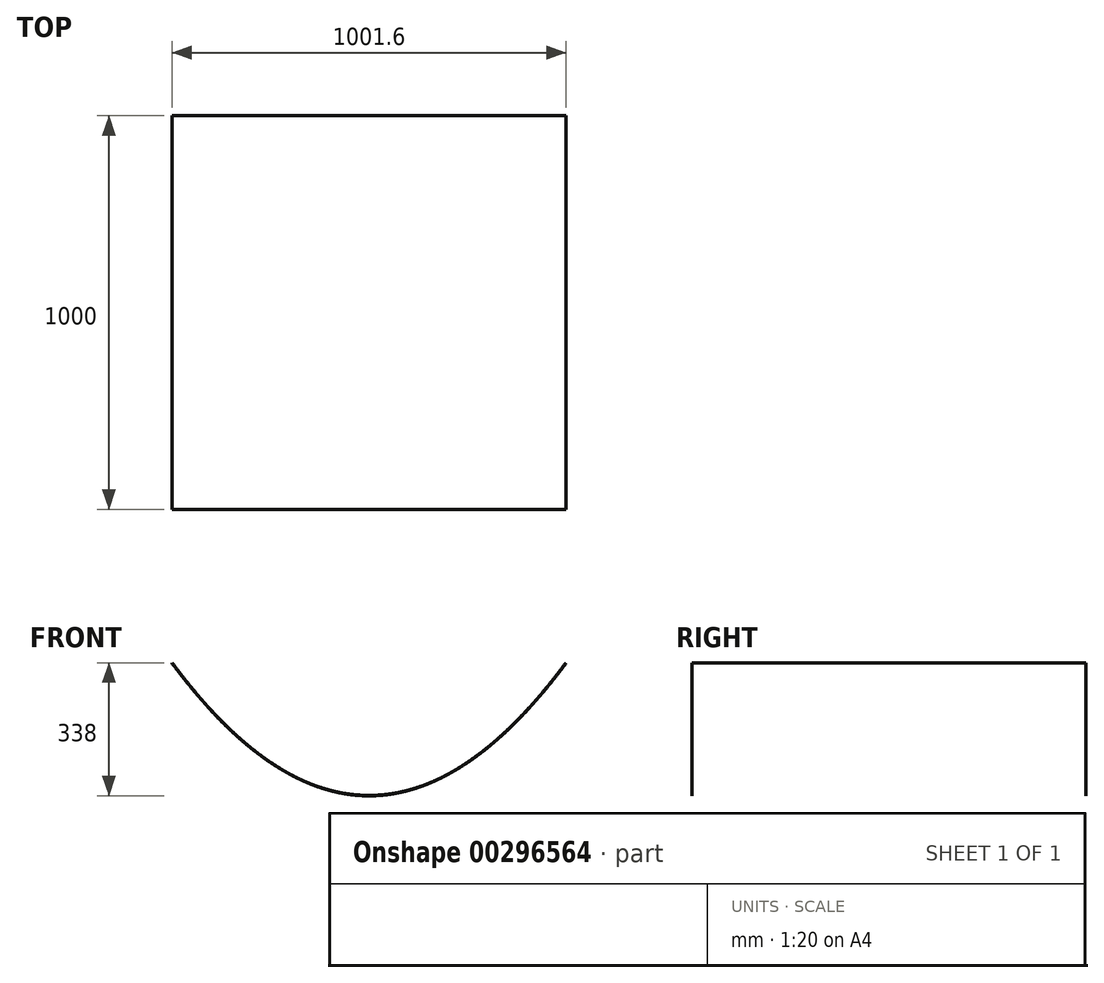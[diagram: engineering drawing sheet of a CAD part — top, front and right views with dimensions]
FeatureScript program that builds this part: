
annotation { "Feature Type Name" : "Feature", "Feature Type Description" : "" }
export const myFeature = defineFeature(function(context is Context, id is Id, definition is map)
    precondition{}
    {
        {
            var Q0;
            Q0=qCreatedBy(makeId("Front.planeOp"),FACE);
            var sketch = newSketch(context, id + "F0", { "sketchPlane" : qUnion([Q0])});
            skLineSegment(sketch, "E0", {"start": v(-500, 168.5) * mm, "end": v(-498.89, 167) * mm});
            skLineSegment(sketch, "E1", {"start": v(-498.89, 167) * mm, "end": v(-497.78, 165.5) * mm});
            skLineSegment(sketch, "E2", {"start": v(-497.78, 165.5) * mm, "end": v(-496.67, 164.02) * mm});
            skLineSegment(sketch, "E3", {"start": v(-496.67, 164.02) * mm, "end": v(-495.56, 162.53) * mm});
            skLineSegment(sketch, "E4", {"start": v(-495.56, 162.53) * mm, "end": v(-494.44, 161.05) * mm});
            skLineSegment(sketch, "E5", {"start": v(-494.44, 161.05) * mm, "end": v(-493.33, 159.57) * mm});
            skLineSegment(sketch, "E6", {"start": v(-493.33, 159.57) * mm, "end": v(-492.22, 158.1) * mm});
            skLineSegment(sketch, "E7", {"start": v(-492.22, 158.1) * mm, "end": v(-491.11, 156.62) * mm});
            skLineSegment(sketch, "E8", {"start": v(-491.11, 156.62) * mm, "end": v(-490, 155.15) * mm});
            skLineSegment(sketch, "E9", {"start": v(-490, 155.15) * mm, "end": v(-488.89, 153.69) * mm});
            skLineSegment(sketch, "E10", {"start": v(-488.89, 153.69) * mm, "end": v(-487.78, 152.22) * mm});
            skLineSegment(sketch, "E11", {"start": v(-487.78, 152.22) * mm, "end": v(-486.67, 150.76) * mm});
            skLineSegment(sketch, "E12", {"start": v(-486.67, 150.76) * mm, "end": v(-485.56, 149.3) * mm});
            skLineSegment(sketch, "E13", {"start": v(-485.56, 149.3) * mm, "end": v(-484.44, 147.86) * mm});
            skLineSegment(sketch, "E14", {"start": v(-484.44, 147.86) * mm, "end": v(-483.33, 146.4) * mm});
            skLineSegment(sketch, "E15", {"start": v(-483.33, 146.4) * mm, "end": v(-482.22, 144.96) * mm});
            skLineSegment(sketch, "E16", {"start": v(-482.22, 144.96) * mm, "end": v(-481.11, 143.52) * mm});
            skLineSegment(sketch, "E17", {"start": v(-481.11, 143.52) * mm, "end": v(-480, 142.08) * mm});
            skLineSegment(sketch, "E18", {"start": v(-480, 142.08) * mm, "end": v(-478.89, 140.64) * mm});
            skLineSegment(sketch, "E19", {"start": v(-478.89, 140.64) * mm, "end": v(-477.78, 139.2) * mm});
            skLineSegment(sketch, "E20", {"start": v(-477.78, 139.2) * mm, "end": v(-476.67, 137.78) * mm});
            skLineSegment(sketch, "E21", {"start": v(-476.67, 137.78) * mm, "end": v(-475.56, 136.35) * mm});
            skLineSegment(sketch, "E22", {"start": v(-475.56, 136.35) * mm, "end": v(-474.44, 134.93) * mm});
            skLineSegment(sketch, "E23", {"start": v(-474.44, 134.93) * mm, "end": v(-473.33, 133.5) * mm});
            skLineSegment(sketch, "E24", {"start": v(-473.33, 133.5) * mm, "end": v(-472.22, 132.1) * mm});
            skLineSegment(sketch, "E25", {"start": v(-472.22, 132.1) * mm, "end": v(-471.11, 130.68) * mm});
            skLineSegment(sketch, "E26", {"start": v(-471.11, 130.68) * mm, "end": v(-470, 129.27) * mm});
            skLineSegment(sketch, "E27", {"start": v(-470, 129.27) * mm, "end": v(-468.89, 127.86) * mm});
            skLineSegment(sketch, "E28", {"start": v(-468.89, 127.86) * mm, "end": v(-467.78, 126.46) * mm});
            skLineSegment(sketch, "E29", {"start": v(-467.78, 126.46) * mm, "end": v(-466.67, 125.06) * mm});
            skLineSegment(sketch, "E30", {"start": v(-466.67, 125.06) * mm, "end": v(-465.56, 123.67) * mm});
            skLineSegment(sketch, "E31", {"start": v(-465.56, 123.67) * mm, "end": v(-464.44, 122.27) * mm});
            skLineSegment(sketch, "E32", {"start": v(-464.44, 122.27) * mm, "end": v(-463.33, 120.88) * mm});
            skLineSegment(sketch, "E33", {"start": v(-463.33, 120.88) * mm, "end": v(-462.22, 119.5) * mm});
            skLineSegment(sketch, "E34", {"start": v(-462.22, 119.5) * mm, "end": v(-461.11, 118.11) * mm});
            skLineSegment(sketch, "E35", {"start": v(-461.11, 118.11) * mm, "end": v(-460, 116.73) * mm});
            skLineSegment(sketch, "E36", {"start": v(-460, 116.73) * mm, "end": v(-458.89, 115.36) * mm});
            skLineSegment(sketch, "E37", {"start": v(-458.89, 115.36) * mm, "end": v(-457.78, 113.99) * mm});
            skLineSegment(sketch, "E38", {"start": v(-457.78, 113.99) * mm, "end": v(-456.67, 112.62) * mm});
            skLineSegment(sketch, "E39", {"start": v(-456.67, 112.62) * mm, "end": v(-455.56, 111.25) * mm});
            skLineSegment(sketch, "E40", {"start": v(-455.56, 111.25) * mm, "end": v(-454.44, 109.89) * mm});
            skLineSegment(sketch, "E41", {"start": v(-454.44, 109.89) * mm, "end": v(-453.33, 108.53) * mm});
            skLineSegment(sketch, "E42", {"start": v(-453.33, 108.53) * mm, "end": v(-452.22, 107.17) * mm});
            skLineSegment(sketch, "E43", {"start": v(-452.22, 107.17) * mm, "end": v(-451.11, 105.82) * mm});
            skLineSegment(sketch, "E44", {"start": v(-451.11, 105.82) * mm, "end": v(-450, 104.47) * mm});
            skLineSegment(sketch, "E45", {"start": v(-450, 104.47) * mm, "end": v(-448.89, 103.12) * mm});
            skLineSegment(sketch, "E46", {"start": v(-448.89, 103.12) * mm, "end": v(-447.78, 101.78) * mm});
            skLineSegment(sketch, "E47", {"start": v(-447.78, 101.78) * mm, "end": v(-446.67, 100.44) * mm});
            skLineSegment(sketch, "E48", {"start": v(-446.67, 100.44) * mm, "end": v(-445.56, 99.1) * mm});
            skLineSegment(sketch, "E49", {"start": v(-445.56, 99.1) * mm, "end": v(-444.44, 97.77) * mm});
            skLineSegment(sketch, "E50", {"start": v(-444.44, 97.77) * mm, "end": v(-443.33, 96.44) * mm});
            skLineSegment(sketch, "E51", {"start": v(-443.33, 96.44) * mm, "end": v(-442.22, 95.11) * mm});
            skLineSegment(sketch, "E52", {"start": v(-442.22, 95.11) * mm, "end": v(-441.11, 93.8) * mm});
            skLineSegment(sketch, "E53", {"start": v(-441.11, 93.8) * mm, "end": v(-440, 92.47) * mm});
            skLineSegment(sketch, "E54", {"start": v(-440, 92.47) * mm, "end": v(-438.89, 91.15) * mm});
            skLineSegment(sketch, "E55", {"start": v(-438.89, 91.15) * mm, "end": v(-437.78, 89.84) * mm});
            skLineSegment(sketch, "E56", {"start": v(-437.78, 89.84) * mm, "end": v(-436.67, 88.53) * mm});
            skLineSegment(sketch, "E57", {"start": v(-436.67, 88.53) * mm, "end": v(-435.56, 87.23) * mm});
            skLineSegment(sketch, "E58", {"start": v(-435.56, 87.23) * mm, "end": v(-434.44, 85.92) * mm});
            skLineSegment(sketch, "E59", {"start": v(-434.44, 85.92) * mm, "end": v(-433.33, 84.62) * mm});
            skLineSegment(sketch, "E60", {"start": v(-433.33, 84.62) * mm, "end": v(-432.22, 83.33) * mm});
            skLineSegment(sketch, "E61", {"start": v(-432.22, 83.33) * mm, "end": v(-431.11, 82.03) * mm});
            skLineSegment(sketch, "E62", {"start": v(-431.11, 82.03) * mm, "end": v(-430, 80.74) * mm});
            skLineSegment(sketch, "E63", {"start": v(-430, 80.74) * mm, "end": v(-428.89, 79.46) * mm});
            skLineSegment(sketch, "E64", {"start": v(-428.89, 79.46) * mm, "end": v(-427.78, 78.17) * mm});
            skLineSegment(sketch, "E65", {"start": v(-427.78, 78.17) * mm, "end": v(-426.67, 76.9) * mm});
            skLineSegment(sketch, "E66", {"start": v(-426.67, 76.9) * mm, "end": v(-425.56, 75.62) * mm});
            skLineSegment(sketch, "E67", {"start": v(-425.56, 75.62) * mm, "end": v(-424.44, 74.34) * mm});
            skLineSegment(sketch, "E68", {"start": v(-424.44, 74.34) * mm, "end": v(-423.33, 73.07) * mm});
            skLineSegment(sketch, "E69", {"start": v(-423.33, 73.07) * mm, "end": v(-422.22, 71.8) * mm});
            skLineSegment(sketch, "E70", {"start": v(-422.22, 71.8) * mm, "end": v(-421.11, 70.54) * mm});
            skLineSegment(sketch, "E71", {"start": v(-421.11, 70.54) * mm, "end": v(-420, 69.29) * mm});
            skLineSegment(sketch, "E72", {"start": v(-420, 69.29) * mm, "end": v(-418.89, 68.03) * mm});
            skLineSegment(sketch, "E73", {"start": v(-418.89, 68.03) * mm, "end": v(-417.78, 66.78) * mm});
            skLineSegment(sketch, "E74", {"start": v(-417.78, 66.78) * mm, "end": v(-416.67, 65.53) * mm});
            skLineSegment(sketch, "E75", {"start": v(-416.67, 65.53) * mm, "end": v(-415.56, 64.28) * mm});
            skLineSegment(sketch, "E76", {"start": v(-415.56, 64.28) * mm, "end": v(-414.44, 63.04) * mm});
            skLineSegment(sketch, "E77", {"start": v(-414.44, 63.04) * mm, "end": v(-413.33, 61.8) * mm});
            skLineSegment(sketch, "E78", {"start": v(-413.33, 61.8) * mm, "end": v(-412.22, 60.56) * mm});
            skLineSegment(sketch, "E79", {"start": v(-412.22, 60.56) * mm, "end": v(-411.11, 59.33) * mm});
            skLineSegment(sketch, "E80", {"start": v(-411.11, 59.33) * mm, "end": v(-410, 58.1) * mm});
            skLineSegment(sketch, "E81", {"start": v(-410, 58.1) * mm, "end": v(-408.89, 56.87) * mm});
            skLineSegment(sketch, "E82", {"start": v(-408.89, 56.87) * mm, "end": v(-407.78, 55.65) * mm});
            skLineSegment(sketch, "E83", {"start": v(-407.78, 55.65) * mm, "end": v(-406.67, 54.43) * mm});
            skLineSegment(sketch, "E84", {"start": v(-406.67, 54.43) * mm, "end": v(-405.56, 53.21) * mm});
            skLineSegment(sketch, "E85", {"start": v(-405.56, 53.21) * mm, "end": v(-404.44, 52) * mm});
            skLineSegment(sketch, "E86", {"start": v(-404.44, 52) * mm, "end": v(-403.33, 50.79) * mm});
            skLineSegment(sketch, "E87", {"start": v(-403.33, 50.79) * mm, "end": v(-402.22, 49.58) * mm});
            skLineSegment(sketch, "E88", {"start": v(-402.22, 49.58) * mm, "end": v(-401.11, 48.38) * mm});
            skLineSegment(sketch, "E89", {"start": v(-401.11, 48.38) * mm, "end": v(-400, 47.18) * mm});
            skLineSegment(sketch, "E90", {"start": v(-400, 47.18) * mm, "end": v(-398.89, 45.98) * mm});
            skLineSegment(sketch, "E91", {"start": v(-398.89, 45.98) * mm, "end": v(-397.78, 44.79) * mm});
            skLineSegment(sketch, "E92", {"start": v(-397.78, 44.79) * mm, "end": v(-396.67, 43.6) * mm});
            skLineSegment(sketch, "E93", {"start": v(-396.67, 43.6) * mm, "end": v(-395.56, 42.41) * mm});
            skLineSegment(sketch, "E94", {"start": v(-395.56, 42.41) * mm, "end": v(-394.44, 41.23) * mm});
            skLineSegment(sketch, "E95", {"start": v(-394.44, 41.23) * mm, "end": v(-393.33, 40.05) * mm});
            skLineSegment(sketch, "E96", {"start": v(-393.33, 40.05) * mm, "end": v(-392.22, 38.87) * mm});
            skLineSegment(sketch, "E97", {"start": v(-392.22, 38.87) * mm, "end": v(-391.11, 37.7) * mm});
            skLineSegment(sketch, "E98", {"start": v(-391.11, 37.7) * mm, "end": v(-390, 36.53) * mm});
            skLineSegment(sketch, "E99", {"start": v(-390, 36.53) * mm, "end": v(-388.89, 35.36) * mm});
            skLineSegment(sketch, "E100", {"start": v(-388.89, 35.36) * mm, "end": v(-387.78, 34.2) * mm});
            skLineSegment(sketch, "E101", {"start": v(-387.78, 34.2) * mm, "end": v(-386.67, 33.04) * mm});
            skLineSegment(sketch, "E102", {"start": v(-386.67, 33.04) * mm, "end": v(-385.56, 31.88) * mm});
            skLineSegment(sketch, "E103", {"start": v(-385.56, 31.88) * mm, "end": v(-384.44, 30.73) * mm});
            skLineSegment(sketch, "E104", {"start": v(-384.44, 30.73) * mm, "end": v(-383.33, 29.58) * mm});
            skLineSegment(sketch, "E105", {"start": v(-383.33, 29.58) * mm, "end": v(-382.22, 28.43) * mm});
            skLineSegment(sketch, "E106", {"start": v(-382.22, 28.43) * mm, "end": v(-381.11, 27.29) * mm});
            skLineSegment(sketch, "E107", {"start": v(-381.11, 27.29) * mm, "end": v(-380, 26.15) * mm});
            skLineSegment(sketch, "E108", {"start": v(-380, 26.15) * mm, "end": v(-378.89, 25.01) * mm});
            skLineSegment(sketch, "E109", {"start": v(-378.89, 25.01) * mm, "end": v(-377.78, 23.88) * mm});
            skLineSegment(sketch, "E110", {"start": v(-377.78, 23.88) * mm, "end": v(-376.67, 22.75) * mm});
            skLineSegment(sketch, "E111", {"start": v(-376.67, 22.75) * mm, "end": v(-375.56, 21.62) * mm});
            skLineSegment(sketch, "E112", {"start": v(-375.56, 21.62) * mm, "end": v(-374.44, 20.5) * mm});
            skLineSegment(sketch, "E113", {"start": v(-374.44, 20.5) * mm, "end": v(-373.33, 19.38) * mm});
            skLineSegment(sketch, "E114", {"start": v(-373.33, 19.38) * mm, "end": v(-372.22, 18.26) * mm});
            skLineSegment(sketch, "E115", {"start": v(-372.22, 18.26) * mm, "end": v(-371.11, 17.15) * mm});
            skLineSegment(sketch, "E116", {"start": v(-371.11, 17.15) * mm, "end": v(-370, 16.04) * mm});
            skLineSegment(sketch, "E117", {"start": v(-370, 16.04) * mm, "end": v(-368.89, 14.93) * mm});
            skLineSegment(sketch, "E118", {"start": v(-368.89, 14.93) * mm, "end": v(-367.78, 13.83) * mm});
            skLineSegment(sketch, "E119", {"start": v(-367.78, 13.83) * mm, "end": v(-366.67, 12.73) * mm});
            skLineSegment(sketch, "E120", {"start": v(-366.67, 12.73) * mm, "end": v(-365.56, 11.63) * mm});
            skLineSegment(sketch, "E121", {"start": v(-365.56, 11.63) * mm, "end": v(-364.44, 10.54) * mm});
            skLineSegment(sketch, "E122", {"start": v(-364.44, 10.54) * mm, "end": v(-363.33, 9.45) * mm});
            skLineSegment(sketch, "E123", {"start": v(-363.33, 9.45) * mm, "end": v(-362.22, 8.36) * mm});
            skLineSegment(sketch, "E124", {"start": v(-362.22, 8.36) * mm, "end": v(-361.11, 7.28) * mm});
            skLineSegment(sketch, "E125", {"start": v(-361.11, 7.28) * mm, "end": v(-360, 6.2) * mm});
            skLineSegment(sketch, "E126", {"start": v(-360, 6.2) * mm, "end": v(-358.89, 5.12) * mm});
            skLineSegment(sketch, "E127", {"start": v(-358.89, 5.12) * mm, "end": v(-357.78, 4.05) * mm});
            skLineSegment(sketch, "E128", {"start": v(-357.78, 4.05) * mm, "end": v(-356.67, 2.98) * mm});
            skLineSegment(sketch, "E129", {"start": v(-356.67, 2.98) * mm, "end": v(-355.56, 1.91) * mm});
            skLineSegment(sketch, "E130", {"start": v(-355.56, 1.91) * mm, "end": v(-354.44, 0.85) * mm});
            skLineSegment(sketch, "E131", {"start": v(-354.44, 0.85) * mm, "end": v(-353.33, -0.21) * mm});
            skLineSegment(sketch, "E132", {"start": v(-353.33, -0.21) * mm, "end": v(-352.22, -1.27) * mm});
            skLineSegment(sketch, "E133", {"start": v(-352.22, -1.27) * mm, "end": v(-351.11, -2.32) * mm});
            skLineSegment(sketch, "E134", {"start": v(-351.11, -2.32) * mm, "end": v(-350, -3.37) * mm});
            skLineSegment(sketch, "E135", {"start": v(-350, -3.37) * mm, "end": v(-348.89, -4.42) * mm});
            skLineSegment(sketch, "E136", {"start": v(-348.89, -4.42) * mm, "end": v(-347.78, -5.46) * mm});
            skLineSegment(sketch, "E137", {"start": v(-347.78, -5.46) * mm, "end": v(-346.67, -6.5) * mm});
            skLineSegment(sketch, "E138", {"start": v(-346.67, -6.5) * mm, "end": v(-345.56, -7.54) * mm});
            skLineSegment(sketch, "E139", {"start": v(-345.56, -7.54) * mm, "end": v(-344.44, -8.57) * mm});
            skLineSegment(sketch, "E140", {"start": v(-344.44, -8.57) * mm, "end": v(-343.33, -9.6) * mm});
            skLineSegment(sketch, "E141", {"start": v(-343.33, -9.6) * mm, "end": v(-342.22, -10.63) * mm});
            skLineSegment(sketch, "E142", {"start": v(-342.22, -10.63) * mm, "end": v(-341.11, -11.65) * mm});
            skLineSegment(sketch, "E143", {"start": v(-341.11, -11.65) * mm, "end": v(-340, -12.67) * mm});
            skLineSegment(sketch, "E144", {"start": v(-340, -12.67) * mm, "end": v(-338.89, -13.7) * mm});
            skLineSegment(sketch, "E145", {"start": v(-338.89, -13.7) * mm, "end": v(-337.78, -14.7) * mm});
            skLineSegment(sketch, "E146", {"start": v(-337.78, -14.7) * mm, "end": v(-336.67, -15.71) * mm});
            skLineSegment(sketch, "E147", {"start": v(-336.67, -15.71) * mm, "end": v(-335.56, -16.72) * mm});
            skLineSegment(sketch, "E148", {"start": v(-335.56, -16.72) * mm, "end": v(-334.44, -17.72) * mm});
            skLineSegment(sketch, "E149", {"start": v(-334.44, -17.72) * mm, "end": v(-333.33, -18.72) * mm});
            skLineSegment(sketch, "E150", {"start": v(-333.33, -18.72) * mm, "end": v(-332.22, -19.72) * mm});
            skLineSegment(sketch, "E151", {"start": v(-332.22, -19.72) * mm, "end": v(-331.11, -20.71) * mm});
            skLineSegment(sketch, "E152", {"start": v(-331.11, -20.71) * mm, "end": v(-330, -21.7) * mm});
            skLineSegment(sketch, "E153", {"start": v(-330, -21.7) * mm, "end": v(-328.89, -22.7) * mm});
            skLineSegment(sketch, "E154", {"start": v(-328.89, -22.7) * mm, "end": v(-327.78, -23.68) * mm});
            skLineSegment(sketch, "E155", {"start": v(-327.78, -23.68) * mm, "end": v(-326.67, -24.66) * mm});
            skLineSegment(sketch, "E156", {"start": v(-326.67, -24.66) * mm, "end": v(-325.56, -25.63) * mm});
            skLineSegment(sketch, "E157", {"start": v(-325.56, -25.63) * mm, "end": v(-324.44, -26.6) * mm});
            skLineSegment(sketch, "E158", {"start": v(-324.44, -26.6) * mm, "end": v(-323.33, -27.58) * mm});
            skLineSegment(sketch, "E159", {"start": v(-323.33, -27.58) * mm, "end": v(-322.22, -28.54) * mm});
            skLineSegment(sketch, "E160", {"start": v(-322.22, -28.54) * mm, "end": v(-321.11, -29.5) * mm});
            skLineSegment(sketch, "E161", {"start": v(-321.11, -29.5) * mm, "end": v(-320, -30.47) * mm});
            skLineSegment(sketch, "E162", {"start": v(-320, -30.47) * mm, "end": v(-318.89, -31.42) * mm});
            skLineSegment(sketch, "E163", {"start": v(-318.89, -31.42) * mm, "end": v(-317.78, -32.38) * mm});
            skLineSegment(sketch, "E164", {"start": v(-317.78, -32.38) * mm, "end": v(-316.67, -33.33) * mm});
            skLineSegment(sketch, "E165", {"start": v(-316.67, -33.33) * mm, "end": v(-315.56, -34.27) * mm});
            skLineSegment(sketch, "E166", {"start": v(-315.56, -34.27) * mm, "end": v(-314.44, -35.22) * mm});
            skLineSegment(sketch, "E167", {"start": v(-314.44, -35.22) * mm, "end": v(-313.33, -36.16) * mm});
            skLineSegment(sketch, "E168", {"start": v(-313.33, -36.16) * mm, "end": v(-312.22, -37.1) * mm});
            skLineSegment(sketch, "E169", {"start": v(-312.22, -37.1) * mm, "end": v(-311.11, -38.03) * mm});
            skLineSegment(sketch, "E170", {"start": v(-311.11, -38.03) * mm, "end": v(-310, -38.96) * mm});
            skLineSegment(sketch, "E171", {"start": v(-310, -38.96) * mm, "end": v(-308.89, -39.89) * mm});
            skLineSegment(sketch, "E172", {"start": v(-308.89, -39.89) * mm, "end": v(-307.78, -40.8) * mm});
            skLineSegment(sketch, "E173", {"start": v(-307.78, -40.8) * mm, "end": v(-306.67, -41.73) * mm});
            skLineSegment(sketch, "E174", {"start": v(-306.67, -41.73) * mm, "end": v(-305.56, -42.65) * mm});
            skLineSegment(sketch, "E175", {"start": v(-305.56, -42.65) * mm, "end": v(-304.44, -43.56) * mm});
            skLineSegment(sketch, "E176", {"start": v(-304.44, -43.56) * mm, "end": v(-303.33, -44.47) * mm});
            skLineSegment(sketch, "E177", {"start": v(-303.33, -44.47) * mm, "end": v(-302.22, -45.38) * mm});
            skLineSegment(sketch, "E178", {"start": v(-302.22, -45.38) * mm, "end": v(-301.11, -46.28) * mm});
            skLineSegment(sketch, "E179", {"start": v(-301.11, -46.28) * mm, "end": v(-300, -47.18) * mm});
            skLineSegment(sketch, "E180", {"start": v(-300, -47.18) * mm, "end": v(-298.89, -48.08) * mm});
            skLineSegment(sketch, "E181", {"start": v(-298.89, -48.08) * mm, "end": v(-297.78, -48.97) * mm});
            skLineSegment(sketch, "E182", {"start": v(-297.78, -48.97) * mm, "end": v(-296.67, -49.86) * mm});
            skLineSegment(sketch, "E183", {"start": v(-296.67, -49.86) * mm, "end": v(-295.56, -50.75) * mm});
            skLineSegment(sketch, "E184", {"start": v(-295.56, -50.75) * mm, "end": v(-294.44, -51.63) * mm});
            skLineSegment(sketch, "E185", {"start": v(-294.44, -51.63) * mm, "end": v(-293.33, -52.51) * mm});
            skLineSegment(sketch, "E186", {"start": v(-293.33, -52.51) * mm, "end": v(-292.22, -53.4) * mm});
            skLineSegment(sketch, "E187", {"start": v(-292.22, -53.4) * mm, "end": v(-291.11, -54.26) * mm});
            skLineSegment(sketch, "E188", {"start": v(-291.11, -54.26) * mm, "end": v(-290, -55.14) * mm});
            skLineSegment(sketch, "E189", {"start": v(-290, -55.14) * mm, "end": v(-288.89, -56) * mm});
            skLineSegment(sketch, "E190", {"start": v(-288.89, -56) * mm, "end": v(-287.78, -56.87) * mm});
            skLineSegment(sketch, "E191", {"start": v(-287.78, -56.87) * mm, "end": v(-286.67, -57.73) * mm});
            skLineSegment(sketch, "E192", {"start": v(-286.67, -57.73) * mm, "end": v(-285.56, -58.58) * mm});
            skLineSegment(sketch, "E193", {"start": v(-285.56, -58.58) * mm, "end": v(-284.44, -59.44) * mm});
            skLineSegment(sketch, "E194", {"start": v(-284.44, -59.44) * mm, "end": v(-283.33, -60.29) * mm});
            skLineSegment(sketch, "E195", {"start": v(-283.33, -60.29) * mm, "end": v(-282.22, -61.13) * mm});
            skLineSegment(sketch, "E196", {"start": v(-282.22, -61.13) * mm, "end": v(-281.11, -61.98) * mm});
            skLineSegment(sketch, "E197", {"start": v(-281.11, -61.98) * mm, "end": v(-280, -62.82) * mm});
            skLineSegment(sketch, "E198", {"start": v(-280, -62.82) * mm, "end": v(-278.89, -63.66) * mm});
            skLineSegment(sketch, "E199", {"start": v(-278.89, -63.66) * mm, "end": v(-277.78, -64.49) * mm});
            skLineSegment(sketch, "E200", {"start": v(-277.78, -64.49) * mm, "end": v(-276.67, -65.32) * mm});
            skLineSegment(sketch, "E201", {"start": v(-276.67, -65.32) * mm, "end": v(-275.56, -66.15) * mm});
            skLineSegment(sketch, "E202", {"start": v(-275.56, -66.15) * mm, "end": v(-274.44, -66.97) * mm});
            skLineSegment(sketch, "E203", {"start": v(-274.44, -66.97) * mm, "end": v(-273.33, -67.8) * mm});
            skLineSegment(sketch, "E204", {"start": v(-273.33, -67.8) * mm, "end": v(-272.22, -68.6) * mm});
            skLineSegment(sketch, "E205", {"start": v(-272.22, -68.6) * mm, "end": v(-271.11, -69.42) * mm});
            skLineSegment(sketch, "E206", {"start": v(-271.11, -69.42) * mm, "end": v(-270, -70.23) * mm});
            skLineSegment(sketch, "E207", {"start": v(-270, -70.23) * mm, "end": v(-268.89, -71.04) * mm});
            skLineSegment(sketch, "E208", {"start": v(-268.89, -71.04) * mm, "end": v(-267.78, -71.84) * mm});
            skLineSegment(sketch, "E209", {"start": v(-267.78, -71.84) * mm, "end": v(-266.67, -72.64) * mm});
            skLineSegment(sketch, "E210", {"start": v(-266.67, -72.64) * mm, "end": v(-265.56, -73.44) * mm});
            skLineSegment(sketch, "E211", {"start": v(-265.56, -73.44) * mm, "end": v(-264.44, -74.24) * mm});
            skLineSegment(sketch, "E212", {"start": v(-264.44, -74.24) * mm, "end": v(-263.33, -75.03) * mm});
            skLineSegment(sketch, "E213", {"start": v(-263.33, -75.03) * mm, "end": v(-262.22, -75.81) * mm});
            skLineSegment(sketch, "E214", {"start": v(-262.22, -75.81) * mm, "end": v(-261.11, -76.6) * mm});
            skLineSegment(sketch, "E215", {"start": v(-261.11, -76.6) * mm, "end": v(-260, -77.38) * mm});
            skLineSegment(sketch, "E216", {"start": v(-260, -77.38) * mm, "end": v(-258.89, -78.15) * mm});
            skLineSegment(sketch, "E217", {"start": v(-258.89, -78.15) * mm, "end": v(-257.78, -78.93) * mm});
            skLineSegment(sketch, "E218", {"start": v(-257.78, -78.93) * mm, "end": v(-256.67, -79.7) * mm});
            skLineSegment(sketch, "E219", {"start": v(-256.67, -79.7) * mm, "end": v(-255.56, -80.47) * mm});
            skLineSegment(sketch, "E220", {"start": v(-255.56, -80.47) * mm, "end": v(-254.44, -81.23) * mm});
            skLineSegment(sketch, "E221", {"start": v(-254.44, -81.23) * mm, "end": v(-253.33, -82) * mm});
            skLineSegment(sketch, "E222", {"start": v(-253.33, -82) * mm, "end": v(-252.22, -82.75) * mm});
            skLineSegment(sketch, "E223", {"start": v(-252.22, -82.75) * mm, "end": v(-251.11, -83.5) * mm});
            skLineSegment(sketch, "E224", {"start": v(-251.11, -83.5) * mm, "end": v(-250, -84.25) * mm});
            skLineSegment(sketch, "E225", {"start": v(-250, -84.25) * mm, "end": v(-248.89, -85) * mm});
            skLineSegment(sketch, "E226", {"start": v(-248.89, -85) * mm, "end": v(-247.78, -85.74) * mm});
            skLineSegment(sketch, "E227", {"start": v(-247.78, -85.74) * mm, "end": v(-246.67, -86.48) * mm});
            skLineSegment(sketch, "E228", {"start": v(-246.67, -86.48) * mm, "end": v(-245.56, -87.22) * mm});
            skLineSegment(sketch, "E229", {"start": v(-245.56, -87.22) * mm, "end": v(-244.44, -87.95) * mm});
            skLineSegment(sketch, "E230", {"start": v(-244.44, -87.95) * mm, "end": v(-243.33, -88.69) * mm});
            skLineSegment(sketch, "E231", {"start": v(-243.33, -88.69) * mm, "end": v(-242.22, -89.41) * mm});
            skLineSegment(sketch, "E232", {"start": v(-242.22, -89.41) * mm, "end": v(-241.11, -90.14) * mm});
            skLineSegment(sketch, "E233", {"start": v(-241.11, -90.14) * mm, "end": v(-240, -90.86) * mm});
            skLineSegment(sketch, "E234", {"start": v(-240, -90.86) * mm, "end": v(-238.89, -91.57) * mm});
            skLineSegment(sketch, "E235", {"start": v(-238.89, -91.57) * mm, "end": v(-237.78, -92.29) * mm});
            skLineSegment(sketch, "E236", {"start": v(-237.78, -92.29) * mm, "end": v(-236.67, -93) * mm});
            skLineSegment(sketch, "E237", {"start": v(-236.67, -93) * mm, "end": v(-235.56, -93.7) * mm});
            skLineSegment(sketch, "E238", {"start": v(-235.56, -93.7) * mm, "end": v(-234.44, -94.41) * mm});
            skLineSegment(sketch, "E239", {"start": v(-234.44, -94.41) * mm, "end": v(-233.33, -95.11) * mm});
            skLineSegment(sketch, "E240", {"start": v(-233.33, -95.11) * mm, "end": v(-232.22, -95.8) * mm});
            skLineSegment(sketch, "E241", {"start": v(-232.22, -95.8) * mm, "end": v(-231.11, -96.5) * mm});
            skLineSegment(sketch, "E242", {"start": v(-231.11, -96.5) * mm, "end": v(-230, -97.2) * mm});
            skLineSegment(sketch, "E243", {"start": v(-230, -97.2) * mm, "end": v(-228.89, -97.88) * mm});
            skLineSegment(sketch, "E244", {"start": v(-228.89, -97.88) * mm, "end": v(-227.78, -98.56) * mm});
            skLineSegment(sketch, "E245", {"start": v(-227.78, -98.56) * mm, "end": v(-226.67, -99.24) * mm});
            skLineSegment(sketch, "E246", {"start": v(-226.67, -99.24) * mm, "end": v(-225.56, -99.92) * mm});
            skLineSegment(sketch, "E247", {"start": v(-225.56, -99.92) * mm, "end": v(-224.44, -100.6) * mm});
            skLineSegment(sketch, "E248", {"start": v(-224.44, -100.6) * mm, "end": v(-223.33, -101.27) * mm});
            skLineSegment(sketch, "E249", {"start": v(-223.33, -101.27) * mm, "end": v(-222.22, -101.93) * mm});
            skLineSegment(sketch, "E250", {"start": v(-222.22, -101.93) * mm, "end": v(-221.11, -102.6) * mm});
            skLineSegment(sketch, "E251", {"start": v(-221.11, -102.6) * mm, "end": v(-220, -103.26) * mm});
            skLineSegment(sketch, "E252", {"start": v(-220, -103.26) * mm, "end": v(-218.89, -103.92) * mm});
            skLineSegment(sketch, "E253", {"start": v(-218.89, -103.92) * mm, "end": v(-217.78, -104.57) * mm});
            skLineSegment(sketch, "E254", {"start": v(-217.78, -104.57) * mm, "end": v(-216.67, -105.22) * mm});
            skLineSegment(sketch, "E255", {"start": v(-216.67, -105.22) * mm, "end": v(-215.56, -105.87) * mm});
            skLineSegment(sketch, "E256", {"start": v(-215.56, -105.87) * mm, "end": v(-214.44, -106.51) * mm});
            skLineSegment(sketch, "E257", {"start": v(-214.44, -106.51) * mm, "end": v(-213.33, -107.15) * mm});
            skLineSegment(sketch, "E258", {"start": v(-213.33, -107.15) * mm, "end": v(-212.22, -107.8) * mm});
            skLineSegment(sketch, "E259", {"start": v(-212.22, -107.8) * mm, "end": v(-211.11, -108.42) * mm});
            skLineSegment(sketch, "E260", {"start": v(-211.11, -108.42) * mm, "end": v(-210, -109.06) * mm});
            skLineSegment(sketch, "E261", {"start": v(-210, -109.06) * mm, "end": v(-208.89, -109.68) * mm});
            skLineSegment(sketch, "E262", {"start": v(-208.89, -109.68) * mm, "end": v(-207.78, -110.3) * mm});
            skLineSegment(sketch, "E263", {"start": v(-207.78, -110.3) * mm, "end": v(-206.67, -110.93) * mm});
            skLineSegment(sketch, "E264", {"start": v(-206.67, -110.93) * mm, "end": v(-205.56, -111.54) * mm});
            skLineSegment(sketch, "E265", {"start": v(-205.56, -111.54) * mm, "end": v(-204.44, -112.16) * mm});
            skLineSegment(sketch, "E266", {"start": v(-204.44, -112.16) * mm, "end": v(-203.33, -112.77) * mm});
            skLineSegment(sketch, "E267", {"start": v(-203.33, -112.77) * mm, "end": v(-202.22, -113.38) * mm});
            skLineSegment(sketch, "E268", {"start": v(-202.22, -113.38) * mm, "end": v(-201.11, -113.98) * mm});
            skLineSegment(sketch, "E269", {"start": v(-201.11, -113.98) * mm, "end": v(-200, -114.58) * mm});
            skLineSegment(sketch, "E270", {"start": v(-200, -114.58) * mm, "end": v(-198.89, -115.18) * mm});
            skLineSegment(sketch, "E271", {"start": v(-198.89, -115.18) * mm, "end": v(-197.78, -115.77) * mm});
            skLineSegment(sketch, "E272", {"start": v(-197.78, -115.77) * mm, "end": v(-196.67, -116.36) * mm});
            skLineSegment(sketch, "E273", {"start": v(-196.67, -116.36) * mm, "end": v(-195.56, -116.95) * mm});
            skLineSegment(sketch, "E274", {"start": v(-195.56, -116.95) * mm, "end": v(-194.44, -117.54) * mm});
            skLineSegment(sketch, "E275", {"start": v(-194.44, -117.54) * mm, "end": v(-193.33, -118.12) * mm});
            skLineSegment(sketch, "E276", {"start": v(-193.33, -118.12) * mm, "end": v(-192.22, -118.7) * mm});
            skLineSegment(sketch, "E277", {"start": v(-192.22, -118.7) * mm, "end": v(-191.11, -119.27) * mm});
            skLineSegment(sketch, "E278", {"start": v(-191.11, -119.27) * mm, "end": v(-190, -119.84) * mm});
            skLineSegment(sketch, "E279", {"start": v(-190, -119.84) * mm, "end": v(-188.89, -120.4) * mm});
            skLineSegment(sketch, "E280", {"start": v(-188.89, -120.4) * mm, "end": v(-187.78, -120.97) * mm});
            skLineSegment(sketch, "E281", {"start": v(-187.78, -120.97) * mm, "end": v(-186.67, -121.53) * mm});
            skLineSegment(sketch, "E282", {"start": v(-186.67, -121.53) * mm, "end": v(-185.56, -122.09) * mm});
            skLineSegment(sketch, "E283", {"start": v(-185.56, -122.09) * mm, "end": v(-184.44, -122.64) * mm});
            skLineSegment(sketch, "E284", {"start": v(-184.44, -122.64) * mm, "end": v(-183.33, -123.2) * mm});
            skLineSegment(sketch, "E285", {"start": v(-183.33, -123.2) * mm, "end": v(-182.22, -123.74) * mm});
            skLineSegment(sketch, "E286", {"start": v(-182.22, -123.74) * mm, "end": v(-181.11, -124.29) * mm});
            skLineSegment(sketch, "E287", {"start": v(-181.11, -124.29) * mm, "end": v(-180, -124.83) * mm});
            skLineSegment(sketch, "E288", {"start": v(-180, -124.83) * mm, "end": v(-178.89, -125.36) * mm});
            skLineSegment(sketch, "E289", {"start": v(-178.89, -125.36) * mm, "end": v(-177.78, -125.9) * mm});
            skLineSegment(sketch, "E290", {"start": v(-177.78, -125.9) * mm, "end": v(-176.67, -126.43) * mm});
            skLineSegment(sketch, "E291", {"start": v(-176.67, -126.43) * mm, "end": v(-175.56, -126.96) * mm});
            skLineSegment(sketch, "E292", {"start": v(-175.56, -126.96) * mm, "end": v(-174.44, -127.48) * mm});
            skLineSegment(sketch, "E293", {"start": v(-174.44, -127.48) * mm, "end": v(-173.33, -128) * mm});
            skLineSegment(sketch, "E294", {"start": v(-173.33, -128) * mm, "end": v(-172.22, -128.52) * mm});
            skLineSegment(sketch, "E295", {"start": v(-172.22, -128.52) * mm, "end": v(-171.11, -129.03) * mm});
            skLineSegment(sketch, "E296", {"start": v(-171.11, -129.03) * mm, "end": v(-170, -129.54) * mm});
            skLineSegment(sketch, "E297", {"start": v(-170, -129.54) * mm, "end": v(-168.89, -130.05) * mm});
            skLineSegment(sketch, "E298", {"start": v(-168.89, -130.05) * mm, "end": v(-167.78, -130.56) * mm});
            skLineSegment(sketch, "E299", {"start": v(-167.78, -130.56) * mm, "end": v(-166.67, -131.06) * mm});
            skLineSegment(sketch, "E300", {"start": v(-166.67, -131.06) * mm, "end": v(-165.56, -131.56) * mm});
            skLineSegment(sketch, "E301", {"start": v(-165.56, -131.56) * mm, "end": v(-164.44, -132.05) * mm});
            skLineSegment(sketch, "E302", {"start": v(-164.44, -132.05) * mm, "end": v(-163.33, -132.54) * mm});
            skLineSegment(sketch, "E303", {"start": v(-163.33, -132.54) * mm, "end": v(-162.22, -133.03) * mm});
            skLineSegment(sketch, "E304", {"start": v(-162.22, -133.03) * mm, "end": v(-161.11, -133.51) * mm});
            skLineSegment(sketch, "E305", {"start": v(-161.11, -133.51) * mm, "end": v(-160, -134) * mm});
            skLineSegment(sketch, "E306", {"start": v(-160, -134) * mm, "end": v(-158.89, -134.47) * mm});
            skLineSegment(sketch, "E307", {"start": v(-158.89, -134.47) * mm, "end": v(-157.78, -134.94) * mm});
            skLineSegment(sketch, "E308", {"start": v(-157.78, -134.94) * mm, "end": v(-156.67, -135.42) * mm});
            skLineSegment(sketch, "E309", {"start": v(-156.67, -135.42) * mm, "end": v(-155.56, -135.88) * mm});
            skLineSegment(sketch, "E310", {"start": v(-155.56, -135.88) * mm, "end": v(-154.44, -136.35) * mm});
            skLineSegment(sketch, "E311", {"start": v(-154.44, -136.35) * mm, "end": v(-153.33, -136.8) * mm});
            skLineSegment(sketch, "E312", {"start": v(-153.33, -136.8) * mm, "end": v(-152.22, -137.27) * mm});
            skLineSegment(sketch, "E313", {"start": v(-152.22, -137.27) * mm, "end": v(-151.11, -137.72) * mm});
            skLineSegment(sketch, "E314", {"start": v(-151.11, -137.72) * mm, "end": v(-150, -138.17) * mm});
            skLineSegment(sketch, "E315", {"start": v(-150, -138.17) * mm, "end": v(-148.89, -138.62) * mm});
            skLineSegment(sketch, "E316", {"start": v(-148.89, -138.62) * mm, "end": v(-147.78, -139.06) * mm});
            skLineSegment(sketch, "E317", {"start": v(-147.78, -139.06) * mm, "end": v(-146.67, -139.5) * mm});
            skLineSegment(sketch, "E318", {"start": v(-146.67, -139.5) * mm, "end": v(-145.56, -139.94) * mm});
            skLineSegment(sketch, "E319", {"start": v(-145.56, -139.94) * mm, "end": v(-144.44, -140.38) * mm});
            skLineSegment(sketch, "E320", {"start": v(-144.44, -140.38) * mm, "end": v(-143.33, -140.8) * mm});
            skLineSegment(sketch, "E321", {"start": v(-143.33, -140.8) * mm, "end": v(-142.22, -141.24) * mm});
            skLineSegment(sketch, "E322", {"start": v(-142.22, -141.24) * mm, "end": v(-141.11, -141.66) * mm});
            skLineSegment(sketch, "E323", {"start": v(-141.11, -141.66) * mm, "end": v(-140, -142.08) * mm});
            skLineSegment(sketch, "E324", {"start": v(-140, -142.08) * mm, "end": v(-138.89, -142.5) * mm});
            skLineSegment(sketch, "E325", {"start": v(-138.89, -142.5) * mm, "end": v(-137.78, -142.91) * mm});
            skLineSegment(sketch, "E326", {"start": v(-137.78, -142.91) * mm, "end": v(-136.67, -143.32) * mm});
            skLineSegment(sketch, "E327", {"start": v(-136.67, -143.32) * mm, "end": v(-135.56, -143.73) * mm});
            skLineSegment(sketch, "E328", {"start": v(-135.56, -143.73) * mm, "end": v(-134.44, -144.14) * mm});
            skLineSegment(sketch, "E329", {"start": v(-134.44, -144.14) * mm, "end": v(-133.33, -144.54) * mm});
            skLineSegment(sketch, "E330", {"start": v(-133.33, -144.54) * mm, "end": v(-132.22, -144.94) * mm});
            skLineSegment(sketch, "E331", {"start": v(-132.22, -144.94) * mm, "end": v(-131.11, -145.33) * mm});
            skLineSegment(sketch, "E332", {"start": v(-131.11, -145.33) * mm, "end": v(-130, -145.72) * mm});
            skLineSegment(sketch, "E333", {"start": v(-130, -145.72) * mm, "end": v(-128.89, -146.1) * mm});
            skLineSegment(sketch, "E334", {"start": v(-128.89, -146.1) * mm, "end": v(-127.78, -146.5) * mm});
            skLineSegment(sketch, "E335", {"start": v(-127.78, -146.5) * mm, "end": v(-126.67, -146.87) * mm});
            skLineSegment(sketch, "E336", {"start": v(-126.67, -146.87) * mm, "end": v(-125.56, -147.25) * mm});
            skLineSegment(sketch, "E337", {"start": v(-125.56, -147.25) * mm, "end": v(-124.44, -147.63) * mm});
            skLineSegment(sketch, "E338", {"start": v(-124.44, -147.63) * mm, "end": v(-123.33, -148) * mm});
            skLineSegment(sketch, "E339", {"start": v(-123.33, -148) * mm, "end": v(-122.22, -148.36) * mm});
            skLineSegment(sketch, "E340", {"start": v(-122.22, -148.36) * mm, "end": v(-121.11, -148.73) * mm});
            skLineSegment(sketch, "E341", {"start": v(-121.11, -148.73) * mm, "end": v(-120, -149.1) * mm});
            skLineSegment(sketch, "E342", {"start": v(-120, -149.1) * mm, "end": v(-118.89, -149.45) * mm});
            skLineSegment(sketch, "E343", {"start": v(-118.89, -149.45) * mm, "end": v(-117.78, -149.8) * mm});
            skLineSegment(sketch, "E344", {"start": v(-117.78, -149.8) * mm, "end": v(-116.67, -150.15) * mm});
            skLineSegment(sketch, "E345", {"start": v(-116.67, -150.15) * mm, "end": v(-115.56, -150.5) * mm});
            skLineSegment(sketch, "E346", {"start": v(-115.56, -150.5) * mm, "end": v(-114.44, -150.85) * mm});
            skLineSegment(sketch, "E347", {"start": v(-114.44, -150.85) * mm, "end": v(-113.33, -151.19) * mm});
            skLineSegment(sketch, "E348", {"start": v(-113.33, -151.19) * mm, "end": v(-112.22, -151.53) * mm});
            skLineSegment(sketch, "E349", {"start": v(-112.22, -151.53) * mm, "end": v(-111.11, -151.86) * mm});
            skLineSegment(sketch, "E350", {"start": v(-111.11, -151.86) * mm, "end": v(-110, -152.2) * mm});
            skLineSegment(sketch, "E351", {"start": v(-110, -152.2) * mm, "end": v(-108.89, -152.52) * mm});
            skLineSegment(sketch, "E352", {"start": v(-108.89, -152.52) * mm, "end": v(-107.78, -152.84) * mm});
            skLineSegment(sketch, "E353", {"start": v(-107.78, -152.84) * mm, "end": v(-106.67, -153.16) * mm});
            skLineSegment(sketch, "E354", {"start": v(-106.67, -153.16) * mm, "end": v(-105.56, -153.48) * mm});
            skLineSegment(sketch, "E355", {"start": v(-105.56, -153.48) * mm, "end": v(-104.44, -153.8) * mm});
            skLineSegment(sketch, "E356", {"start": v(-104.44, -153.8) * mm, "end": v(-103.33, -154.1) * mm});
            skLineSegment(sketch, "E357", {"start": v(-103.33, -154.1) * mm, "end": v(-102.22, -154.42) * mm});
            skLineSegment(sketch, "E358", {"start": v(-102.22, -154.42) * mm, "end": v(-101.11, -154.72) * mm});
            skLineSegment(sketch, "E359", {"start": v(-101.11, -154.72) * mm, "end": v(-100, -155.02) * mm});
            skLineSegment(sketch, "E360", {"start": v(-100, -155.02) * mm, "end": v(-98.89, -155.32) * mm});
            skLineSegment(sketch, "E361", {"start": v(-98.89, -155.32) * mm, "end": v(-97.78, -155.61) * mm});
            skLineSegment(sketch, "E362", {"start": v(-97.78, -155.61) * mm, "end": v(-96.67, -155.9) * mm});
            skLineSegment(sketch, "E363", {"start": v(-96.67, -155.9) * mm, "end": v(-95.56, -156.2) * mm});
            skLineSegment(sketch, "E364", {"start": v(-95.56, -156.2) * mm, "end": v(-94.44, -156.48) * mm});
            skLineSegment(sketch, "E365", {"start": v(-94.44, -156.48) * mm, "end": v(-93.33, -156.76) * mm});
            skLineSegment(sketch, "E366", {"start": v(-93.33, -156.76) * mm, "end": v(-92.22, -157.04) * mm});
            skLineSegment(sketch, "E367", {"start": v(-92.22, -157.04) * mm, "end": v(-91.11, -157.31) * mm});
            skLineSegment(sketch, "E368", {"start": v(-91.11, -157.31) * mm, "end": v(-90, -157.58) * mm});
            skLineSegment(sketch, "E369", {"start": v(-90, -157.58) * mm, "end": v(-88.89, -157.85) * mm});
            skLineSegment(sketch, "E370", {"start": v(-88.89, -157.85) * mm, "end": v(-87.78, -158.12) * mm});
            skLineSegment(sketch, "E371", {"start": v(-87.78, -158.12) * mm, "end": v(-86.67, -158.38) * mm});
            skLineSegment(sketch, "E372", {"start": v(-86.67, -158.38) * mm, "end": v(-85.56, -158.63) * mm});
            skLineSegment(sketch, "E373", {"start": v(-85.56, -158.63) * mm, "end": v(-84.44, -158.89) * mm});
            skLineSegment(sketch, "E374", {"start": v(-84.44, -158.89) * mm, "end": v(-83.33, -159.14) * mm});
            skLineSegment(sketch, "E375", {"start": v(-83.33, -159.14) * mm, "end": v(-82.22, -159.39) * mm});
            skLineSegment(sketch, "E376", {"start": v(-82.22, -159.39) * mm, "end": v(-81.11, -159.63) * mm});
            skLineSegment(sketch, "E377", {"start": v(-81.11, -159.63) * mm, "end": v(-80, -159.87) * mm});
            skLineSegment(sketch, "E378", {"start": v(-80, -159.87) * mm, "end": v(-78.89, -160.11) * mm});
            skLineSegment(sketch, "E379", {"start": v(-78.89, -160.11) * mm, "end": v(-77.78, -160.35) * mm});
            skLineSegment(sketch, "E380", {"start": v(-77.78, -160.35) * mm, "end": v(-76.67, -160.58) * mm});
            skLineSegment(sketch, "E381", {"start": v(-76.67, -160.58) * mm, "end": v(-75.56, -160.8) * mm});
            skLineSegment(sketch, "E382", {"start": v(-75.56, -160.8) * mm, "end": v(-74.44, -161.03) * mm});
            skLineSegment(sketch, "E383", {"start": v(-74.44, -161.03) * mm, "end": v(-73.33, -161.25) * mm});
            skLineSegment(sketch, "E384", {"start": v(-73.33, -161.25) * mm, "end": v(-72.22, -161.47) * mm});
            skLineSegment(sketch, "E385", {"start": v(-72.22, -161.47) * mm, "end": v(-71.11, -161.69) * mm});
            skLineSegment(sketch, "E386", {"start": v(-71.11, -161.69) * mm, "end": v(-70, -161.9) * mm});
            skLineSegment(sketch, "E387", {"start": v(-70, -161.9) * mm, "end": v(-68.89, -162.1) * mm});
            skLineSegment(sketch, "E388", {"start": v(-68.89, -162.1) * mm, "end": v(-67.78, -162.3) * mm});
            skLineSegment(sketch, "E389", {"start": v(-67.78, -162.3) * mm, "end": v(-66.67, -162.51) * mm});
            skLineSegment(sketch, "E390", {"start": v(-66.67, -162.51) * mm, "end": v(-65.56, -162.7) * mm});
            skLineSegment(sketch, "E391", {"start": v(-65.56, -162.7) * mm, "end": v(-64.44, -162.9) * mm});
            skLineSegment(sketch, "E392", {"start": v(-64.44, -162.9) * mm, "end": v(-63.33, -163.1) * mm});
            skLineSegment(sketch, "E393", {"start": v(-63.33, -163.1) * mm, "end": v(-62.22, -163.28) * mm});
            skLineSegment(sketch, "E394", {"start": v(-62.22, -163.28) * mm, "end": v(-61.11, -163.47) * mm});
            skLineSegment(sketch, "E395", {"start": v(-61.11, -163.47) * mm, "end": v(-60, -163.65) * mm});
            skLineSegment(sketch, "E396", {"start": v(-60, -163.65) * mm, "end": v(-58.89, -163.83) * mm});
            skLineSegment(sketch, "E397", {"start": v(-58.89, -163.83) * mm, "end": v(-57.78, -164) * mm});
            skLineSegment(sketch, "E398", {"start": v(-57.78, -164) * mm, "end": v(-56.67, -164.17) * mm});
            skLineSegment(sketch, "E399", {"start": v(-56.67, -164.17) * mm, "end": v(-55.56, -164.34) * mm});
            skLineSegment(sketch, "E400", {"start": v(-55.56, -164.34) * mm, "end": v(-54.44, -164.5) * mm});
            skLineSegment(sketch, "E401", {"start": v(-54.44, -164.5) * mm, "end": v(-53.33, -164.67) * mm});
            skLineSegment(sketch, "E402", {"start": v(-53.33, -164.67) * mm, "end": v(-52.22, -164.83) * mm});
            skLineSegment(sketch, "E403", {"start": v(-52.22, -164.83) * mm, "end": v(-51.11, -164.98) * mm});
            skLineSegment(sketch, "E404", {"start": v(-51.11, -164.98) * mm, "end": v(-50, -165.13) * mm});
            skLineSegment(sketch, "E405", {"start": v(-50, -165.13) * mm, "end": v(-48.89, -165.28) * mm});
            skLineSegment(sketch, "E406", {"start": v(-48.89, -165.28) * mm, "end": v(-47.78, -165.42) * mm});
            skLineSegment(sketch, "E407", {"start": v(-47.78, -165.42) * mm, "end": v(-46.67, -165.57) * mm});
            skLineSegment(sketch, "E408", {"start": v(-46.67, -165.57) * mm, "end": v(-45.56, -165.7) * mm});
            skLineSegment(sketch, "E409", {"start": v(-45.56, -165.7) * mm, "end": v(-44.44, -165.84) * mm});
            skLineSegment(sketch, "E410", {"start": v(-44.44, -165.84) * mm, "end": v(-43.33, -165.97) * mm});
            skLineSegment(sketch, "E411", {"start": v(-43.33, -165.97) * mm, "end": v(-42.22, -166.1) * mm});
            skLineSegment(sketch, "E412", {"start": v(-42.22, -166.1) * mm, "end": v(-41.11, -166.22) * mm});
            skLineSegment(sketch, "E413", {"start": v(-41.11, -166.22) * mm, "end": v(-40, -166.34) * mm});
            skLineSegment(sketch, "E414", {"start": v(-40, -166.34) * mm, "end": v(-38.89, -166.46) * mm});
            skLineSegment(sketch, "E415", {"start": v(-38.89, -166.46) * mm, "end": v(-37.78, -166.58) * mm});
            skLineSegment(sketch, "E416", {"start": v(-37.78, -166.58) * mm, "end": v(-36.67, -166.69) * mm});
            skLineSegment(sketch, "E417", {"start": v(-36.67, -166.69) * mm, "end": v(-35.56, -166.8) * mm});
            skLineSegment(sketch, "E418", {"start": v(-35.56, -166.8) * mm, "end": v(-34.44, -166.9) * mm});
            skLineSegment(sketch, "E419", {"start": v(-34.44, -166.9) * mm, "end": v(-33.33, -167) * mm});
            skLineSegment(sketch, "E420", {"start": v(-33.33, -167) * mm, "end": v(-32.22, -167.1) * mm});
            skLineSegment(sketch, "E421", {"start": v(-32.22, -167.1) * mm, "end": v(-31.11, -167.2) * mm});
            skLineSegment(sketch, "E422", {"start": v(-31.11, -167.2) * mm, "end": v(-30, -167.29) * mm});
            skLineSegment(sketch, "E423", {"start": v(-30, -167.29) * mm, "end": v(-28.89, -167.38) * mm});
            skLineSegment(sketch, "E424", {"start": v(-28.89, -167.38) * mm, "end": v(-27.78, -167.46) * mm});
            skLineSegment(sketch, "E425", {"start": v(-27.78, -167.46) * mm, "end": v(-26.67, -167.54) * mm});
            skLineSegment(sketch, "E426", {"start": v(-26.67, -167.54) * mm, "end": v(-25.56, -167.62) * mm});
            skLineSegment(sketch, "E427", {"start": v(-25.56, -167.62) * mm, "end": v(-24.44, -167.7) * mm});
            skLineSegment(sketch, "E428", {"start": v(-24.44, -167.7) * mm, "end": v(-23.33, -167.77) * mm});
            skLineSegment(sketch, "E429", {"start": v(-23.33, -167.77) * mm, "end": v(-22.22, -167.84) * mm});
            skLineSegment(sketch, "E430", {"start": v(-22.22, -167.84) * mm, "end": v(-21.11, -167.9) * mm});
            skLineSegment(sketch, "E431", {"start": v(-21.11, -167.9) * mm, "end": v(-20, -167.96) * mm});
            skLineSegment(sketch, "E432", {"start": v(-20, -167.96) * mm, "end": v(-18.89, -168.02) * mm});
            skLineSegment(sketch, "E433", {"start": v(-18.89, -168.02) * mm, "end": v(-17.78, -168.08) * mm});
            skLineSegment(sketch, "E434", {"start": v(-17.78, -168.08) * mm, "end": v(-16.67, -168.13) * mm});
            skLineSegment(sketch, "E435", {"start": v(-16.67, -168.13) * mm, "end": v(-15.56, -168.18) * mm});
            skLineSegment(sketch, "E436", {"start": v(-15.56, -168.18) * mm, "end": v(-14.44, -168.22) * mm});
            skLineSegment(sketch, "E437", {"start": v(-14.44, -168.22) * mm, "end": v(-13.33, -168.26) * mm});
            skLineSegment(sketch, "E438", {"start": v(-13.33, -168.26) * mm, "end": v(-12.22, -168.3) * mm});
            skLineSegment(sketch, "E439", {"start": v(-12.22, -168.3) * mm, "end": v(-11.11, -168.33) * mm});
            skLineSegment(sketch, "E440", {"start": v(-11.11, -168.33) * mm, "end": v(-10, -168.37) * mm});
            skLineSegment(sketch, "E441", {"start": v(-10, -168.37) * mm, "end": v(-8.89, -168.4) * mm});
            skLineSegment(sketch, "E442", {"start": v(-8.89, -168.4) * mm, "end": v(-7.78, -168.42) * mm});
            skLineSegment(sketch, "E443", {"start": v(-7.78, -168.42) * mm, "end": v(-6.67, -168.44) * mm});
            skLineSegment(sketch, "E444", {"start": v(-6.67, -168.44) * mm, "end": v(-5.56, -168.46) * mm});
            skLineSegment(sketch, "E445", {"start": v(-5.56, -168.46) * mm, "end": v(-4.44, -168.47) * mm});
            skLineSegment(sketch, "E446", {"start": v(-4.44, -168.47) * mm, "end": v(-3.33, -168.49) * mm});
            skLineSegment(sketch, "E447", {"start": v(-3.33, -168.49) * mm, "end": v(-2.22, -168.5) * mm});
            skLineSegment(sketch, "E448", {"start": v(-2.22, -168.5) * mm, "end": v(-1.11, -168.5) * mm});
            skLineSegment(sketch, "E449", {"start": v(-1.11, -168.5) * mm, "end": v(0, -168.5) * mm});
            skLineSegment(sketch, "E450", {"start": v(0, -168.5) * mm, "end": v(1.11, -168.5) * mm});
            skLineSegment(sketch, "E451", {"start": v(1.11, -168.5) * mm, "end": v(2.22, -168.5) * mm});
            skLineSegment(sketch, "E452", {"start": v(2.22, -168.5) * mm, "end": v(3.33, -168.49) * mm});
            skLineSegment(sketch, "E453", {"start": v(3.33, -168.49) * mm, "end": v(4.44, -168.47) * mm});
            skLineSegment(sketch, "E454", {"start": v(4.44, -168.47) * mm, "end": v(5.56, -168.46) * mm});
            skLineSegment(sketch, "E455", {"start": v(5.56, -168.46) * mm, "end": v(6.67, -168.44) * mm});
            skLineSegment(sketch, "E456", {"start": v(6.67, -168.44) * mm, "end": v(7.78, -168.42) * mm});
            skLineSegment(sketch, "E457", {"start": v(7.78, -168.42) * mm, "end": v(8.89, -168.4) * mm});
            skLineSegment(sketch, "E458", {"start": v(8.89, -168.4) * mm, "end": v(10, -168.37) * mm});
            skLineSegment(sketch, "E459", {"start": v(10, -168.37) * mm, "end": v(11.11, -168.33) * mm});
            skLineSegment(sketch, "E460", {"start": v(11.11, -168.33) * mm, "end": v(12.22, -168.3) * mm});
            skLineSegment(sketch, "E461", {"start": v(12.22, -168.3) * mm, "end": v(13.33, -168.26) * mm});
            skLineSegment(sketch, "E462", {"start": v(13.33, -168.26) * mm, "end": v(14.44, -168.22) * mm});
            skLineSegment(sketch, "E463", {"start": v(14.44, -168.22) * mm, "end": v(15.56, -168.18) * mm});
            skLineSegment(sketch, "E464", {"start": v(15.56, -168.18) * mm, "end": v(16.67, -168.13) * mm});
            skLineSegment(sketch, "E465", {"start": v(16.67, -168.13) * mm, "end": v(17.78, -168.08) * mm});
            skLineSegment(sketch, "E466", {"start": v(17.78, -168.08) * mm, "end": v(18.89, -168.02) * mm});
            skLineSegment(sketch, "E467", {"start": v(18.89, -168.02) * mm, "end": v(20, -167.96) * mm});
            skLineSegment(sketch, "E468", {"start": v(20, -167.96) * mm, "end": v(21.11, -167.9) * mm});
            skLineSegment(sketch, "E469", {"start": v(21.11, -167.9) * mm, "end": v(22.22, -167.84) * mm});
            skLineSegment(sketch, "E470", {"start": v(22.22, -167.84) * mm, "end": v(23.33, -167.77) * mm});
            skLineSegment(sketch, "E471", {"start": v(23.33, -167.77) * mm, "end": v(24.44, -167.7) * mm});
            skLineSegment(sketch, "E472", {"start": v(24.44, -167.7) * mm, "end": v(25.56, -167.62) * mm});
            skLineSegment(sketch, "E473", {"start": v(25.56, -167.62) * mm, "end": v(26.67, -167.54) * mm});
            skLineSegment(sketch, "E474", {"start": v(26.67, -167.54) * mm, "end": v(27.78, -167.46) * mm});
            skLineSegment(sketch, "E475", {"start": v(27.78, -167.46) * mm, "end": v(28.89, -167.38) * mm});
            skLineSegment(sketch, "E476", {"start": v(28.89, -167.38) * mm, "end": v(30, -167.29) * mm});
            skLineSegment(sketch, "E477", {"start": v(30, -167.29) * mm, "end": v(31.11, -167.2) * mm});
            skLineSegment(sketch, "E478", {"start": v(31.11, -167.2) * mm, "end": v(32.22, -167.1) * mm});
            skLineSegment(sketch, "E479", {"start": v(32.22, -167.1) * mm, "end": v(33.33, -167) * mm});
            skLineSegment(sketch, "E480", {"start": v(33.33, -167) * mm, "end": v(34.44, -166.9) * mm});
            skLineSegment(sketch, "E481", {"start": v(34.44, -166.9) * mm, "end": v(35.56, -166.8) * mm});
            skLineSegment(sketch, "E482", {"start": v(35.56, -166.8) * mm, "end": v(36.67, -166.69) * mm});
            skLineSegment(sketch, "E483", {"start": v(36.67, -166.69) * mm, "end": v(37.78, -166.58) * mm});
            skLineSegment(sketch, "E484", {"start": v(37.78, -166.58) * mm, "end": v(38.89, -166.46) * mm});
            skLineSegment(sketch, "E485", {"start": v(38.89, -166.46) * mm, "end": v(40, -166.34) * mm});
            skLineSegment(sketch, "E486", {"start": v(40, -166.34) * mm, "end": v(41.11, -166.22) * mm});
            skLineSegment(sketch, "E487", {"start": v(41.11, -166.22) * mm, "end": v(42.22, -166.1) * mm});
            skLineSegment(sketch, "E488", {"start": v(42.22, -166.1) * mm, "end": v(43.33, -165.97) * mm});
            skLineSegment(sketch, "E489", {"start": v(43.33, -165.97) * mm, "end": v(44.44, -165.84) * mm});
            skLineSegment(sketch, "E490", {"start": v(44.44, -165.84) * mm, "end": v(45.56, -165.7) * mm});
            skLineSegment(sketch, "E491", {"start": v(45.56, -165.7) * mm, "end": v(46.67, -165.57) * mm});
            skLineSegment(sketch, "E492", {"start": v(46.67, -165.57) * mm, "end": v(47.78, -165.42) * mm});
            skLineSegment(sketch, "E493", {"start": v(47.78, -165.42) * mm, "end": v(48.89, -165.28) * mm});
            skLineSegment(sketch, "E494", {"start": v(48.89, -165.28) * mm, "end": v(50, -165.13) * mm});
            skLineSegment(sketch, "E495", {"start": v(50, -165.13) * mm, "end": v(51.11, -164.98) * mm});
            skLineSegment(sketch, "E496", {"start": v(51.11, -164.98) * mm, "end": v(52.22, -164.82) * mm});
            skLineSegment(sketch, "E497", {"start": v(52.22, -164.82) * mm, "end": v(53.33, -164.67) * mm});
            skLineSegment(sketch, "E498", {"start": v(53.33, -164.67) * mm, "end": v(54.44, -164.5) * mm});
            skLineSegment(sketch, "E499", {"start": v(54.44, -164.5) * mm, "end": v(55.56, -164.34) * mm});
            skLineSegment(sketch, "E500", {"start": v(55.56, -164.34) * mm, "end": v(56.67, -164.17) * mm});
            skLineSegment(sketch, "E501", {"start": v(56.67, -164.17) * mm, "end": v(57.78, -164) * mm});
            skLineSegment(sketch, "E502", {"start": v(57.78, -164) * mm, "end": v(58.89, -163.83) * mm});
            skLineSegment(sketch, "E503", {"start": v(58.89, -163.83) * mm, "end": v(60, -163.65) * mm});
            skLineSegment(sketch, "E504", {"start": v(60, -163.65) * mm, "end": v(61.11, -163.47) * mm});
            skLineSegment(sketch, "E505", {"start": v(61.11, -163.47) * mm, "end": v(62.22, -163.28) * mm});
            skLineSegment(sketch, "E506", {"start": v(62.22, -163.28) * mm, "end": v(63.33, -163.1) * mm});
            skLineSegment(sketch, "E507", {"start": v(63.33, -163.1) * mm, "end": v(64.44, -162.9) * mm});
            skLineSegment(sketch, "E508", {"start": v(64.44, -162.9) * mm, "end": v(65.56, -162.7) * mm});
            skLineSegment(sketch, "E509", {"start": v(65.56, -162.7) * mm, "end": v(66.67, -162.5) * mm});
            skLineSegment(sketch, "E510", {"start": v(66.67, -162.5) * mm, "end": v(67.78, -162.3) * mm});
            skLineSegment(sketch, "E511", {"start": v(67.78, -162.3) * mm, "end": v(68.89, -162.1) * mm});
            skLineSegment(sketch, "E512", {"start": v(68.89, -162.1) * mm, "end": v(70, -161.9) * mm});
            skLineSegment(sketch, "E513", {"start": v(70, -161.9) * mm, "end": v(71.11, -161.68) * mm});
            skLineSegment(sketch, "E514", {"start": v(71.11, -161.68) * mm, "end": v(72.22, -161.47) * mm});
            skLineSegment(sketch, "E515", {"start": v(72.22, -161.47) * mm, "end": v(73.33, -161.25) * mm});
            skLineSegment(sketch, "E516", {"start": v(73.33, -161.25) * mm, "end": v(74.44, -161.03) * mm});
            skLineSegment(sketch, "E517", {"start": v(74.44, -161.03) * mm, "end": v(75.56, -160.8) * mm});
            skLineSegment(sketch, "E518", {"start": v(75.56, -160.8) * mm, "end": v(76.67, -160.58) * mm});
            skLineSegment(sketch, "E519", {"start": v(76.67, -160.58) * mm, "end": v(77.78, -160.35) * mm});
            skLineSegment(sketch, "E520", {"start": v(77.78, -160.35) * mm, "end": v(78.89, -160.11) * mm});
            skLineSegment(sketch, "E521", {"start": v(78.89, -160.11) * mm, "end": v(80, -159.87) * mm});
            skLineSegment(sketch, "E522", {"start": v(80, -159.87) * mm, "end": v(81.11, -159.63) * mm});
            skLineSegment(sketch, "E523", {"start": v(81.11, -159.63) * mm, "end": v(82.22, -159.39) * mm});
            skLineSegment(sketch, "E524", {"start": v(82.22, -159.39) * mm, "end": v(83.33, -159.14) * mm});
            skLineSegment(sketch, "E525", {"start": v(83.33, -159.14) * mm, "end": v(84.44, -158.89) * mm});
            skLineSegment(sketch, "E526", {"start": v(84.44, -158.89) * mm, "end": v(85.56, -158.63) * mm});
            skLineSegment(sketch, "E527", {"start": v(85.56, -158.63) * mm, "end": v(86.67, -158.38) * mm});
            skLineSegment(sketch, "E528", {"start": v(86.67, -158.38) * mm, "end": v(87.78, -158.11) * mm});
            skLineSegment(sketch, "E529", {"start": v(87.78, -158.11) * mm, "end": v(88.89, -157.85) * mm});
            skLineSegment(sketch, "E530", {"start": v(88.89, -157.85) * mm, "end": v(90, -157.58) * mm});
            skLineSegment(sketch, "E531", {"start": v(90, -157.58) * mm, "end": v(91.11, -157.31) * mm});
            skLineSegment(sketch, "E532", {"start": v(91.11, -157.31) * mm, "end": v(92.22, -157.04) * mm});
            skLineSegment(sketch, "E533", {"start": v(92.22, -157.04) * mm, "end": v(93.33, -156.76) * mm});
            skLineSegment(sketch, "E534", {"start": v(93.33, -156.76) * mm, "end": v(94.44, -156.48) * mm});
            skLineSegment(sketch, "E535", {"start": v(94.44, -156.48) * mm, "end": v(95.56, -156.2) * mm});
            skLineSegment(sketch, "E536", {"start": v(95.56, -156.2) * mm, "end": v(96.67, -155.9) * mm});
            skLineSegment(sketch, "E537", {"start": v(96.67, -155.9) * mm, "end": v(97.78, -155.61) * mm});
            skLineSegment(sketch, "E538", {"start": v(97.78, -155.61) * mm, "end": v(98.89, -155.32) * mm});
            skLineSegment(sketch, "E539", {"start": v(98.89, -155.32) * mm, "end": v(100, -155.02) * mm});
            skLineSegment(sketch, "E540", {"start": v(100, -155.02) * mm, "end": v(101.11, -154.72) * mm});
            skLineSegment(sketch, "E541", {"start": v(101.11, -154.72) * mm, "end": v(102.22, -154.42) * mm});
            skLineSegment(sketch, "E542", {"start": v(102.22, -154.42) * mm, "end": v(103.33, -154.1) * mm});
            skLineSegment(sketch, "E543", {"start": v(103.33, -154.1) * mm, "end": v(104.44, -153.8) * mm});
            skLineSegment(sketch, "E544", {"start": v(104.44, -153.8) * mm, "end": v(105.56, -153.48) * mm});
            skLineSegment(sketch, "E545", {"start": v(105.56, -153.48) * mm, "end": v(106.67, -153.16) * mm});
            skLineSegment(sketch, "E546", {"start": v(106.67, -153.16) * mm, "end": v(107.78, -152.84) * mm});
            skLineSegment(sketch, "E547", {"start": v(107.78, -152.84) * mm, "end": v(108.89, -152.52) * mm});
            skLineSegment(sketch, "E548", {"start": v(108.89, -152.52) * mm, "end": v(110, -152.2) * mm});
            skLineSegment(sketch, "E549", {"start": v(110, -152.2) * mm, "end": v(111.11, -151.86) * mm});
            skLineSegment(sketch, "E550", {"start": v(111.11, -151.86) * mm, "end": v(112.22, -151.52) * mm});
            skLineSegment(sketch, "E551", {"start": v(112.22, -151.52) * mm, "end": v(113.33, -151.19) * mm});
            skLineSegment(sketch, "E552", {"start": v(113.33, -151.19) * mm, "end": v(114.44, -150.85) * mm});
            skLineSegment(sketch, "E553", {"start": v(114.44, -150.85) * mm, "end": v(115.56, -150.5) * mm});
            skLineSegment(sketch, "E554", {"start": v(115.56, -150.5) * mm, "end": v(116.67, -150.15) * mm});
            skLineSegment(sketch, "E555", {"start": v(116.67, -150.15) * mm, "end": v(117.78, -149.8) * mm});
            skLineSegment(sketch, "E556", {"start": v(117.78, -149.8) * mm, "end": v(118.89, -149.45) * mm});
            skLineSegment(sketch, "E557", {"start": v(118.89, -149.45) * mm, "end": v(120, -149.09) * mm});
            skLineSegment(sketch, "E558", {"start": v(120, -149.09) * mm, "end": v(121.11, -148.73) * mm});
            skLineSegment(sketch, "E559", {"start": v(121.11, -148.73) * mm, "end": v(122.22, -148.36) * mm});
            skLineSegment(sketch, "E560", {"start": v(122.22, -148.36) * mm, "end": v(123.33, -148) * mm});
            skLineSegment(sketch, "E561", {"start": v(123.33, -148) * mm, "end": v(124.44, -147.63) * mm});
            skLineSegment(sketch, "E562", {"start": v(124.44, -147.63) * mm, "end": v(125.56, -147.25) * mm});
            skLineSegment(sketch, "E563", {"start": v(125.56, -147.25) * mm, "end": v(126.67, -146.87) * mm});
            skLineSegment(sketch, "E564", {"start": v(126.67, -146.87) * mm, "end": v(127.78, -146.5) * mm});
            skLineSegment(sketch, "E565", {"start": v(127.78, -146.5) * mm, "end": v(128.89, -146.1) * mm});
            skLineSegment(sketch, "E566", {"start": v(128.89, -146.1) * mm, "end": v(130, -145.72) * mm});
            skLineSegment(sketch, "E567", {"start": v(130, -145.72) * mm, "end": v(131.11, -145.33) * mm});
            skLineSegment(sketch, "E568", {"start": v(131.11, -145.33) * mm, "end": v(132.22, -144.93) * mm});
            skLineSegment(sketch, "E569", {"start": v(132.22, -144.93) * mm, "end": v(133.33, -144.54) * mm});
            skLineSegment(sketch, "E570", {"start": v(133.33, -144.54) * mm, "end": v(134.44, -144.14) * mm});
            skLineSegment(sketch, "E571", {"start": v(134.44, -144.14) * mm, "end": v(135.56, -143.73) * mm});
            skLineSegment(sketch, "E572", {"start": v(135.56, -143.73) * mm, "end": v(136.67, -143.32) * mm});
            skLineSegment(sketch, "E573", {"start": v(136.67, -143.32) * mm, "end": v(137.78, -142.91) * mm});
            skLineSegment(sketch, "E574", {"start": v(137.78, -142.91) * mm, "end": v(138.89, -142.5) * mm});
            skLineSegment(sketch, "E575", {"start": v(138.89, -142.5) * mm, "end": v(140, -142.08) * mm});
            skLineSegment(sketch, "E576", {"start": v(140, -142.08) * mm, "end": v(141.11, -141.66) * mm});
            skLineSegment(sketch, "E577", {"start": v(141.11, -141.66) * mm, "end": v(142.22, -141.23) * mm});
            skLineSegment(sketch, "E578", {"start": v(142.22, -141.23) * mm, "end": v(143.33, -140.8) * mm});
            skLineSegment(sketch, "E579", {"start": v(143.33, -140.8) * mm, "end": v(144.44, -140.38) * mm});
            skLineSegment(sketch, "E580", {"start": v(144.44, -140.38) * mm, "end": v(145.56, -139.94) * mm});
            skLineSegment(sketch, "E581", {"start": v(145.56, -139.94) * mm, "end": v(146.67, -139.5) * mm});
            skLineSegment(sketch, "E582", {"start": v(146.67, -139.5) * mm, "end": v(147.78, -139.06) * mm});
            skLineSegment(sketch, "E583", {"start": v(147.78, -139.06) * mm, "end": v(148.89, -138.62) * mm});
            skLineSegment(sketch, "E584", {"start": v(148.89, -138.62) * mm, "end": v(150, -138.17) * mm});
            skLineSegment(sketch, "E585", {"start": v(150, -138.17) * mm, "end": v(151.11, -137.72) * mm});
            skLineSegment(sketch, "E586", {"start": v(151.11, -137.72) * mm, "end": v(152.22, -137.27) * mm});
            skLineSegment(sketch, "E587", {"start": v(152.22, -137.27) * mm, "end": v(153.33, -136.8) * mm});
            skLineSegment(sketch, "E588", {"start": v(153.33, -136.8) * mm, "end": v(154.44, -136.35) * mm});
            skLineSegment(sketch, "E589", {"start": v(154.44, -136.35) * mm, "end": v(155.56, -135.88) * mm});
            skLineSegment(sketch, "E590", {"start": v(155.56, -135.88) * mm, "end": v(156.67, -135.41) * mm});
            skLineSegment(sketch, "E591", {"start": v(156.67, -135.41) * mm, "end": v(157.78, -134.94) * mm});
            skLineSegment(sketch, "E592", {"start": v(157.78, -134.94) * mm, "end": v(158.89, -134.47) * mm});
            skLineSegment(sketch, "E593", {"start": v(158.89, -134.47) * mm, "end": v(160, -134) * mm});
            skLineSegment(sketch, "E594", {"start": v(160, -134) * mm, "end": v(161.11, -133.51) * mm});
            skLineSegment(sketch, "E595", {"start": v(161.11, -133.51) * mm, "end": v(162.22, -133.03) * mm});
            skLineSegment(sketch, "E596", {"start": v(162.22, -133.03) * mm, "end": v(163.33, -132.54) * mm});
            skLineSegment(sketch, "E597", {"start": v(163.33, -132.54) * mm, "end": v(164.44, -132.05) * mm});
            skLineSegment(sketch, "E598", {"start": v(164.44, -132.05) * mm, "end": v(165.56, -131.55) * mm});
            skLineSegment(sketch, "E599", {"start": v(165.56, -131.55) * mm, "end": v(166.67, -131.06) * mm});
            skLineSegment(sketch, "E600", {"start": v(166.67, -131.06) * mm, "end": v(167.78, -130.56) * mm});
            skLineSegment(sketch, "E601", {"start": v(167.78, -130.56) * mm, "end": v(168.89, -130.05) * mm});
            skLineSegment(sketch, "E602", {"start": v(168.89, -130.05) * mm, "end": v(170, -129.54) * mm});
            skLineSegment(sketch, "E603", {"start": v(170, -129.54) * mm, "end": v(171.11, -129.03) * mm});
            skLineSegment(sketch, "E604", {"start": v(171.11, -129.03) * mm, "end": v(172.22, -128.52) * mm});
            skLineSegment(sketch, "E605", {"start": v(172.22, -128.52) * mm, "end": v(173.33, -128) * mm});
            skLineSegment(sketch, "E606", {"start": v(173.33, -128) * mm, "end": v(174.44, -127.48) * mm});
            skLineSegment(sketch, "E607", {"start": v(174.44, -127.48) * mm, "end": v(175.56, -126.96) * mm});
            skLineSegment(sketch, "E608", {"start": v(175.56, -126.96) * mm, "end": v(176.67, -126.43) * mm});
            skLineSegment(sketch, "E609", {"start": v(176.67, -126.43) * mm, "end": v(177.78, -125.9) * mm});
            skLineSegment(sketch, "E610", {"start": v(177.78, -125.9) * mm, "end": v(178.89, -125.36) * mm});
            skLineSegment(sketch, "E611", {"start": v(178.89, -125.36) * mm, "end": v(180, -124.83) * mm});
            skLineSegment(sketch, "E612", {"start": v(180, -124.83) * mm, "end": v(181.11, -124.28) * mm});
            skLineSegment(sketch, "E613", {"start": v(181.11, -124.28) * mm, "end": v(182.22, -123.74) * mm});
            skLineSegment(sketch, "E614", {"start": v(182.22, -123.74) * mm, "end": v(183.33, -123.2) * mm});
            skLineSegment(sketch, "E615", {"start": v(183.33, -123.2) * mm, "end": v(184.44, -122.64) * mm});
            skLineSegment(sketch, "E616", {"start": v(184.44, -122.64) * mm, "end": v(185.56, -122.09) * mm});
            skLineSegment(sketch, "E617", {"start": v(185.56, -122.09) * mm, "end": v(186.67, -121.53) * mm});
            skLineSegment(sketch, "E618", {"start": v(186.67, -121.53) * mm, "end": v(187.78, -120.97) * mm});
            skLineSegment(sketch, "E619", {"start": v(187.78, -120.97) * mm, "end": v(188.89, -120.4) * mm});
            skLineSegment(sketch, "E620", {"start": v(188.89, -120.4) * mm, "end": v(190, -119.84) * mm});
            skLineSegment(sketch, "E621", {"start": v(190, -119.84) * mm, "end": v(191.11, -119.27) * mm});
            skLineSegment(sketch, "E622", {"start": v(191.11, -119.27) * mm, "end": v(192.22, -118.7) * mm});
            skLineSegment(sketch, "E623", {"start": v(192.22, -118.7) * mm, "end": v(193.33, -118.12) * mm});
            skLineSegment(sketch, "E624", {"start": v(193.33, -118.12) * mm, "end": v(194.44, -117.53) * mm});
            skLineSegment(sketch, "E625", {"start": v(194.44, -117.53) * mm, "end": v(195.56, -116.95) * mm});
            skLineSegment(sketch, "E626", {"start": v(195.56, -116.95) * mm, "end": v(196.67, -116.36) * mm});
            skLineSegment(sketch, "E627", {"start": v(196.67, -116.36) * mm, "end": v(197.78, -115.77) * mm});
            skLineSegment(sketch, "E628", {"start": v(197.78, -115.77) * mm, "end": v(198.89, -115.18) * mm});
            skLineSegment(sketch, "E629", {"start": v(198.89, -115.18) * mm, "end": v(200, -114.58) * mm});
            skLineSegment(sketch, "E630", {"start": v(200, -114.58) * mm, "end": v(201.11, -113.98) * mm});
            skLineSegment(sketch, "E631", {"start": v(201.11, -113.98) * mm, "end": v(202.22, -113.38) * mm});
            skLineSegment(sketch, "E632", {"start": v(202.22, -113.38) * mm, "end": v(203.33, -112.77) * mm});
            skLineSegment(sketch, "E633", {"start": v(203.33, -112.77) * mm, "end": v(204.44, -112.16) * mm});
            skLineSegment(sketch, "E634", {"start": v(204.44, -112.16) * mm, "end": v(205.56, -111.54) * mm});
            skLineSegment(sketch, "E635", {"start": v(205.56, -111.54) * mm, "end": v(206.67, -110.93) * mm});
            skLineSegment(sketch, "E636", {"start": v(206.67, -110.93) * mm, "end": v(207.78, -110.3) * mm});
            skLineSegment(sketch, "E637", {"start": v(207.78, -110.3) * mm, "end": v(208.89, -109.68) * mm});
            skLineSegment(sketch, "E638", {"start": v(208.89, -109.68) * mm, "end": v(210, -109.05) * mm});
            skLineSegment(sketch, "E639", {"start": v(210, -109.05) * mm, "end": v(211.11, -108.42) * mm});
            skLineSegment(sketch, "E640", {"start": v(211.11, -108.42) * mm, "end": v(212.22, -107.79) * mm});
            skLineSegment(sketch, "E641", {"start": v(212.22, -107.79) * mm, "end": v(213.33, -107.15) * mm});
            skLineSegment(sketch, "E642", {"start": v(213.33, -107.15) * mm, "end": v(214.44, -106.51) * mm});
            skLineSegment(sketch, "E643", {"start": v(214.44, -106.51) * mm, "end": v(215.56, -105.87) * mm});
            skLineSegment(sketch, "E644", {"start": v(215.56, -105.87) * mm, "end": v(216.67, -105.22) * mm});
            skLineSegment(sketch, "E645", {"start": v(216.67, -105.22) * mm, "end": v(217.78, -104.57) * mm});
            skLineSegment(sketch, "E646", {"start": v(217.78, -104.57) * mm, "end": v(218.89, -103.91) * mm});
            skLineSegment(sketch, "E647", {"start": v(218.89, -103.91) * mm, "end": v(220, -103.26) * mm});
            skLineSegment(sketch, "E648", {"start": v(220, -103.26) * mm, "end": v(221.11, -102.6) * mm});
            skLineSegment(sketch, "E649", {"start": v(221.11, -102.6) * mm, "end": v(222.22, -101.93) * mm});
            skLineSegment(sketch, "E650", {"start": v(222.22, -101.93) * mm, "end": v(223.33, -101.27) * mm});
            skLineSegment(sketch, "E651", {"start": v(223.33, -101.27) * mm, "end": v(224.44, -100.6) * mm});
            skLineSegment(sketch, "E652", {"start": v(224.44, -100.6) * mm, "end": v(225.56, -99.92) * mm});
            skLineSegment(sketch, "E653", {"start": v(225.56, -99.92) * mm, "end": v(226.67, -99.24) * mm});
            skLineSegment(sketch, "E654", {"start": v(226.67, -99.24) * mm, "end": v(227.78, -98.56) * mm});
            skLineSegment(sketch, "E655", {"start": v(227.78, -98.56) * mm, "end": v(228.89, -97.88) * mm});
            skLineSegment(sketch, "E656", {"start": v(228.89, -97.88) * mm, "end": v(230, -97.2) * mm});
            skLineSegment(sketch, "E657", {"start": v(230, -97.2) * mm, "end": v(231.11, -96.5) * mm});
            skLineSegment(sketch, "E658", {"start": v(231.11, -96.5) * mm, "end": v(232.22, -95.8) * mm});
            skLineSegment(sketch, "E659", {"start": v(232.22, -95.8) * mm, "end": v(233.33, -95.1) * mm});
            skLineSegment(sketch, "E660", {"start": v(233.33, -95.1) * mm, "end": v(234.44, -94.4) * mm});
            skLineSegment(sketch, "E661", {"start": v(234.44, -94.4) * mm, "end": v(235.56, -93.7) * mm});
            skLineSegment(sketch, "E662", {"start": v(235.56, -93.7) * mm, "end": v(236.67, -93) * mm});
            skLineSegment(sketch, "E663", {"start": v(236.67, -93) * mm, "end": v(237.78, -92.29) * mm});
            skLineSegment(sketch, "E664", {"start": v(237.78, -92.29) * mm, "end": v(238.89, -91.57) * mm});
            skLineSegment(sketch, "E665", {"start": v(238.89, -91.57) * mm, "end": v(240, -90.86) * mm});
            skLineSegment(sketch, "E666", {"start": v(240, -90.86) * mm, "end": v(241.11, -90.13) * mm});
            skLineSegment(sketch, "E667", {"start": v(241.11, -90.13) * mm, "end": v(242.22, -89.41) * mm});
            skLineSegment(sketch, "E668", {"start": v(242.22, -89.41) * mm, "end": v(243.33, -88.68) * mm});
            skLineSegment(sketch, "E669", {"start": v(243.33, -88.68) * mm, "end": v(244.44, -87.95) * mm});
            skLineSegment(sketch, "E670", {"start": v(244.44, -87.95) * mm, "end": v(245.56, -87.22) * mm});
            skLineSegment(sketch, "E671", {"start": v(245.56, -87.22) * mm, "end": v(246.67, -86.48) * mm});
            skLineSegment(sketch, "E672", {"start": v(246.67, -86.48) * mm, "end": v(247.78, -85.74) * mm});
            skLineSegment(sketch, "E673", {"start": v(247.78, -85.74) * mm, "end": v(248.89, -85) * mm});
            skLineSegment(sketch, "E674", {"start": v(248.89, -85) * mm, "end": v(250, -84.25) * mm});
            skLineSegment(sketch, "E675", {"start": v(250, -84.25) * mm, "end": v(251.11, -83.5) * mm});
            skLineSegment(sketch, "E676", {"start": v(251.11, -83.5) * mm, "end": v(252.22, -82.75) * mm});
            skLineSegment(sketch, "E677", {"start": v(252.22, -82.75) * mm, "end": v(253.33, -81.99) * mm});
            skLineSegment(sketch, "E678", {"start": v(253.33, -81.99) * mm, "end": v(254.44, -81.23) * mm});
            skLineSegment(sketch, "E679", {"start": v(254.44, -81.23) * mm, "end": v(255.56, -80.46) * mm});
            skLineSegment(sketch, "E680", {"start": v(255.56, -80.46) * mm, "end": v(256.67, -79.7) * mm});
            skLineSegment(sketch, "E681", {"start": v(256.67, -79.7) * mm, "end": v(257.78, -78.93) * mm});
            skLineSegment(sketch, "E682", {"start": v(257.78, -78.93) * mm, "end": v(258.89, -78.15) * mm});
            skLineSegment(sketch, "E683", {"start": v(258.89, -78.15) * mm, "end": v(260, -77.38) * mm});
            skLineSegment(sketch, "E684", {"start": v(260, -77.38) * mm, "end": v(261.11, -76.6) * mm});
            skLineSegment(sketch, "E685", {"start": v(261.11, -76.6) * mm, "end": v(262.22, -75.81) * mm});
            skLineSegment(sketch, "E686", {"start": v(262.22, -75.81) * mm, "end": v(263.33, -75.02) * mm});
            skLineSegment(sketch, "E687", {"start": v(263.33, -75.02) * mm, "end": v(264.44, -74.23) * mm});
            skLineSegment(sketch, "E688", {"start": v(264.44, -74.23) * mm, "end": v(265.56, -73.44) * mm});
            skLineSegment(sketch, "E689", {"start": v(265.56, -73.44) * mm, "end": v(266.67, -72.64) * mm});
            skLineSegment(sketch, "E690", {"start": v(266.67, -72.64) * mm, "end": v(267.78, -71.84) * mm});
            skLineSegment(sketch, "E691", {"start": v(267.78, -71.84) * mm, "end": v(268.89, -71.04) * mm});
            skLineSegment(sketch, "E692", {"start": v(268.89, -71.04) * mm, "end": v(270, -70.23) * mm});
            skLineSegment(sketch, "E693", {"start": v(270, -70.23) * mm, "end": v(271.11, -69.42) * mm});
            skLineSegment(sketch, "E694", {"start": v(271.11, -69.42) * mm, "end": v(272.22, -68.6) * mm});
            skLineSegment(sketch, "E695", {"start": v(272.22, -68.6) * mm, "end": v(273.33, -67.79) * mm});
            skLineSegment(sketch, "E696", {"start": v(273.33, -67.79) * mm, "end": v(274.44, -66.97) * mm});
            skLineSegment(sketch, "E697", {"start": v(274.44, -66.97) * mm, "end": v(275.56, -66.15) * mm});
            skLineSegment(sketch, "E698", {"start": v(275.56, -66.15) * mm, "end": v(276.67, -65.32) * mm});
            skLineSegment(sketch, "E699", {"start": v(276.67, -65.32) * mm, "end": v(277.78, -64.49) * mm});
            skLineSegment(sketch, "E700", {"start": v(277.78, -64.49) * mm, "end": v(278.89, -63.65) * mm});
            skLineSegment(sketch, "E701", {"start": v(278.89, -63.65) * mm, "end": v(280, -62.82) * mm});
            skLineSegment(sketch, "E702", {"start": v(280, -62.82) * mm, "end": v(281.11, -61.98) * mm});
            skLineSegment(sketch, "E703", {"start": v(281.11, -61.98) * mm, "end": v(282.22, -61.13) * mm});
            skLineSegment(sketch, "E704", {"start": v(282.22, -61.13) * mm, "end": v(283.33, -60.29) * mm});
            skLineSegment(sketch, "E705", {"start": v(283.33, -60.29) * mm, "end": v(284.44, -59.44) * mm});
            skLineSegment(sketch, "E706", {"start": v(284.44, -59.44) * mm, "end": v(285.56, -58.58) * mm});
            skLineSegment(sketch, "E707", {"start": v(285.56, -58.58) * mm, "end": v(286.67, -57.72) * mm});
            skLineSegment(sketch, "E708", {"start": v(286.67, -57.72) * mm, "end": v(287.78, -56.86) * mm});
            skLineSegment(sketch, "E709", {"start": v(287.78, -56.86) * mm, "end": v(288.89, -56) * mm});
            skLineSegment(sketch, "E710", {"start": v(288.89, -56) * mm, "end": v(290, -55.13) * mm});
            skLineSegment(sketch, "E711", {"start": v(290, -55.13) * mm, "end": v(291.11, -54.26) * mm});
            skLineSegment(sketch, "E712", {"start": v(291.11, -54.26) * mm, "end": v(292.22, -53.39) * mm});
            skLineSegment(sketch, "E713", {"start": v(292.22, -53.39) * mm, "end": v(293.33, -52.51) * mm});
            skLineSegment(sketch, "E714", {"start": v(293.33, -52.51) * mm, "end": v(294.44, -51.63) * mm});
            skLineSegment(sketch, "E715", {"start": v(294.44, -51.63) * mm, "end": v(295.56, -50.75) * mm});
            skLineSegment(sketch, "E716", {"start": v(295.56, -50.75) * mm, "end": v(296.67, -49.86) * mm});
            skLineSegment(sketch, "E717", {"start": v(296.67, -49.86) * mm, "end": v(297.78, -48.97) * mm});
            skLineSegment(sketch, "E718", {"start": v(297.78, -48.97) * mm, "end": v(298.89, -48.08) * mm});
            skLineSegment(sketch, "E719", {"start": v(298.89, -48.08) * mm, "end": v(300, -47.18) * mm});
            skLineSegment(sketch, "E720", {"start": v(300, -47.18) * mm, "end": v(301.11, -46.28) * mm});
            skLineSegment(sketch, "E721", {"start": v(301.11, -46.28) * mm, "end": v(302.22, -45.38) * mm});
            skLineSegment(sketch, "E722", {"start": v(302.22, -45.38) * mm, "end": v(303.33, -44.47) * mm});
            skLineSegment(sketch, "E723", {"start": v(303.33, -44.47) * mm, "end": v(304.44, -43.56) * mm});
            skLineSegment(sketch, "E724", {"start": v(304.44, -43.56) * mm, "end": v(305.56, -42.65) * mm});
            skLineSegment(sketch, "E725", {"start": v(305.56, -42.65) * mm, "end": v(306.67, -41.73) * mm});
            skLineSegment(sketch, "E726", {"start": v(306.67, -41.73) * mm, "end": v(307.78, -40.8) * mm});
            skLineSegment(sketch, "E727", {"start": v(307.78, -40.8) * mm, "end": v(308.89, -39.88) * mm});
            skLineSegment(sketch, "E728", {"start": v(308.89, -39.88) * mm, "end": v(310, -38.96) * mm});
            skLineSegment(sketch, "E729", {"start": v(310, -38.96) * mm, "end": v(311.11, -38.03) * mm});
            skLineSegment(sketch, "E730", {"start": v(311.11, -38.03) * mm, "end": v(312.22, -37.1) * mm});
            skLineSegment(sketch, "E731", {"start": v(312.22, -37.1) * mm, "end": v(313.33, -36.16) * mm});
            skLineSegment(sketch, "E732", {"start": v(313.33, -36.16) * mm, "end": v(314.44, -35.22) * mm});
            skLineSegment(sketch, "E733", {"start": v(314.44, -35.22) * mm, "end": v(315.56, -34.27) * mm});
            skLineSegment(sketch, "E734", {"start": v(315.56, -34.27) * mm, "end": v(316.67, -33.33) * mm});
            skLineSegment(sketch, "E735", {"start": v(316.67, -33.33) * mm, "end": v(317.78, -32.38) * mm});
            skLineSegment(sketch, "E736", {"start": v(317.78, -32.38) * mm, "end": v(318.89, -31.42) * mm});
            skLineSegment(sketch, "E737", {"start": v(318.89, -31.42) * mm, "end": v(320, -30.46) * mm});
            skLineSegment(sketch, "E738", {"start": v(320, -30.46) * mm, "end": v(321.11, -29.5) * mm});
            skLineSegment(sketch, "E739", {"start": v(321.11, -29.5) * mm, "end": v(322.22, -28.54) * mm});
            skLineSegment(sketch, "E740", {"start": v(322.22, -28.54) * mm, "end": v(323.33, -27.57) * mm});
            skLineSegment(sketch, "E741", {"start": v(323.33, -27.57) * mm, "end": v(324.44, -26.6) * mm});
            skLineSegment(sketch, "E742", {"start": v(324.44, -26.6) * mm, "end": v(325.56, -25.63) * mm});
            skLineSegment(sketch, "E743", {"start": v(325.56, -25.63) * mm, "end": v(326.67, -24.65) * mm});
            skLineSegment(sketch, "E744", {"start": v(326.67, -24.65) * mm, "end": v(327.78, -23.67) * mm});
            skLineSegment(sketch, "E745", {"start": v(327.78, -23.67) * mm, "end": v(328.89, -22.69) * mm});
            skLineSegment(sketch, "E746", {"start": v(328.89, -22.69) * mm, "end": v(330, -21.7) * mm});
            skLineSegment(sketch, "E747", {"start": v(330, -21.7) * mm, "end": v(331.11, -20.71) * mm});
            skLineSegment(sketch, "E748", {"start": v(331.11, -20.71) * mm, "end": v(332.22, -19.72) * mm});
            skLineSegment(sketch, "E749", {"start": v(332.22, -19.72) * mm, "end": v(333.33, -18.72) * mm});
            skLineSegment(sketch, "E750", {"start": v(333.33, -18.72) * mm, "end": v(334.44, -17.72) * mm});
            skLineSegment(sketch, "E751", {"start": v(334.44, -17.72) * mm, "end": v(335.56, -16.72) * mm});
            skLineSegment(sketch, "E752", {"start": v(335.56, -16.72) * mm, "end": v(336.67, -15.71) * mm});
            skLineSegment(sketch, "E753", {"start": v(336.67, -15.71) * mm, "end": v(337.78, -14.7) * mm});
            skLineSegment(sketch, "E754", {"start": v(337.78, -14.7) * mm, "end": v(338.89, -13.69) * mm});
            skLineSegment(sketch, "E755", {"start": v(338.89, -13.69) * mm, "end": v(340, -12.67) * mm});
            skLineSegment(sketch, "E756", {"start": v(340, -12.67) * mm, "end": v(341.11, -11.65) * mm});
            skLineSegment(sketch, "E757", {"start": v(341.11, -11.65) * mm, "end": v(342.22, -10.63) * mm});
            skLineSegment(sketch, "E758", {"start": v(342.22, -10.63) * mm, "end": v(343.33, -9.6) * mm});
            skLineSegment(sketch, "E759", {"start": v(343.33, -9.6) * mm, "end": v(344.44, -8.57) * mm});
            skLineSegment(sketch, "E760", {"start": v(344.44, -8.57) * mm, "end": v(345.56, -7.54) * mm});
            skLineSegment(sketch, "E761", {"start": v(345.56, -7.54) * mm, "end": v(346.67, -6.5) * mm});
            skLineSegment(sketch, "E762", {"start": v(346.67, -6.5) * mm, "end": v(347.78, -5.46) * mm});
            skLineSegment(sketch, "E763", {"start": v(347.78, -5.46) * mm, "end": v(348.89, -4.42) * mm});
            skLineSegment(sketch, "E764", {"start": v(348.89, -4.42) * mm, "end": v(350, -3.37) * mm});
            skLineSegment(sketch, "E765", {"start": v(350, -3.37) * mm, "end": v(351.11, -2.32) * mm});
            skLineSegment(sketch, "E766", {"start": v(351.11, -2.32) * mm, "end": v(352.22, -1.27) * mm});
            skLineSegment(sketch, "E767", {"start": v(352.22, -1.27) * mm, "end": v(353.33, -0.2) * mm});
            skLineSegment(sketch, "E768", {"start": v(353.33, -0.2) * mm, "end": v(354.44, 0.85) * mm});
            skLineSegment(sketch, "E769", {"start": v(354.44, 0.85) * mm, "end": v(355.56, 1.91) * mm});
            skLineSegment(sketch, "E770", {"start": v(355.56, 1.91) * mm, "end": v(356.67, 2.98) * mm});
            skLineSegment(sketch, "E771", {"start": v(356.67, 2.98) * mm, "end": v(357.78, 4.05) * mm});
            skLineSegment(sketch, "E772", {"start": v(357.78, 4.05) * mm, "end": v(358.89, 5.12) * mm});
            skLineSegment(sketch, "E773", {"start": v(358.89, 5.12) * mm, "end": v(360, 6.2) * mm});
            skLineSegment(sketch, "E774", {"start": v(360, 6.2) * mm, "end": v(361.11, 7.28) * mm});
            skLineSegment(sketch, "E775", {"start": v(361.11, 7.28) * mm, "end": v(362.22, 8.36) * mm});
            skLineSegment(sketch, "E776", {"start": v(362.22, 8.36) * mm, "end": v(363.33, 9.45) * mm});
            skLineSegment(sketch, "E777", {"start": v(363.33, 9.45) * mm, "end": v(364.44, 10.54) * mm});
            skLineSegment(sketch, "E778", {"start": v(364.44, 10.54) * mm, "end": v(365.56, 11.63) * mm});
            skLineSegment(sketch, "E779", {"start": v(365.56, 11.63) * mm, "end": v(366.67, 12.73) * mm});
            skLineSegment(sketch, "E780", {"start": v(366.67, 12.73) * mm, "end": v(367.78, 13.83) * mm});
            skLineSegment(sketch, "E781", {"start": v(367.78, 13.83) * mm, "end": v(368.89, 14.93) * mm});
            skLineSegment(sketch, "E782", {"start": v(368.89, 14.93) * mm, "end": v(370, 16.04) * mm});
            skLineSegment(sketch, "E783", {"start": v(370, 16.04) * mm, "end": v(371.11, 17.15) * mm});
            skLineSegment(sketch, "E784", {"start": v(371.11, 17.15) * mm, "end": v(372.22, 18.26) * mm});
            skLineSegment(sketch, "E785", {"start": v(372.22, 18.26) * mm, "end": v(373.33, 19.38) * mm});
            skLineSegment(sketch, "E786", {"start": v(373.33, 19.38) * mm, "end": v(374.44, 20.5) * mm});
            skLineSegment(sketch, "E787", {"start": v(374.44, 20.5) * mm, "end": v(375.56, 21.63) * mm});
            skLineSegment(sketch, "E788", {"start": v(375.56, 21.63) * mm, "end": v(376.67, 22.75) * mm});
            skLineSegment(sketch, "E789", {"start": v(376.67, 22.75) * mm, "end": v(377.78, 23.88) * mm});
            skLineSegment(sketch, "E790", {"start": v(377.78, 23.88) * mm, "end": v(378.89, 25.02) * mm});
            skLineSegment(sketch, "E791", {"start": v(378.89, 25.02) * mm, "end": v(380, 26.15) * mm});
            skLineSegment(sketch, "E792", {"start": v(380, 26.15) * mm, "end": v(381.11, 27.3) * mm});
            skLineSegment(sketch, "E793", {"start": v(381.11, 27.3) * mm, "end": v(382.22, 28.43) * mm});
            skLineSegment(sketch, "E794", {"start": v(382.22, 28.43) * mm, "end": v(383.33, 29.58) * mm});
            skLineSegment(sketch, "E795", {"start": v(383.33, 29.58) * mm, "end": v(384.44, 30.73) * mm});
            skLineSegment(sketch, "E796", {"start": v(384.44, 30.73) * mm, "end": v(385.56, 31.88) * mm});
            skLineSegment(sketch, "E797", {"start": v(385.56, 31.88) * mm, "end": v(386.67, 33.04) * mm});
            skLineSegment(sketch, "E798", {"start": v(386.67, 33.04) * mm, "end": v(387.78, 34.2) * mm});
            skLineSegment(sketch, "E799", {"start": v(387.78, 34.2) * mm, "end": v(388.89, 35.36) * mm});
            skLineSegment(sketch, "E800", {"start": v(388.89, 35.36) * mm, "end": v(390, 36.53) * mm});
            skLineSegment(sketch, "E801", {"start": v(390, 36.53) * mm, "end": v(391.11, 37.7) * mm});
            skLineSegment(sketch, "E802", {"start": v(391.11, 37.7) * mm, "end": v(392.22, 38.87) * mm});
            skLineSegment(sketch, "E803", {"start": v(392.22, 38.87) * mm, "end": v(393.33, 40.05) * mm});
            skLineSegment(sketch, "E804", {"start": v(393.33, 40.05) * mm, "end": v(394.44, 41.23) * mm});
            skLineSegment(sketch, "E805", {"start": v(394.44, 41.23) * mm, "end": v(395.56, 42.41) * mm});
            skLineSegment(sketch, "E806", {"start": v(395.56, 42.41) * mm, "end": v(396.67, 43.6) * mm});
            skLineSegment(sketch, "E807", {"start": v(396.67, 43.6) * mm, "end": v(397.78, 44.8) * mm});
            skLineSegment(sketch, "E808", {"start": v(397.78, 44.8) * mm, "end": v(398.89, 45.98) * mm});
            skLineSegment(sketch, "E809", {"start": v(398.89, 45.98) * mm, "end": v(400, 47.18) * mm});
            skLineSegment(sketch, "E810", {"start": v(400, 47.18) * mm, "end": v(401.11, 48.38) * mm});
            skLineSegment(sketch, "E811", {"start": v(401.11, 48.38) * mm, "end": v(402.22, 49.58) * mm});
            skLineSegment(sketch, "E812", {"start": v(402.22, 49.58) * mm, "end": v(403.33, 50.8) * mm});
            skLineSegment(sketch, "E813", {"start": v(403.33, 50.8) * mm, "end": v(404.44, 52) * mm});
            skLineSegment(sketch, "E814", {"start": v(404.44, 52) * mm, "end": v(405.56, 53.21) * mm});
            skLineSegment(sketch, "E815", {"start": v(405.56, 53.21) * mm, "end": v(406.67, 54.43) * mm});
            skLineSegment(sketch, "E816", {"start": v(406.67, 54.43) * mm, "end": v(407.78, 55.65) * mm});
            skLineSegment(sketch, "E817", {"start": v(407.78, 55.65) * mm, "end": v(408.89, 56.87) * mm});
            skLineSegment(sketch, "E818", {"start": v(408.89, 56.87) * mm, "end": v(410, 58.1) * mm});
            skLineSegment(sketch, "E819", {"start": v(410, 58.1) * mm, "end": v(411.11, 59.33) * mm});
            skLineSegment(sketch, "E820", {"start": v(411.11, 59.33) * mm, "end": v(412.22, 60.56) * mm});
            skLineSegment(sketch, "E821", {"start": v(412.22, 60.56) * mm, "end": v(413.33, 61.8) * mm});
            skLineSegment(sketch, "E822", {"start": v(413.33, 61.8) * mm, "end": v(414.44, 63.04) * mm});
            skLineSegment(sketch, "E823", {"start": v(414.44, 63.04) * mm, "end": v(415.56, 64.28) * mm});
            skLineSegment(sketch, "E824", {"start": v(415.56, 64.28) * mm, "end": v(416.67, 65.53) * mm});
            skLineSegment(sketch, "E825", {"start": v(416.67, 65.53) * mm, "end": v(417.78, 66.78) * mm});
            skLineSegment(sketch, "E826", {"start": v(417.78, 66.78) * mm, "end": v(418.89, 68.03) * mm});
            skLineSegment(sketch, "E827", {"start": v(418.89, 68.03) * mm, "end": v(420, 69.29) * mm});
            skLineSegment(sketch, "E828", {"start": v(420, 69.29) * mm, "end": v(421.11, 70.55) * mm});
            skLineSegment(sketch, "E829", {"start": v(421.11, 70.55) * mm, "end": v(422.22, 71.81) * mm});
            skLineSegment(sketch, "E830", {"start": v(422.22, 71.81) * mm, "end": v(423.33, 73.08) * mm});
            skLineSegment(sketch, "E831", {"start": v(423.33, 73.08) * mm, "end": v(424.44, 74.35) * mm});
            skLineSegment(sketch, "E832", {"start": v(424.44, 74.35) * mm, "end": v(425.56, 75.62) * mm});
            skLineSegment(sketch, "E833", {"start": v(425.56, 75.62) * mm, "end": v(426.67, 76.9) * mm});
            skLineSegment(sketch, "E834", {"start": v(426.67, 76.9) * mm, "end": v(427.78, 78.18) * mm});
            skLineSegment(sketch, "E835", {"start": v(427.78, 78.18) * mm, "end": v(428.89, 79.46) * mm});
            skLineSegment(sketch, "E836", {"start": v(428.89, 79.46) * mm, "end": v(430, 80.75) * mm});
            skLineSegment(sketch, "E837", {"start": v(430, 80.75) * mm, "end": v(431.11, 82.04) * mm});
            skLineSegment(sketch, "E838", {"start": v(431.11, 82.04) * mm, "end": v(432.22, 83.33) * mm});
            skLineSegment(sketch, "E839", {"start": v(432.22, 83.33) * mm, "end": v(433.33, 84.63) * mm});
            skLineSegment(sketch, "E840", {"start": v(433.33, 84.63) * mm, "end": v(434.44, 85.93) * mm});
            skLineSegment(sketch, "E841", {"start": v(434.44, 85.93) * mm, "end": v(435.56, 87.23) * mm});
            skLineSegment(sketch, "E842", {"start": v(435.56, 87.23) * mm, "end": v(436.67, 88.53) * mm});
            skLineSegment(sketch, "E843", {"start": v(436.67, 88.53) * mm, "end": v(437.78, 89.84) * mm});
            skLineSegment(sketch, "E844", {"start": v(437.78, 89.84) * mm, "end": v(438.89, 91.16) * mm});
            skLineSegment(sketch, "E845", {"start": v(438.89, 91.16) * mm, "end": v(440, 92.47) * mm});
            skLineSegment(sketch, "E846", {"start": v(440, 92.47) * mm, "end": v(441.11, 93.8) * mm});
            skLineSegment(sketch, "E847", {"start": v(441.11, 93.8) * mm, "end": v(442.22, 95.12) * mm});
            skLineSegment(sketch, "E848", {"start": v(442.22, 95.12) * mm, "end": v(443.33, 96.44) * mm});
            skLineSegment(sketch, "E849", {"start": v(443.33, 96.44) * mm, "end": v(444.44, 97.77) * mm});
            skLineSegment(sketch, "E850", {"start": v(444.44, 97.77) * mm, "end": v(445.56, 99.1) * mm});
            skLineSegment(sketch, "E851", {"start": v(445.56, 99.1) * mm, "end": v(446.67, 100.44) * mm});
            skLineSegment(sketch, "E852", {"start": v(446.67, 100.44) * mm, "end": v(447.78, 101.78) * mm});
            skLineSegment(sketch, "E853", {"start": v(447.78, 101.78) * mm, "end": v(448.89, 103.12) * mm});
            skLineSegment(sketch, "E854", {"start": v(448.89, 103.12) * mm, "end": v(450, 104.47) * mm});
            skLineSegment(sketch, "E855", {"start": v(450, 104.47) * mm, "end": v(451.11, 105.82) * mm});
            skLineSegment(sketch, "E856", {"start": v(451.11, 105.82) * mm, "end": v(452.22, 107.17) * mm});
            skLineSegment(sketch, "E857", {"start": v(452.22, 107.17) * mm, "end": v(453.33, 108.53) * mm});
            skLineSegment(sketch, "E858", {"start": v(453.33, 108.53) * mm, "end": v(454.44, 109.89) * mm});
            skLineSegment(sketch, "E859", {"start": v(454.44, 109.89) * mm, "end": v(455.56, 111.25) * mm});
            skLineSegment(sketch, "E860", {"start": v(455.56, 111.25) * mm, "end": v(456.67, 112.62) * mm});
            skLineSegment(sketch, "E861", {"start": v(456.67, 112.62) * mm, "end": v(457.78, 113.99) * mm});
            skLineSegment(sketch, "E862", {"start": v(457.78, 113.99) * mm, "end": v(458.89, 115.36) * mm});
            skLineSegment(sketch, "E863", {"start": v(458.89, 115.36) * mm, "end": v(460, 116.74) * mm});
            skLineSegment(sketch, "E864", {"start": v(460, 116.74) * mm, "end": v(461.11, 118.12) * mm});
            skLineSegment(sketch, "E865", {"start": v(461.11, 118.12) * mm, "end": v(462.22, 119.5) * mm});
            skLineSegment(sketch, "E866", {"start": v(462.22, 119.5) * mm, "end": v(463.33, 120.89) * mm});
            skLineSegment(sketch, "E867", {"start": v(463.33, 120.89) * mm, "end": v(464.44, 122.28) * mm});
            skLineSegment(sketch, "E868", {"start": v(464.44, 122.28) * mm, "end": v(465.56, 123.67) * mm});
            skLineSegment(sketch, "E869", {"start": v(465.56, 123.67) * mm, "end": v(466.67, 125.07) * mm});
            skLineSegment(sketch, "E870", {"start": v(466.67, 125.07) * mm, "end": v(467.78, 126.47) * mm});
            skLineSegment(sketch, "E871", {"start": v(467.78, 126.47) * mm, "end": v(468.89, 127.87) * mm});
            skLineSegment(sketch, "E872", {"start": v(468.89, 127.87) * mm, "end": v(470, 129.27) * mm});
            skLineSegment(sketch, "E873", {"start": v(470, 129.27) * mm, "end": v(471.11, 130.68) * mm});
            skLineSegment(sketch, "E874", {"start": v(471.11, 130.68) * mm, "end": v(472.22, 132.1) * mm});
            skLineSegment(sketch, "E875", {"start": v(472.22, 132.1) * mm, "end": v(473.33, 133.51) * mm});
            skLineSegment(sketch, "E876", {"start": v(473.33, 133.51) * mm, "end": v(474.44, 134.93) * mm});
            skLineSegment(sketch, "E877", {"start": v(474.44, 134.93) * mm, "end": v(475.56, 136.36) * mm});
            skLineSegment(sketch, "E878", {"start": v(475.56, 136.36) * mm, "end": v(476.67, 137.78) * mm});
            skLineSegment(sketch, "E879", {"start": v(476.67, 137.78) * mm, "end": v(477.78, 139.21) * mm});
            skLineSegment(sketch, "E880", {"start": v(477.78, 139.21) * mm, "end": v(478.89, 140.64) * mm});
            skLineSegment(sketch, "E881", {"start": v(478.89, 140.64) * mm, "end": v(480, 142.08) * mm});
            skLineSegment(sketch, "E882", {"start": v(480, 142.08) * mm, "end": v(481.11, 143.52) * mm});
            skLineSegment(sketch, "E883", {"start": v(481.11, 143.52) * mm, "end": v(482.22, 144.96) * mm});
            skLineSegment(sketch, "E884", {"start": v(482.22, 144.96) * mm, "end": v(483.33, 146.4) * mm});
            skLineSegment(sketch, "E885", {"start": v(483.33, 146.4) * mm, "end": v(484.44, 147.86) * mm});
            skLineSegment(sketch, "E886", {"start": v(484.44, 147.86) * mm, "end": v(485.56, 149.31) * mm});
            skLineSegment(sketch, "E887", {"start": v(485.56, 149.31) * mm, "end": v(486.67, 150.77) * mm});
            skLineSegment(sketch, "E888", {"start": v(486.67, 150.77) * mm, "end": v(487.78, 152.23) * mm});
            skLineSegment(sketch, "E889", {"start": v(487.78, 152.23) * mm, "end": v(488.89, 153.69) * mm});
            skLineSegment(sketch, "E890", {"start": v(488.89, 153.69) * mm, "end": v(490, 155.16) * mm});
            skLineSegment(sketch, "E891", {"start": v(490, 155.16) * mm, "end": v(491.11, 156.63) * mm});
            skLineSegment(sketch, "E892", {"start": v(491.11, 156.63) * mm, "end": v(492.22, 158.1) * mm});
            skLineSegment(sketch, "E893", {"start": v(492.22, 158.1) * mm, "end": v(493.33, 159.57) * mm});
            skLineSegment(sketch, "E894", {"start": v(493.33, 159.57) * mm, "end": v(494.44, 161.05) * mm});
            skLineSegment(sketch, "E895", {"start": v(494.44, 161.05) * mm, "end": v(495.56, 162.54) * mm});
            skLineSegment(sketch, "E896", {"start": v(495.56, 162.54) * mm, "end": v(496.67, 164.02) * mm});
            skLineSegment(sketch, "E897", {"start": v(496.67, 164.02) * mm, "end": v(497.78, 165.51) * mm});
            skLineSegment(sketch, "E898", {"start": v(497.78, 165.51) * mm, "end": v(498.89, 167) * mm});
            skLineSegment(sketch, "E899", {"start": v(498.89, 167) * mm, "end": v(500, 168.5) * mm});
            skLineSegment(sketch, "E900.0", {"start": v(499.7, 166.4) * mm, "end": v(500.8, 167.9) * mm});
            skLineSegment(sketch, "E900.1", {"start": v(498.58, 164.91) * mm, "end": v(499.7, 166.4) * mm});
            skLineSegment(sketch, "E900.2", {"start": v(497.47, 163.42) * mm, "end": v(498.58, 164.91) * mm});
            skLineSegment(sketch, "E900.3", {"start": v(496.36, 161.94) * mm, "end": v(497.47, 163.42) * mm});
            skLineSegment(sketch, "E900.4", {"start": v(495.24, 160.45) * mm, "end": v(496.36, 161.94) * mm});
            skLineSegment(sketch, "E900.5", {"start": v(494.13, 158.97) * mm, "end": v(495.24, 160.45) * mm});
            skLineSegment(sketch, "E900.6", {"start": v(493.02, 157.5) * mm, "end": v(494.13, 158.97) * mm});
            skLineSegment(sketch, "E900.7", {"start": v(491.9, 156.02) * mm, "end": v(493.02, 157.5) * mm});
            skLineSegment(sketch, "E900.8", {"start": v(490.8, 154.55) * mm, "end": v(491.9, 156.02) * mm});
            skLineSegment(sketch, "E900.9", {"start": v(489.69, 153.09) * mm, "end": v(490.8, 154.55) * mm});
            skLineSegment(sketch, "E900.10", {"start": v(488.57, 151.62) * mm, "end": v(489.69, 153.09) * mm});
            skLineSegment(sketch, "E900.11", {"start": v(487.46, 150.16) * mm, "end": v(488.57, 151.62) * mm});
            skLineSegment(sketch, "E900.12", {"start": v(486.35, 148.7) * mm, "end": v(487.46, 150.16) * mm});
            skLineSegment(sketch, "E900.13", {"start": v(485.24, 147.25) * mm, "end": v(486.35, 148.7) * mm});
            skLineSegment(sketch, "E900.14", {"start": v(484.13, 145.8) * mm, "end": v(485.24, 147.25) * mm});
            skLineSegment(sketch, "E900.15", {"start": v(483.01, 144.35) * mm, "end": v(484.13, 145.8) * mm});
            skLineSegment(sketch, "E900.16", {"start": v(481.9, 142.9) * mm, "end": v(483.01, 144.35) * mm});
            skLineSegment(sketch, "E900.17", {"start": v(480.8, 141.47) * mm, "end": v(481.9, 142.9) * mm});
            skLineSegment(sketch, "E900.18", {"start": v(479.68, 140.03) * mm, "end": v(480.8, 141.47) * mm});
            skLineSegment(sketch, "E900.19", {"start": v(478.57, 138.6) * mm, "end": v(479.68, 140.03) * mm});
            skLineSegment(sketch, "E900.20", {"start": v(477.46, 137.17) * mm, "end": v(478.57, 138.6) * mm});
            skLineSegment(sketch, "E900.21", {"start": v(476.34, 135.74) * mm, "end": v(477.46, 137.17) * mm});
            skLineSegment(sketch, "E900.22", {"start": v(475.23, 134.32) * mm, "end": v(476.34, 135.74) * mm});
            skLineSegment(sketch, "E900.23", {"start": v(474.12, 132.9) * mm, "end": v(475.23, 134.32) * mm});
            skLineSegment(sketch, "E900.24", {"start": v(473, 131.48) * mm, "end": v(474.12, 132.9) * mm});
            skLineSegment(sketch, "E900.25", {"start": v(471.9, 130.07) * mm, "end": v(473, 131.48) * mm});
            skLineSegment(sketch, "E900.26", {"start": v(470.78, 128.65) * mm, "end": v(471.9, 130.07) * mm});
            skLineSegment(sketch, "E900.27", {"start": v(469.67, 127.25) * mm, "end": v(470.78, 128.65) * mm});
            skLineSegment(sketch, "E900.28", {"start": v(468.56, 125.84) * mm, "end": v(469.67, 127.25) * mm});
            skLineSegment(sketch, "E900.29", {"start": v(467.45, 124.44) * mm, "end": v(468.56, 125.84) * mm});
            skLineSegment(sketch, "E900.30", {"start": v(466.34, 123.05) * mm, "end": v(467.45, 124.44) * mm});
            skLineSegment(sketch, "E900.31", {"start": v(465.23, 121.65) * mm, "end": v(466.34, 123.05) * mm});
            skLineSegment(sketch, "E900.32", {"start": v(464.11, 120.26) * mm, "end": v(465.23, 121.65) * mm});
            skLineSegment(sketch, "E900.33", {"start": v(463, 118.87) * mm, "end": v(464.11, 120.26) * mm});
            skLineSegment(sketch, "E900.34", {"start": v(461.9, 117.5) * mm, "end": v(463, 118.87) * mm});
            skLineSegment(sketch, "E900.35", {"start": v(460.78, 116.11) * mm, "end": v(461.9, 117.5) * mm});
            skLineSegment(sketch, "E900.36", {"start": v(459.67, 114.73) * mm, "end": v(460.78, 116.11) * mm});
            skLineSegment(sketch, "E900.37", {"start": v(458.55, 113.36) * mm, "end": v(459.67, 114.73) * mm});
            skLineSegment(sketch, "E900.38", {"start": v(457.44, 111.99) * mm, "end": v(458.55, 113.36) * mm});
            skLineSegment(sketch, "E900.39", {"start": v(456.33, 110.62) * mm, "end": v(457.44, 111.99) * mm});
            skLineSegment(sketch, "E900.40", {"start": v(455.22, 109.26) * mm, "end": v(456.33, 110.62) * mm});
            skLineSegment(sketch, "E900.41", {"start": v(454.1, 107.9) * mm, "end": v(455.22, 109.26) * mm});
            skLineSegment(sketch, "E900.42", {"start": v(453, 106.54) * mm, "end": v(454.1, 107.9) * mm});
            skLineSegment(sketch, "E900.43", {"start": v(451.88, 105.19) * mm, "end": v(453, 106.54) * mm});
            skLineSegment(sketch, "E900.44", {"start": v(450.77, 103.83) * mm, "end": v(451.88, 105.19) * mm});
            skLineSegment(sketch, "E900.45", {"start": v(449.66, 102.49) * mm, "end": v(450.77, 103.83) * mm});
            skLineSegment(sketch, "E900.46", {"start": v(448.55, 101.14) * mm, "end": v(449.66, 102.49) * mm});
            skLineSegment(sketch, "E900.47", {"start": v(447.44, 99.8) * mm, "end": v(448.55, 101.14) * mm});
            skLineSegment(sketch, "E900.48", {"start": v(446.32, 98.47) * mm, "end": v(447.44, 99.8) * mm});
            skLineSegment(sketch, "E900.49", {"start": v(445.21, 97.13) * mm, "end": v(446.32, 98.47) * mm});
            skLineSegment(sketch, "E900.50", {"start": v(444.1, 95.8) * mm, "end": v(445.21, 97.13) * mm});
            skLineSegment(sketch, "E900.51", {"start": v(442.99, 94.47) * mm, "end": v(444.1, 95.8) * mm});
            skLineSegment(sketch, "E900.52", {"start": v(441.88, 93.15) * mm, "end": v(442.99, 94.47) * mm});
            skLineSegment(sketch, "E900.53", {"start": v(440.76, 91.83) * mm, "end": v(441.88, 93.15) * mm});
            skLineSegment(sketch, "E900.54", {"start": v(439.65, 90.51) * mm, "end": v(440.76, 91.83) * mm});
            skLineSegment(sketch, "E900.55", {"start": v(438.54, 89.2) * mm, "end": v(439.65, 90.51) * mm});
            skLineSegment(sketch, "E900.56", {"start": v(437.43, 87.89) * mm, "end": v(438.54, 89.2) * mm});
            skLineSegment(sketch, "E900.57", {"start": v(436.32, 86.58) * mm, "end": v(437.43, 87.89) * mm});
            skLineSegment(sketch, "E900.58", {"start": v(435.2, 85.28) * mm, "end": v(436.32, 86.58) * mm});
            skLineSegment(sketch, "E900.59", {"start": v(434.1, 83.98) * mm, "end": v(435.2, 85.28) * mm});
            skLineSegment(sketch, "E900.60", {"start": v(432.98, 82.68) * mm, "end": v(434.1, 83.98) * mm});
            skLineSegment(sketch, "E900.61", {"start": v(431.87, 81.38) * mm, "end": v(432.98, 82.68) * mm});
            skLineSegment(sketch, "E900.62", {"start": v(430.76, 80.1) * mm, "end": v(431.87, 81.38) * mm});
            skLineSegment(sketch, "E900.63", {"start": v(429.65, 78.8) * mm, "end": v(430.76, 80.1) * mm});
            skLineSegment(sketch, "E900.64", {"start": v(428.53, 77.52) * mm, "end": v(429.65, 78.8) * mm});
            skLineSegment(sketch, "E900.65", {"start": v(427.42, 76.24) * mm, "end": v(428.53, 77.52) * mm});
            skLineSegment(sketch, "E900.66", {"start": v(426.3, 74.96) * mm, "end": v(427.42, 76.24) * mm});
            skLineSegment(sketch, "E900.67", {"start": v(425.2, 73.69) * mm, "end": v(426.3, 74.96) * mm});
            skLineSegment(sketch, "E900.68", {"start": v(424.09, 72.42) * mm, "end": v(425.2, 73.69) * mm});
            skLineSegment(sketch, "E900.69", {"start": v(422.97, 71.15) * mm, "end": v(424.09, 72.42) * mm});
            skLineSegment(sketch, "E900.70", {"start": v(421.86, 69.89) * mm, "end": v(422.97, 71.15) * mm});
            skLineSegment(sketch, "E900.71", {"start": v(420.75, 68.63) * mm, "end": v(421.86, 69.89) * mm});
            skLineSegment(sketch, "E900.72", {"start": v(419.64, 67.37) * mm, "end": v(420.75, 68.63) * mm});
            skLineSegment(sketch, "E900.73", {"start": v(418.53, 66.11) * mm, "end": v(419.64, 67.37) * mm});
            skLineSegment(sketch, "E900.74", {"start": v(417.41, 64.86) * mm, "end": v(418.53, 66.11) * mm});
            skLineSegment(sketch, "E900.75", {"start": v(416.3, 63.62) * mm, "end": v(417.41, 64.86) * mm});
            skLineSegment(sketch, "E900.76", {"start": v(415.19, 62.37) * mm, "end": v(416.3, 63.62) * mm});
            skLineSegment(sketch, "E900.77", {"start": v(414.08, 61.13) * mm, "end": v(415.19, 62.37) * mm});
            skLineSegment(sketch, "E900.78", {"start": v(-47.9, -166.42) * mm, "end": v(-46.8, -166.56) * mm});
            skLineSegment(sketch, "E900.79", {"start": v(-49.02, -166.27) * mm, "end": v(-47.9, -166.42) * mm});
            skLineSegment(sketch, "E900.80", {"start": v(-50.13, -166.12) * mm, "end": v(-49.02, -166.27) * mm});
            skLineSegment(sketch, "E900.81", {"start": v(-51.25, -165.97) * mm, "end": v(-50.13, -166.12) * mm});
            skLineSegment(sketch, "E900.82", {"start": v(-52.36, -165.82) * mm, "end": v(-51.25, -165.97) * mm});
            skLineSegment(sketch, "E900.83", {"start": v(-53.48, -165.66) * mm, "end": v(-52.36, -165.82) * mm});
            skLineSegment(sketch, "E900.84", {"start": v(-54.59, -165.5) * mm, "end": v(-53.48, -165.66) * mm});
            skLineSegment(sketch, "E900.85", {"start": v(-55.7, -165.33) * mm, "end": v(-54.59, -165.5) * mm});
            skLineSegment(sketch, "E900.86", {"start": v(-56.82, -165.16) * mm, "end": v(-55.7, -165.33) * mm});
            skLineSegment(sketch, "E900.87", {"start": v(-57.93, -164.99) * mm, "end": v(-56.82, -165.16) * mm});
            skLineSegment(sketch, "E900.88", {"start": v(-59.05, -164.81) * mm, "end": v(-57.93, -164.99) * mm});
            skLineSegment(sketch, "E900.89", {"start": v(-60.16, -164.64) * mm, "end": v(-59.05, -164.81) * mm});
            skLineSegment(sketch, "E900.90", {"start": v(-61.27, -164.45) * mm, "end": v(-60.16, -164.64) * mm});
            skLineSegment(sketch, "E900.91", {"start": v(-62.39, -164.27) * mm, "end": v(-61.27, -164.45) * mm});
            skLineSegment(sketch, "E900.92", {"start": v(-63.5, -164.08) * mm, "end": v(-62.39, -164.27) * mm});
            skLineSegment(sketch, "E900.93", {"start": v(-64.62, -163.89) * mm, "end": v(-63.5, -164.08) * mm});
            skLineSegment(sketch, "E900.94", {"start": v(-65.73, -163.7) * mm, "end": v(-64.62, -163.89) * mm});
            skLineSegment(sketch, "E900.95", {"start": v(-66.84, -163.5) * mm, "end": v(-65.73, -163.7) * mm});
            skLineSegment(sketch, "E900.96", {"start": v(-67.96, -163.3) * mm, "end": v(-66.84, -163.5) * mm});
            skLineSegment(sketch, "E900.97", {"start": v(-69.07, -163.09) * mm, "end": v(-67.96, -163.3) * mm});
            skLineSegment(sketch, "E900.98", {"start": v(-70.19, -162.88) * mm, "end": v(-69.07, -163.09) * mm});
            skLineSegment(sketch, "E900.99", {"start": v(-71.3, -162.67) * mm, "end": v(-70.19, -162.88) * mm});
            skLineSegment(sketch, "E900.100", {"start": v(-72.41, -162.45) * mm, "end": v(-71.3, -162.67) * mm});
            skLineSegment(sketch, "E900.101", {"start": v(-73.53, -162.23) * mm, "end": v(-72.41, -162.45) * mm});
            skLineSegment(sketch, "E900.102", {"start": v(-74.64, -162.01) * mm, "end": v(-73.53, -162.23) * mm});
            skLineSegment(sketch, "E900.103", {"start": v(-75.75, -161.79) * mm, "end": v(-74.64, -162.01) * mm});
            skLineSegment(sketch, "E900.104", {"start": v(-76.87, -161.56) * mm, "end": v(-75.75, -161.79) * mm});
            skLineSegment(sketch, "E900.105", {"start": v(-77.98, -161.33) * mm, "end": v(-76.87, -161.56) * mm});
            skLineSegment(sketch, "E900.106", {"start": v(-79.1, -161.1) * mm, "end": v(-77.98, -161.33) * mm});
            skLineSegment(sketch, "E900.107", {"start": v(-80.21, -160.85) * mm, "end": v(-79.1, -161.1) * mm});
            skLineSegment(sketch, "E900.108", {"start": v(-81.32, -160.61) * mm, "end": v(-80.21, -160.85) * mm});
            skLineSegment(sketch, "E900.109", {"start": v(-82.44, -160.36) * mm, "end": v(-81.32, -160.61) * mm});
            skLineSegment(sketch, "E900.110", {"start": v(-83.55, -160.12) * mm, "end": v(-82.44, -160.36) * mm});
            skLineSegment(sketch, "E900.111", {"start": v(-84.67, -159.86) * mm, "end": v(-83.55, -160.12) * mm});
            skLineSegment(sketch, "E900.112", {"start": v(-85.78, -159.6) * mm, "end": v(-84.67, -159.86) * mm});
            skLineSegment(sketch, "E900.113", {"start": v(-86.9, -159.35) * mm, "end": v(-85.78, -159.6) * mm});
            skLineSegment(sketch, "E900.114", {"start": v(-88, -159.09) * mm, "end": v(-86.9, -159.35) * mm});
            skLineSegment(sketch, "E900.115", {"start": v(-89.12, -158.82) * mm, "end": v(-88, -159.09) * mm});
            skLineSegment(sketch, "E900.116", {"start": v(-90.24, -158.55) * mm, "end": v(-89.12, -158.82) * mm});
            skLineSegment(sketch, "E900.117", {"start": v(-91.35, -158.28) * mm, "end": v(-90.24, -158.55) * mm});
            skLineSegment(sketch, "E900.118", {"start": v(-92.46, -158) * mm, "end": v(-91.35, -158.28) * mm});
            skLineSegment(sketch, "E900.119", {"start": v(-93.58, -157.73) * mm, "end": v(-92.46, -158) * mm});
            skLineSegment(sketch, "E900.120", {"start": v(-94.7, -157.45) * mm, "end": v(-93.58, -157.73) * mm});
            skLineSegment(sketch, "E900.121", {"start": v(-95.8, -157.16) * mm, "end": v(-94.7, -157.45) * mm});
            skLineSegment(sketch, "E900.122", {"start": v(-96.92, -156.87) * mm, "end": v(-95.8, -157.16) * mm});
            skLineSegment(sketch, "E900.123", {"start": v(-98.03, -156.58) * mm, "end": v(-96.92, -156.87) * mm});
            skLineSegment(sketch, "E900.124", {"start": v(-99.15, -156.29) * mm, "end": v(-98.03, -156.58) * mm});
            skLineSegment(sketch, "E900.125", {"start": v(-100.26, -155.99) * mm, "end": v(-99.15, -156.29) * mm});
            skLineSegment(sketch, "E900.126", {"start": v(-101.37, -155.69) * mm, "end": v(-100.26, -155.99) * mm});
            skLineSegment(sketch, "E900.127", {"start": v(-102.49, -155.38) * mm, "end": v(-101.37, -155.69) * mm});
            skLineSegment(sketch, "E900.128", {"start": v(-103.6, -155.07) * mm, "end": v(-102.49, -155.38) * mm});
            skLineSegment(sketch, "E900.129", {"start": v(-104.72, -154.76) * mm, "end": v(-103.6, -155.07) * mm});
            skLineSegment(sketch, "E900.130", {"start": v(-105.83, -154.44) * mm, "end": v(-104.72, -154.76) * mm});
            skLineSegment(sketch, "E900.131", {"start": v(-106.94, -154.13) * mm, "end": v(-105.83, -154.44) * mm});
            skLineSegment(sketch, "E900.132", {"start": v(-108.06, -153.8) * mm, "end": v(-106.94, -154.13) * mm});
            skLineSegment(sketch, "E900.133", {"start": v(-109.17, -153.48) * mm, "end": v(-108.06, -153.8) * mm});
            skLineSegment(sketch, "E900.134", {"start": v(-110.28, -153.15) * mm, "end": v(-109.17, -153.48) * mm});
            skLineSegment(sketch, "E900.135", {"start": v(-111.4, -152.82) * mm, "end": v(-110.28, -153.15) * mm});
            skLineSegment(sketch, "E900.136", {"start": v(-112.51, -152.48) * mm, "end": v(-111.4, -152.82) * mm});
            skLineSegment(sketch, "E900.137", {"start": v(-113.63, -152.14) * mm, "end": v(-112.51, -152.48) * mm});
            skLineSegment(sketch, "E900.138", {"start": v(-114.74, -151.8) * mm, "end": v(-113.63, -152.14) * mm});
            skLineSegment(sketch, "E900.139", {"start": v(-115.85, -151.46) * mm, "end": v(-114.74, -151.8) * mm});
            skLineSegment(sketch, "E900.140", {"start": v(-116.97, -151.1) * mm, "end": v(-115.85, -151.46) * mm});
            skLineSegment(sketch, "E900.141", {"start": v(-118.08, -150.76) * mm, "end": v(-116.97, -151.1) * mm});
            skLineSegment(sketch, "E900.142", {"start": v(-119.2, -150.4) * mm, "end": v(-118.08, -150.76) * mm});
            skLineSegment(sketch, "E900.143", {"start": v(-120.3, -150.04) * mm, "end": v(-119.2, -150.4) * mm});
            skLineSegment(sketch, "E900.144", {"start": v(-121.42, -149.68) * mm, "end": v(-120.3, -150.04) * mm});
            skLineSegment(sketch, "E900.145", {"start": v(-122.54, -149.31) * mm, "end": v(-121.42, -149.68) * mm});
            skLineSegment(sketch, "E900.146", {"start": v(-123.65, -148.95) * mm, "end": v(-122.54, -149.31) * mm});
            skLineSegment(sketch, "E900.147", {"start": v(-124.76, -148.57) * mm, "end": v(-123.65, -148.95) * mm});
            skLineSegment(sketch, "E900.148", {"start": v(-125.88, -148.2) * mm, "end": v(-124.76, -148.57) * mm});
            skLineSegment(sketch, "E900.149", {"start": v(-126.99, -147.82) * mm, "end": v(-125.88, -148.2) * mm});
            skLineSegment(sketch, "E900.150", {"start": v(-128.1, -147.44) * mm, "end": v(-126.99, -147.82) * mm});
            skLineSegment(sketch, "E900.151", {"start": v(-129.22, -147.05) * mm, "end": v(-128.1, -147.44) * mm});
            skLineSegment(sketch, "E900.152", {"start": v(-130.33, -146.66) * mm, "end": v(-129.22, -147.05) * mm});
            skLineSegment(sketch, "E900.153", {"start": v(-131.44, -146.27) * mm, "end": v(-130.33, -146.66) * mm});
            skLineSegment(sketch, "E900.154", {"start": v(-132.56, -145.88) * mm, "end": v(-131.44, -146.27) * mm});
            skLineSegment(sketch, "E900.155", {"start": v(-133.67, -145.48) * mm, "end": v(-132.56, -145.88) * mm});
            skLineSegment(sketch, "E900.156", {"start": v(-134.79, -145.08) * mm, "end": v(-133.67, -145.48) * mm});
            skLineSegment(sketch, "E900.157", {"start": v(-135.9, -144.67) * mm, "end": v(-134.79, -145.08) * mm});
            skLineSegment(sketch, "E900.158", {"start": v(-137.01, -144.26) * mm, "end": v(-135.9, -144.67) * mm});
            skLineSegment(sketch, "E900.159", {"start": v(-138.13, -143.85) * mm, "end": v(-137.01, -144.26) * mm});
            skLineSegment(sketch, "E900.160", {"start": v(-139.24, -143.44) * mm, "end": v(-138.13, -143.85) * mm});
            skLineSegment(sketch, "E900.161", {"start": v(-140.35, -143.02) * mm, "end": v(-139.24, -143.44) * mm});
            skLineSegment(sketch, "E900.162", {"start": v(-141.47, -142.6) * mm, "end": v(-140.35, -143.02) * mm});
            skLineSegment(sketch, "E900.163", {"start": v(-142.58, -142.17) * mm, "end": v(-141.47, -142.6) * mm});
            skLineSegment(sketch, "E900.164", {"start": v(-143.7, -141.74) * mm, "end": v(-142.58, -142.17) * mm});
            skLineSegment(sketch, "E900.165", {"start": v(-144.8, -141.3) * mm, "end": v(-143.7, -141.74) * mm});
            skLineSegment(sketch, "E900.166", {"start": v(-145.92, -140.87) * mm, "end": v(-144.8, -141.3) * mm});
            skLineSegment(sketch, "E900.167", {"start": v(-147.03, -140.43) * mm, "end": v(-145.92, -140.87) * mm});
            skLineSegment(sketch, "E900.168", {"start": v(-148.15, -140) * mm, "end": v(-147.03, -140.43) * mm});
            skLineSegment(sketch, "E900.169", {"start": v(-149.26, -139.55) * mm, "end": v(-148.15, -140) * mm});
            skLineSegment(sketch, "E900.170", {"start": v(-150.37, -139.1) * mm, "end": v(-149.26, -139.55) * mm});
            skLineSegment(sketch, "E900.171", {"start": v(-151.49, -138.65) * mm, "end": v(-150.37, -139.1) * mm});
            skLineSegment(sketch, "E900.172", {"start": v(-152.6, -138.2) * mm, "end": v(-151.49, -138.65) * mm});
            skLineSegment(sketch, "E900.173", {"start": v(-153.72, -137.73) * mm, "end": v(-152.6, -138.2) * mm});
            skLineSegment(sketch, "E900.174", {"start": v(-154.83, -137.27) * mm, "end": v(-153.72, -137.73) * mm});
            skLineSegment(sketch, "E900.175", {"start": v(-155.94, -136.8) * mm, "end": v(-154.83, -137.27) * mm});
            skLineSegment(sketch, "E900.176", {"start": v(-157.06, -136.34) * mm, "end": v(-155.94, -136.8) * mm});
            skLineSegment(sketch, "E900.177", {"start": v(-158.17, -135.87) * mm, "end": v(-157.06, -136.34) * mm});
            skLineSegment(sketch, "E900.178", {"start": v(-159.28, -135.39) * mm, "end": v(-158.17, -135.87) * mm});
            skLineSegment(sketch, "E900.179", {"start": v(-160.4, -134.91) * mm, "end": v(-159.28, -135.39) * mm});
            skLineSegment(sketch, "E900.180", {"start": v(-161.5, -134.43) * mm, "end": v(-160.4, -134.91) * mm});
            skLineSegment(sketch, "E900.181", {"start": v(-162.62, -133.94) * mm, "end": v(-161.5, -134.43) * mm});
            skLineSegment(sketch, "E900.182", {"start": v(-163.74, -133.46) * mm, "end": v(-162.62, -133.94) * mm});
            skLineSegment(sketch, "E900.183", {"start": v(-164.85, -132.96) * mm, "end": v(-163.74, -133.46) * mm});
            skLineSegment(sketch, "E900.184", {"start": v(-165.96, -132.47) * mm, "end": v(-164.85, -132.96) * mm});
            skLineSegment(sketch, "E900.185", {"start": v(-167.08, -131.97) * mm, "end": v(-165.96, -132.47) * mm});
            skLineSegment(sketch, "E900.186", {"start": v(-168.19, -131.47) * mm, "end": v(-167.08, -131.97) * mm});
            skLineSegment(sketch, "E900.187", {"start": v(-169.3, -130.96) * mm, "end": v(-168.19, -131.47) * mm});
            skLineSegment(sketch, "E900.188", {"start": v(-170.42, -130.45) * mm, "end": v(-169.3, -130.96) * mm});
            skLineSegment(sketch, "E900.189", {"start": v(-171.53, -129.94) * mm, "end": v(-170.42, -130.45) * mm});
            skLineSegment(sketch, "E900.190", {"start": v(-172.64, -129.43) * mm, "end": v(-171.53, -129.94) * mm});
            skLineSegment(sketch, "E900.191", {"start": v(-173.76, -128.9) * mm, "end": v(-172.64, -129.43) * mm});
            skLineSegment(sketch, "E900.192", {"start": v(-174.87, -128.39) * mm, "end": v(-173.76, -128.9) * mm});
            skLineSegment(sketch, "E900.193", {"start": v(-175.98, -127.86) * mm, "end": v(-174.87, -128.39) * mm});
            skLineSegment(sketch, "E900.194", {"start": v(-177.1, -127.33) * mm, "end": v(-175.98, -127.86) * mm});
            skLineSegment(sketch, "E900.195", {"start": v(-178.2, -126.8) * mm, "end": v(-177.1, -127.33) * mm});
            skLineSegment(sketch, "E900.196", {"start": v(-179.32, -126.26) * mm, "end": v(-178.2, -126.8) * mm});
            skLineSegment(sketch, "E900.197", {"start": v(-180.44, -125.73) * mm, "end": v(-179.32, -126.26) * mm});
            skLineSegment(sketch, "E900.198", {"start": v(-181.55, -125.18) * mm, "end": v(-180.44, -125.73) * mm});
            skLineSegment(sketch, "E900.199", {"start": v(-182.66, -124.64) * mm, "end": v(-181.55, -125.18) * mm});
            skLineSegment(sketch, "E900.200", {"start": v(-183.78, -124.1) * mm, "end": v(-182.66, -124.64) * mm});
            skLineSegment(sketch, "E900.201", {"start": v(-184.89, -123.54) * mm, "end": v(-183.78, -124.1) * mm});
            skLineSegment(sketch, "E900.202", {"start": v(-186, -122.98) * mm, "end": v(-184.89, -123.54) * mm});
            skLineSegment(sketch, "E900.203", {"start": v(-187.12, -122.42) * mm, "end": v(-186, -122.98) * mm});
            skLineSegment(sketch, "E900.204", {"start": v(-188.23, -121.86) * mm, "end": v(-187.12, -122.42) * mm});
            skLineSegment(sketch, "E900.205", {"start": v(-189.34, -121.3) * mm, "end": v(-188.23, -121.86) * mm});
            skLineSegment(sketch, "E900.206", {"start": v(-190.46, -120.73) * mm, "end": v(-189.34, -121.3) * mm});
            skLineSegment(sketch, "E900.207", {"start": v(-191.57, -120.16) * mm, "end": v(-190.46, -120.73) * mm});
            skLineSegment(sketch, "E900.208", {"start": v(-192.68, -119.58) * mm, "end": v(-191.57, -120.16) * mm});
            skLineSegment(sketch, "E900.209", {"start": v(-193.8, -119) * mm, "end": v(-192.68, -119.58) * mm});
            skLineSegment(sketch, "E900.210", {"start": v(-194.9, -118.42) * mm, "end": v(-193.8, -119) * mm});
            skLineSegment(sketch, "E900.211", {"start": v(-196.02, -117.84) * mm, "end": v(-194.9, -118.42) * mm});
            skLineSegment(sketch, "E900.212", {"start": v(-197.13, -117.25) * mm, "end": v(-196.02, -117.84) * mm});
            skLineSegment(sketch, "E900.213", {"start": v(-198.25, -116.66) * mm, "end": v(-197.13, -117.25) * mm});
            skLineSegment(sketch, "E900.214", {"start": v(-199.36, -116.06) * mm, "end": v(-198.25, -116.66) * mm});
            skLineSegment(sketch, "E900.215", {"start": v(-200.47, -115.46) * mm, "end": v(-199.36, -116.06) * mm});
            skLineSegment(sketch, "E900.216", {"start": v(-201.59, -114.86) * mm, "end": v(-200.47, -115.46) * mm});
            skLineSegment(sketch, "E900.217", {"start": v(-202.7, -114.26) * mm, "end": v(-201.59, -114.86) * mm});
            skLineSegment(sketch, "E900.218", {"start": v(-203.81, -113.65) * mm, "end": v(-202.7, -114.26) * mm});
            skLineSegment(sketch, "E900.219", {"start": v(-204.93, -113.03) * mm, "end": v(-203.81, -113.65) * mm});
            skLineSegment(sketch, "E900.220", {"start": v(-206.04, -112.42) * mm, "end": v(-204.93, -113.03) * mm});
            skLineSegment(sketch, "E900.221", {"start": v(-207.15, -111.8) * mm, "end": v(-206.04, -112.42) * mm});
            skLineSegment(sketch, "E900.222", {"start": v(-208.27, -111.18) * mm, "end": v(-207.15, -111.8) * mm});
            skLineSegment(sketch, "E900.223", {"start": v(-209.38, -110.55) * mm, "end": v(-208.27, -111.18) * mm});
            skLineSegment(sketch, "E900.224", {"start": v(-210.5, -109.93) * mm, "end": v(-209.38, -110.55) * mm});
            skLineSegment(sketch, "E900.225", {"start": v(-211.6, -109.3) * mm, "end": v(-210.5, -109.93) * mm});
            skLineSegment(sketch, "E900.226", {"start": v(-212.72, -108.66) * mm, "end": v(-211.6, -109.3) * mm});
            skLineSegment(sketch, "E900.227", {"start": v(-213.83, -108.02) * mm, "end": v(-212.72, -108.66) * mm});
            skLineSegment(sketch, "E900.228", {"start": v(-214.94, -107.38) * mm, "end": v(-213.83, -108.02) * mm});
            skLineSegment(sketch, "E900.229", {"start": v(-216.06, -106.73) * mm, "end": v(-214.94, -107.38) * mm});
            skLineSegment(sketch, "E900.230", {"start": v(-217.17, -106.08) * mm, "end": v(-216.06, -106.73) * mm});
            skLineSegment(sketch, "E900.231", {"start": v(-218.28, -105.43) * mm, "end": v(-217.17, -106.08) * mm});
            skLineSegment(sketch, "E900.232", {"start": v(-219.4, -104.78) * mm, "end": v(-218.28, -105.43) * mm});
            skLineSegment(sketch, "E900.233", {"start": v(-220.51, -104.12) * mm, "end": v(-219.4, -104.78) * mm});
            skLineSegment(sketch, "E900.234", {"start": v(-221.62, -103.46) * mm, "end": v(-220.51, -104.12) * mm});
            skLineSegment(sketch, "E900.235", {"start": v(-222.74, -102.8) * mm, "end": v(-221.62, -103.46) * mm});
            skLineSegment(sketch, "E900.236", {"start": v(-223.85, -102.12) * mm, "end": v(-222.74, -102.8) * mm});
            skLineSegment(sketch, "E900.237", {"start": v(-224.96, -101.45) * mm, "end": v(-223.85, -102.12) * mm});
            skLineSegment(sketch, "E900.238", {"start": v(-226.08, -100.78) * mm, "end": v(-224.96, -101.45) * mm});
            skLineSegment(sketch, "E900.239", {"start": v(-227.19, -100.1) * mm, "end": v(-226.08, -100.78) * mm});
            skLineSegment(sketch, "E900.240", {"start": v(-228.3, -99.42) * mm, "end": v(-227.19, -100.1) * mm});
            skLineSegment(sketch, "E900.241", {"start": v(-229.41, -98.73) * mm, "end": v(-228.3, -99.42) * mm});
            skLineSegment(sketch, "E900.242", {"start": v(-230.53, -98.04) * mm, "end": v(-229.41, -98.73) * mm});
            skLineSegment(sketch, "E900.243", {"start": v(-231.64, -97.35) * mm, "end": v(-230.53, -98.04) * mm});
            skLineSegment(sketch, "E900.244", {"start": v(-232.75, -96.66) * mm, "end": v(-231.64, -97.35) * mm});
            skLineSegment(sketch, "E900.245", {"start": v(-233.87, -95.96) * mm, "end": v(-232.75, -96.66) * mm});
            skLineSegment(sketch, "E900.246", {"start": v(-234.98, -95.26) * mm, "end": v(-233.87, -95.96) * mm});
            skLineSegment(sketch, "E900.247", {"start": v(-236.1, -94.55) * mm, "end": v(-234.98, -95.26) * mm});
            skLineSegment(sketch, "E900.248", {"start": v(-237.2, -93.84) * mm, "end": v(-236.1, -94.55) * mm});
            skLineSegment(sketch, "E900.249", {"start": v(-238.32, -93.13) * mm, "end": v(-237.2, -93.84) * mm});
            skLineSegment(sketch, "E900.250", {"start": v(-239.43, -92.42) * mm, "end": v(-238.32, -93.13) * mm});
            skLineSegment(sketch, "E900.251", {"start": v(-240.54, -91.7) * mm, "end": v(-239.43, -92.42) * mm});
            skLineSegment(sketch, "E900.252", {"start": v(-241.66, -90.98) * mm, "end": v(-240.54, -91.7) * mm});
            skLineSegment(sketch, "E900.253", {"start": v(-242.77, -90.25) * mm, "end": v(-241.66, -90.98) * mm});
            skLineSegment(sketch, "E900.254", {"start": v(-243.88, -89.52) * mm, "end": v(-242.77, -90.25) * mm});
            skLineSegment(sketch, "E900.255", {"start": v(-245, -88.79) * mm, "end": v(-243.88, -89.52) * mm});
            skLineSegment(sketch, "E900.256", {"start": v(-246.1, -88.05) * mm, "end": v(-245, -88.79) * mm});
            skLineSegment(sketch, "E900.257", {"start": v(-247.22, -87.32) * mm, "end": v(-246.1, -88.05) * mm});
            skLineSegment(sketch, "E900.258", {"start": v(-248.33, -86.57) * mm, "end": v(-247.22, -87.32) * mm});
            skLineSegment(sketch, "E900.259", {"start": v(-249.45, -85.83) * mm, "end": v(-248.33, -86.57) * mm});
            skLineSegment(sketch, "E900.260", {"start": v(-250.56, -85.08) * mm, "end": v(-249.45, -85.83) * mm});
            skLineSegment(sketch, "E900.261", {"start": v(-251.67, -84.33) * mm, "end": v(-250.56, -85.08) * mm});
            skLineSegment(sketch, "E900.262", {"start": v(-252.78, -83.57) * mm, "end": v(-251.67, -84.33) * mm});
            skLineSegment(sketch, "E900.263", {"start": v(-253.9, -82.82) * mm, "end": v(-252.78, -83.57) * mm});
            skLineSegment(sketch, "E900.264", {"start": v(-255.01, -82.05) * mm, "end": v(-253.9, -82.82) * mm});
            skLineSegment(sketch, "E900.265", {"start": v(-256.12, -81.29) * mm, "end": v(-255.01, -82.05) * mm});
            skLineSegment(sketch, "E900.266", {"start": v(-257.24, -80.52) * mm, "end": v(-256.12, -81.29) * mm});
            skLineSegment(sketch, "E900.267", {"start": v(-258.35, -79.75) * mm, "end": v(-257.24, -80.52) * mm});
            skLineSegment(sketch, "E900.268", {"start": v(-259.46, -78.97) * mm, "end": v(-258.35, -79.75) * mm});
            skLineSegment(sketch, "E900.269", {"start": v(-260.57, -78.2) * mm, "end": v(-259.46, -78.97) * mm});
            skLineSegment(sketch, "E900.270", {"start": v(-261.69, -77.41) * mm, "end": v(-260.57, -78.2) * mm});
            skLineSegment(sketch, "E900.271", {"start": v(-262.8, -76.63) * mm, "end": v(-261.69, -77.41) * mm});
            skLineSegment(sketch, "E900.272", {"start": v(-263.91, -75.84) * mm, "end": v(-262.8, -76.63) * mm});
            skLineSegment(sketch, "E900.273", {"start": v(-265.02, -75.05) * mm, "end": v(-263.91, -75.84) * mm});
            skLineSegment(sketch, "E900.274", {"start": v(-266.14, -74.25) * mm, "end": v(-265.02, -75.05) * mm});
            skLineSegment(sketch, "E900.275", {"start": v(-267.25, -73.46) * mm, "end": v(-266.14, -74.25) * mm});
            skLineSegment(sketch, "E900.276", {"start": v(-268.36, -72.65) * mm, "end": v(-267.25, -73.46) * mm});
            skLineSegment(sketch, "E900.277", {"start": v(-269.48, -71.85) * mm, "end": v(-268.36, -72.65) * mm});
            skLineSegment(sketch, "E900.278", {"start": v(-270.59, -71.04) * mm, "end": v(-269.48, -71.85) * mm});
            skLineSegment(sketch, "E900.279", {"start": v(-271.7, -70.23) * mm, "end": v(-270.59, -71.04) * mm});
            skLineSegment(sketch, "E900.280", {"start": v(-272.81, -69.41) * mm, "end": v(-271.7, -70.23) * mm});
            skLineSegment(sketch, "E900.281", {"start": v(-273.93, -68.6) * mm, "end": v(-272.81, -69.41) * mm});
            skLineSegment(sketch, "E900.282", {"start": v(-275.04, -67.77) * mm, "end": v(-273.93, -68.6) * mm});
            skLineSegment(sketch, "E900.283", {"start": v(-276.15, -66.95) * mm, "end": v(-275.04, -67.77) * mm});
            skLineSegment(sketch, "E900.284", {"start": v(-277.26, -66.12) * mm, "end": v(-276.15, -66.95) * mm});
            skLineSegment(sketch, "E900.285", {"start": v(-278.38, -65.3) * mm, "end": v(-277.26, -66.12) * mm});
            skLineSegment(sketch, "E900.286", {"start": v(-279.49, -64.46) * mm, "end": v(-278.38, -65.3) * mm});
            skLineSegment(sketch, "E900.287", {"start": v(-280.6, -63.62) * mm, "end": v(-279.49, -64.46) * mm});
            skLineSegment(sketch, "E900.288", {"start": v(-395.17, 40.54) * mm, "end": v(-394.06, 39.36) * mm});
            skLineSegment(sketch, "E900.289", {"start": v(-396.28, 41.73) * mm, "end": v(-395.17, 40.54) * mm});
            skLineSegment(sketch, "E900.290", {"start": v(-397.4, 42.92) * mm, "end": v(-396.28, 41.73) * mm});
            skLineSegment(sketch, "E900.291", {"start": v(-398.5, 44.1) * mm, "end": v(-397.4, 42.92) * mm});
            skLineSegment(sketch, "E900.292", {"start": v(-399.62, 45.3) * mm, "end": v(-398.5, 44.1) * mm});
            skLineSegment(sketch, "E900.293", {"start": v(-400.73, 46.5) * mm, "end": v(-399.62, 45.3) * mm});
            skLineSegment(sketch, "E900.294", {"start": v(-401.85, 47.7) * mm, "end": v(-400.73, 46.5) * mm});
            skLineSegment(sketch, "E900.295", {"start": v(-402.96, 48.9) * mm, "end": v(-401.85, 47.7) * mm});
            skLineSegment(sketch, "E900.296", {"start": v(-404.07, 50.11) * mm, "end": v(-402.96, 48.9) * mm});
            skLineSegment(sketch, "E900.297", {"start": v(-405.18, 51.32) * mm, "end": v(-404.07, 50.11) * mm});
            skLineSegment(sketch, "E900.298", {"start": v(-406.3, 52.54) * mm, "end": v(-405.18, 51.32) * mm});
            skLineSegment(sketch, "E900.299", {"start": v(-407.4, 53.75) * mm, "end": v(-406.3, 52.54) * mm});
            skLineSegment(sketch, "E900.300", {"start": v(-408.52, 54.97) * mm, "end": v(-407.4, 53.75) * mm});
            skLineSegment(sketch, "E900.301", {"start": v(-409.63, 56.2) * mm, "end": v(-408.52, 54.97) * mm});
            skLineSegment(sketch, "E900.302", {"start": v(-410.74, 57.43) * mm, "end": v(-409.63, 56.2) * mm});
            skLineSegment(sketch, "E900.303", {"start": v(-411.85, 58.66) * mm, "end": v(-410.74, 57.43) * mm});
            skLineSegment(sketch, "E900.304", {"start": v(-412.97, 59.9) * mm, "end": v(-411.85, 58.66) * mm});
            skLineSegment(sketch, "E900.305", {"start": v(-414.08, 61.13) * mm, "end": v(-412.97, 59.9) * mm});
            skLineSegment(sketch, "E900.306", {"start": v(-415.19, 62.37) * mm, "end": v(-414.08, 61.13) * mm});
            skLineSegment(sketch, "E900.307", {"start": v(-416.3, 63.61) * mm, "end": v(-415.19, 62.37) * mm});
            skLineSegment(sketch, "E900.308", {"start": v(-417.41, 64.86) * mm, "end": v(-416.3, 63.61) * mm});
            skLineSegment(sketch, "E900.309", {"start": v(-418.53, 66.11) * mm, "end": v(-417.41, 64.86) * mm});
            skLineSegment(sketch, "E900.310", {"start": v(-419.64, 67.37) * mm, "end": v(-418.53, 66.11) * mm});
            skLineSegment(sketch, "E900.311", {"start": v(-420.75, 68.62) * mm, "end": v(-419.64, 67.37) * mm});
            skLineSegment(sketch, "E900.312", {"start": v(-421.86, 69.88) * mm, "end": v(-420.75, 68.62) * mm});
            skLineSegment(sketch, "E900.313", {"start": v(-422.97, 71.15) * mm, "end": v(-421.86, 69.88) * mm});
            skLineSegment(sketch, "E900.314", {"start": v(-424.09, 72.42) * mm, "end": v(-422.97, 71.15) * mm});
            skLineSegment(sketch, "E900.315", {"start": v(-425.2, 73.69) * mm, "end": v(-424.09, 72.42) * mm});
            skLineSegment(sketch, "E900.316", {"start": v(-426.3, 74.96) * mm, "end": v(-425.2, 73.69) * mm});
            skLineSegment(sketch, "E900.317", {"start": v(-427.42, 76.24) * mm, "end": v(-426.3, 74.96) * mm});
            skLineSegment(sketch, "E900.318", {"start": v(-428.53, 77.52) * mm, "end": v(-427.42, 76.24) * mm});
            skLineSegment(sketch, "E900.319", {"start": v(-429.65, 78.8) * mm, "end": v(-428.53, 77.52) * mm});
            skLineSegment(sketch, "E900.320", {"start": v(-430.76, 80.09) * mm, "end": v(-429.65, 78.8) * mm});
            skLineSegment(sketch, "E900.321", {"start": v(-431.87, 81.38) * mm, "end": v(-430.76, 80.09) * mm});
            skLineSegment(sketch, "E900.322", {"start": v(-432.98, 82.67) * mm, "end": v(-431.87, 81.38) * mm});
            skLineSegment(sketch, "E900.323", {"start": v(-434.1, 83.97) * mm, "end": v(-432.98, 82.67) * mm});
            skLineSegment(sketch, "E900.324", {"start": v(-435.2, 85.27) * mm, "end": v(-434.1, 83.97) * mm});
            skLineSegment(sketch, "E900.325", {"start": v(-436.32, 86.58) * mm, "end": v(-435.2, 85.27) * mm});
            skLineSegment(sketch, "E900.326", {"start": v(-437.43, 87.88) * mm, "end": v(-436.32, 86.58) * mm});
            skLineSegment(sketch, "E900.327", {"start": v(-438.54, 89.2) * mm, "end": v(-437.43, 87.88) * mm});
            skLineSegment(sketch, "E900.328", {"start": v(-439.65, 90.5) * mm, "end": v(-438.54, 89.2) * mm});
            skLineSegment(sketch, "E900.329", {"start": v(-440.76, 91.83) * mm, "end": v(-439.65, 90.5) * mm});
            skLineSegment(sketch, "E900.330", {"start": v(-441.88, 93.15) * mm, "end": v(-440.76, 91.83) * mm});
            skLineSegment(sketch, "E900.331", {"start": v(-442.99, 94.47) * mm, "end": v(-441.88, 93.15) * mm});
            skLineSegment(sketch, "E900.332", {"start": v(-444.1, 95.8) * mm, "end": v(-442.99, 94.47) * mm});
            skLineSegment(sketch, "E900.333", {"start": v(-445.21, 97.13) * mm, "end": v(-444.1, 95.8) * mm});
            skLineSegment(sketch, "E900.334", {"start": v(-446.32, 98.46) * mm, "end": v(-445.21, 97.13) * mm});
            skLineSegment(sketch, "E900.335", {"start": v(-447.44, 99.8) * mm, "end": v(-446.32, 98.46) * mm});
            skLineSegment(sketch, "E900.336", {"start": v(-448.55, 101.14) * mm, "end": v(-447.44, 99.8) * mm});
            skLineSegment(sketch, "E900.337", {"start": v(-449.66, 102.48) * mm, "end": v(-448.55, 101.14) * mm});
            skLineSegment(sketch, "E900.338", {"start": v(-477.46, 137.16) * mm, "end": v(-476.34, 135.74) * mm});
            skLineSegment(sketch, "E900.339", {"start": v(-478.57, 138.6) * mm, "end": v(-477.46, 137.16) * mm});
            skLineSegment(sketch, "E900.340", {"start": v(-479.68, 140.03) * mm, "end": v(-478.57, 138.6) * mm});
            skLineSegment(sketch, "E900.341", {"start": v(-480.8, 141.47) * mm, "end": v(-479.68, 140.03) * mm});
            skLineSegment(sketch, "E900.342", {"start": v(-481.9, 142.9) * mm, "end": v(-480.8, 141.47) * mm});
            skLineSegment(sketch, "E900.343", {"start": v(-483.01, 144.35) * mm, "end": v(-481.9, 142.9) * mm});
            skLineSegment(sketch, "E900.344", {"start": v(-484.13, 145.8) * mm, "end": v(-483.01, 144.35) * mm});
            skLineSegment(sketch, "E900.345", {"start": v(-485.24, 147.25) * mm, "end": v(-484.13, 145.8) * mm});
            skLineSegment(sketch, "E900.346", {"start": v(-486.35, 148.7) * mm, "end": v(-485.24, 147.25) * mm});
            skLineSegment(sketch, "E900.347", {"start": v(-487.46, 150.16) * mm, "end": v(-486.35, 148.7) * mm});
            skLineSegment(sketch, "E900.348", {"start": v(-488.57, 151.62) * mm, "end": v(-487.46, 150.16) * mm});
            skLineSegment(sketch, "E900.349", {"start": v(-489.69, 153.08) * mm, "end": v(-488.57, 151.62) * mm});
            skLineSegment(sketch, "E900.350", {"start": v(-497.47, 163.42) * mm, "end": v(-496.36, 161.93) * mm});
            skLineSegment(sketch, "E900.351", {"start": v(-498.58, 164.91) * mm, "end": v(-497.47, 163.42) * mm});
            skLineSegment(sketch, "E900.352", {"start": v(-499.7, 166.4) * mm, "end": v(-498.58, 164.91) * mm});
            skLineSegment(sketch, "E900.353", {"start": v(-500.8, 167.9) * mm, "end": v(-499.7, 166.4) * mm});
            skLineSegment(sketch, "E900.354", {"start": v(-496.36, 161.93) * mm, "end": v(-495.24, 160.45) * mm});
            skLineSegment(sketch, "E900.355", {"start": v(-495.24, 160.45) * mm, "end": v(-494.13, 158.97) * mm});
            skLineSegment(sketch, "E900.356", {"start": v(-494.13, 158.97) * mm, "end": v(-493.02, 157.5) * mm});
            skLineSegment(sketch, "E900.357", {"start": v(-493.02, 157.5) * mm, "end": v(-491.9, 156.02) * mm});
            skLineSegment(sketch, "E900.358", {"start": v(-491.9, 156.02) * mm, "end": v(-490.8, 154.55) * mm});
            skLineSegment(sketch, "E900.359", {"start": v(-490.8, 154.55) * mm, "end": v(-489.69, 153.08) * mm});
            skLineSegment(sketch, "E900.360", {"start": v(-476.34, 135.74) * mm, "end": v(-475.23, 134.31) * mm});
            skLineSegment(sketch, "E900.361", {"start": v(-475.23, 134.31) * mm, "end": v(-474.12, 132.9) * mm});
            skLineSegment(sketch, "E900.362", {"start": v(-474.12, 132.9) * mm, "end": v(-473, 131.48) * mm});
            skLineSegment(sketch, "E900.363", {"start": v(-473, 131.48) * mm, "end": v(-471.9, 130.06) * mm});
            skLineSegment(sketch, "E900.364", {"start": v(-471.9, 130.06) * mm, "end": v(-470.78, 128.65) * mm});
            skLineSegment(sketch, "E900.365", {"start": v(-470.78, 128.65) * mm, "end": v(-469.67, 127.24) * mm});
            skLineSegment(sketch, "E900.366", {"start": v(-469.67, 127.24) * mm, "end": v(-468.56, 125.84) * mm});
            skLineSegment(sketch, "E900.367", {"start": v(-468.56, 125.84) * mm, "end": v(-467.45, 124.44) * mm});
            skLineSegment(sketch, "E900.368", {"start": v(-467.45, 124.44) * mm, "end": v(-466.34, 123.04) * mm});
            skLineSegment(sketch, "E900.369", {"start": v(-466.34, 123.04) * mm, "end": v(-465.23, 121.65) * mm});
            skLineSegment(sketch, "E900.370", {"start": v(-465.23, 121.65) * mm, "end": v(-464.11, 120.26) * mm});
            skLineSegment(sketch, "E900.371", {"start": v(-464.11, 120.26) * mm, "end": v(-463, 118.87) * mm});
            skLineSegment(sketch, "E900.372", {"start": v(-463, 118.87) * mm, "end": v(-461.9, 117.49) * mm});
            skLineSegment(sketch, "E900.373", {"start": v(-461.9, 117.49) * mm, "end": v(-460.78, 116.1) * mm});
            skLineSegment(sketch, "E900.374", {"start": v(-460.78, 116.1) * mm, "end": v(-459.67, 114.73) * mm});
            skLineSegment(sketch, "E900.375", {"start": v(-459.67, 114.73) * mm, "end": v(-458.55, 113.36) * mm});
            skLineSegment(sketch, "E900.376", {"start": v(-458.55, 113.36) * mm, "end": v(-457.44, 111.99) * mm});
            skLineSegment(sketch, "E900.377", {"start": v(-457.44, 111.99) * mm, "end": v(-456.33, 110.62) * mm});
            skLineSegment(sketch, "E900.378", {"start": v(-456.33, 110.62) * mm, "end": v(-455.22, 109.25) * mm});
            skLineSegment(sketch, "E900.379", {"start": v(-455.22, 109.25) * mm, "end": v(-454.1, 107.9) * mm});
            skLineSegment(sketch, "E900.380", {"start": v(-454.1, 107.9) * mm, "end": v(-453, 106.54) * mm});
            skLineSegment(sketch, "E900.381", {"start": v(-453, 106.54) * mm, "end": v(-451.88, 105.18) * mm});
            skLineSegment(sketch, "E900.382", {"start": v(-451.88, 105.18) * mm, "end": v(-450.77, 103.83) * mm});
            skLineSegment(sketch, "E900.383", {"start": v(-450.77, 103.83) * mm, "end": v(-449.66, 102.48) * mm});
            skLineSegment(sketch, "E900.384", {"start": v(-394.06, 39.36) * mm, "end": v(-392.95, 38.18) * mm});
            skLineSegment(sketch, "E900.385", {"start": v(-392.95, 38.18) * mm, "end": v(-391.84, 37.01) * mm});
            skLineSegment(sketch, "E900.386", {"start": v(-391.84, 37.01) * mm, "end": v(-390.72, 35.84) * mm});
            skLineSegment(sketch, "E900.387", {"start": v(-390.72, 35.84) * mm, "end": v(-389.61, 34.67) * mm});
            skLineSegment(sketch, "E900.388", {"start": v(-389.61, 34.67) * mm, "end": v(-388.5, 33.5) * mm});
            skLineSegment(sketch, "E900.389", {"start": v(-388.5, 33.5) * mm, "end": v(-387.39, 32.35) * mm});
            skLineSegment(sketch, "E900.390", {"start": v(-387.39, 32.35) * mm, "end": v(-386.28, 31.19) * mm});
            skLineSegment(sketch, "E900.391", {"start": v(-386.28, 31.19) * mm, "end": v(-385.16, 30.03) * mm});
            skLineSegment(sketch, "E900.392", {"start": v(-385.16, 30.03) * mm, "end": v(-384.05, 28.88) * mm});
            skLineSegment(sketch, "E900.393", {"start": v(-384.05, 28.88) * mm, "end": v(-382.94, 27.74) * mm});
            skLineSegment(sketch, "E900.394", {"start": v(-382.94, 27.74) * mm, "end": v(-381.83, 26.6) * mm});
            skLineSegment(sketch, "E900.395", {"start": v(-381.83, 26.6) * mm, "end": v(-380.72, 25.45) * mm});
            skLineSegment(sketch, "E900.396", {"start": v(-380.72, 25.45) * mm, "end": v(-379.6, 24.31) * mm});
            skLineSegment(sketch, "E900.397", {"start": v(-379.6, 24.31) * mm, "end": v(-378.5, 23.18) * mm});
            skLineSegment(sketch, "E900.398", {"start": v(-378.5, 23.18) * mm, "end": v(-377.38, 22.05) * mm});
            skLineSegment(sketch, "E900.399", {"start": v(-377.38, 22.05) * mm, "end": v(-376.27, 20.92) * mm});
            skLineSegment(sketch, "E900.400", {"start": v(-376.27, 20.92) * mm, "end": v(-375.15, 19.8) * mm});
            skLineSegment(sketch, "E900.401", {"start": v(-375.15, 19.8) * mm, "end": v(-374.04, 18.67) * mm});
            skLineSegment(sketch, "E900.402", {"start": v(-374.04, 18.67) * mm, "end": v(-372.93, 17.56) * mm});
            skLineSegment(sketch, "E900.403", {"start": v(-372.93, 17.56) * mm, "end": v(-371.82, 16.44) * mm});
            skLineSegment(sketch, "E900.404", {"start": v(-371.82, 16.44) * mm, "end": v(-370.7, 15.33) * mm});
            skLineSegment(sketch, "E900.405", {"start": v(-370.7, 15.33) * mm, "end": v(-369.6, 14.22) * mm});
            skLineSegment(sketch, "E900.406", {"start": v(-369.6, 14.22) * mm, "end": v(-368.48, 13.12) * mm});
            skLineSegment(sketch, "E900.407", {"start": v(-368.48, 13.12) * mm, "end": v(-367.37, 12.02) * mm});
            skLineSegment(sketch, "E900.408", {"start": v(-367.37, 12.02) * mm, "end": v(-366.26, 10.92) * mm});
            skLineSegment(sketch, "E900.409", {"start": v(-366.26, 10.92) * mm, "end": v(-365.15, 9.83) * mm});
            skLineSegment(sketch, "E900.410", {"start": v(-365.15, 9.83) * mm, "end": v(-364.03, 8.73) * mm});
            skLineSegment(sketch, "E900.411", {"start": v(-364.03, 8.73) * mm, "end": v(-362.92, 7.65) * mm});
            skLineSegment(sketch, "E900.412", {"start": v(-362.92, 7.65) * mm, "end": v(-361.8, 6.56) * mm});
            skLineSegment(sketch, "E900.413", {"start": v(-361.8, 6.56) * mm, "end": v(-360.7, 5.48) * mm});
            skLineSegment(sketch, "E900.414", {"start": v(-360.7, 5.48) * mm, "end": v(-359.58, 4.4) * mm});
            skLineSegment(sketch, "E900.415", {"start": v(-359.58, 4.4) * mm, "end": v(-358.47, 3.33) * mm});
            skLineSegment(sketch, "E900.416", {"start": v(-358.47, 3.33) * mm, "end": v(-357.36, 2.26) * mm});
            skLineSegment(sketch, "E900.417", {"start": v(-357.36, 2.26) * mm, "end": v(-356.25, 1.19) * mm});
            skLineSegment(sketch, "E900.418", {"start": v(-356.25, 1.19) * mm, "end": v(-355.14, 0.13) * mm});
            skLineSegment(sketch, "E900.419", {"start": v(-355.14, 0.13) * mm, "end": v(-354.02, -0.94) * mm});
            skLineSegment(sketch, "E900.420", {"start": v(-354.02, -0.94) * mm, "end": v(-352.91, -2) * mm});
            skLineSegment(sketch, "E900.421", {"start": v(-352.91, -2) * mm, "end": v(-351.8, -3.05) * mm});
            skLineSegment(sketch, "E900.422", {"start": v(-351.8, -3.05) * mm, "end": v(-350.69, -4.1) * mm});
            skLineSegment(sketch, "E900.423", {"start": v(-350.69, -4.1) * mm, "end": v(-349.57, -5.15) * mm});
            skLineSegment(sketch, "E900.424", {"start": v(-349.57, -5.15) * mm, "end": v(-348.46, -6.2) * mm});
            skLineSegment(sketch, "E900.425", {"start": v(-348.46, -6.2) * mm, "end": v(-347.35, -7.23) * mm});
            skLineSegment(sketch, "E900.426", {"start": v(-347.35, -7.23) * mm, "end": v(-346.24, -8.27) * mm});
            skLineSegment(sketch, "E900.427", {"start": v(-346.24, -8.27) * mm, "end": v(-345.12, -9.3) * mm});
            skLineSegment(sketch, "E900.428", {"start": v(-345.12, -9.3) * mm, "end": v(-344.01, -10.34) * mm});
            skLineSegment(sketch, "E900.429", {"start": v(-344.01, -10.34) * mm, "end": v(-342.9, -11.36) * mm});
            skLineSegment(sketch, "E900.430", {"start": v(-342.9, -11.36) * mm, "end": v(-341.79, -12.39) * mm});
            skLineSegment(sketch, "E900.431", {"start": v(-341.79, -12.39) * mm, "end": v(-340.68, -13.41) * mm});
            skLineSegment(sketch, "E900.432", {"start": v(-340.68, -13.41) * mm, "end": v(-339.56, -14.43) * mm});
            skLineSegment(sketch, "E900.433", {"start": v(-339.56, -14.43) * mm, "end": v(-338.45, -15.44) * mm});
            skLineSegment(sketch, "E900.434", {"start": v(-338.45, -15.44) * mm, "end": v(-337.34, -16.45) * mm});
            skLineSegment(sketch, "E900.435", {"start": v(-337.34, -16.45) * mm, "end": v(-336.23, -17.46) * mm});
            skLineSegment(sketch, "E900.436", {"start": v(-336.23, -17.46) * mm, "end": v(-335.11, -18.47) * mm});
            skLineSegment(sketch, "E900.437", {"start": v(-335.11, -18.47) * mm, "end": v(-334, -19.47) * mm});
            skLineSegment(sketch, "E900.438", {"start": v(-334, -19.47) * mm, "end": v(-332.89, -20.47) * mm});
            skLineSegment(sketch, "E900.439", {"start": v(-332.89, -20.47) * mm, "end": v(-331.78, -21.46) * mm});
            skLineSegment(sketch, "E900.440", {"start": v(-331.78, -21.46) * mm, "end": v(-330.66, -22.45) * mm});
            skLineSegment(sketch, "E900.441", {"start": v(-330.66, -22.45) * mm, "end": v(-329.55, -23.44) * mm});
            skLineSegment(sketch, "E900.442", {"start": v(-329.55, -23.44) * mm, "end": v(-328.44, -24.42) * mm});
            skLineSegment(sketch, "E900.443", {"start": v(-328.44, -24.42) * mm, "end": v(-327.33, -25.4) * mm});
            skLineSegment(sketch, "E900.444", {"start": v(-327.33, -25.4) * mm, "end": v(-326.22, -26.38) * mm});
            skLineSegment(sketch, "E900.445", {"start": v(-326.22, -26.38) * mm, "end": v(-325.1, -27.36) * mm});
            skLineSegment(sketch, "E900.446", {"start": v(-325.1, -27.36) * mm, "end": v(-324, -28.33) * mm});
            skLineSegment(sketch, "E900.447", {"start": v(-324, -28.33) * mm, "end": v(-322.88, -29.3) * mm});
            skLineSegment(sketch, "E900.448", {"start": v(-322.88, -29.3) * mm, "end": v(-321.77, -30.26) * mm});
            skLineSegment(sketch, "E900.449", {"start": v(-321.77, -30.26) * mm, "end": v(-320.65, -31.22) * mm});
            skLineSegment(sketch, "E900.450", {"start": v(-320.65, -31.22) * mm, "end": v(-319.54, -32.18) * mm});
            skLineSegment(sketch, "E900.451", {"start": v(-319.54, -32.18) * mm, "end": v(-318.43, -33.14) * mm});
            skLineSegment(sketch, "E900.452", {"start": v(-318.43, -33.14) * mm, "end": v(-317.32, -34.09) * mm});
            skLineSegment(sketch, "E900.453", {"start": v(-317.32, -34.09) * mm, "end": v(-316.2, -35.04) * mm});
            skLineSegment(sketch, "E900.454", {"start": v(-316.2, -35.04) * mm, "end": v(-315.1, -35.98) * mm});
            skLineSegment(sketch, "E900.455", {"start": v(-315.1, -35.98) * mm, "end": v(-313.98, -36.92) * mm});
            skLineSegment(sketch, "E900.456", {"start": v(-313.98, -36.92) * mm, "end": v(-312.87, -37.86) * mm});
            skLineSegment(sketch, "E900.457", {"start": v(-312.87, -37.86) * mm, "end": v(-311.75, -38.8) * mm});
            skLineSegment(sketch, "E900.458", {"start": v(-311.75, -38.8) * mm, "end": v(-310.64, -39.73) * mm});
            skLineSegment(sketch, "E900.459", {"start": v(-310.64, -39.73) * mm, "end": v(-309.53, -40.65) * mm});
            skLineSegment(sketch, "E900.460", {"start": v(-309.53, -40.65) * mm, "end": v(-308.42, -41.58) * mm});
            skLineSegment(sketch, "E900.461", {"start": v(-308.42, -41.58) * mm, "end": v(-307.3, -42.5) * mm});
            skLineSegment(sketch, "E900.462", {"start": v(-307.3, -42.5) * mm, "end": v(-306.2, -43.42) * mm});
            skLineSegment(sketch, "E900.463", {"start": v(-306.2, -43.42) * mm, "end": v(-305.08, -44.33) * mm});
            skLineSegment(sketch, "E900.464", {"start": v(-305.08, -44.33) * mm, "end": v(-303.97, -45.25) * mm});
            skLineSegment(sketch, "E900.465", {"start": v(-303.97, -45.25) * mm, "end": v(-302.85, -46.15) * mm});
            skLineSegment(sketch, "E900.466", {"start": v(-302.85, -46.15) * mm, "end": v(-301.74, -47.06) * mm});
            skLineSegment(sketch, "E900.467", {"start": v(-301.74, -47.06) * mm, "end": v(-300.63, -47.96) * mm});
            skLineSegment(sketch, "E900.468", {"start": v(-300.63, -47.96) * mm, "end": v(-299.52, -48.86) * mm});
            skLineSegment(sketch, "E900.469", {"start": v(-299.52, -48.86) * mm, "end": v(-298.4, -49.75) * mm});
            skLineSegment(sketch, "E900.470", {"start": v(-298.4, -49.75) * mm, "end": v(-297.3, -50.64) * mm});
            skLineSegment(sketch, "E900.471", {"start": v(-297.3, -50.64) * mm, "end": v(-296.18, -51.53) * mm});
            skLineSegment(sketch, "E900.472", {"start": v(-296.18, -51.53) * mm, "end": v(-295.07, -52.42) * mm});
            skLineSegment(sketch, "E900.473", {"start": v(-295.07, -52.42) * mm, "end": v(-293.95, -53.3) * mm});
            skLineSegment(sketch, "E900.474", {"start": v(-293.95, -53.3) * mm, "end": v(-292.84, -54.18) * mm});
            skLineSegment(sketch, "E900.475", {"start": v(-292.84, -54.18) * mm, "end": v(-291.73, -55.05) * mm});
            skLineSegment(sketch, "E900.476", {"start": v(-291.73, -55.05) * mm, "end": v(-290.62, -55.92) * mm});
            skLineSegment(sketch, "E900.477", {"start": v(-290.62, -55.92) * mm, "end": v(-289.5, -56.8) * mm});
            skLineSegment(sketch, "E900.478", {"start": v(-289.5, -56.8) * mm, "end": v(-288.4, -57.66) * mm});
            skLineSegment(sketch, "E900.479", {"start": v(-288.4, -57.66) * mm, "end": v(-287.28, -58.52) * mm});
            skLineSegment(sketch, "E900.480", {"start": v(-287.28, -58.52) * mm, "end": v(-286.17, -59.38) * mm});
            skLineSegment(sketch, "E900.481", {"start": v(-286.17, -59.38) * mm, "end": v(-285.05, -60.23) * mm});
            skLineSegment(sketch, "E900.482", {"start": v(-285.05, -60.23) * mm, "end": v(-283.94, -61.08) * mm});
            skLineSegment(sketch, "E900.483", {"start": v(-283.94, -61.08) * mm, "end": v(-282.83, -61.93) * mm});
            skLineSegment(sketch, "E900.484", {"start": v(-282.83, -61.93) * mm, "end": v(-281.72, -62.78) * mm});
            skLineSegment(sketch, "E900.485", {"start": v(-281.72, -62.78) * mm, "end": v(-280.6, -63.62) * mm});
            skLineSegment(sketch, "E900.486", {"start": v(-46.8, -166.56) * mm, "end": v(-45.68, -166.7) * mm});
            skLineSegment(sketch, "E900.487", {"start": v(-45.68, -166.7) * mm, "end": v(-44.56, -166.83) * mm});
            skLineSegment(sketch, "E900.488", {"start": v(-44.56, -166.83) * mm, "end": v(-43.45, -166.96) * mm});
            skLineSegment(sketch, "E900.489", {"start": v(-43.45, -166.96) * mm, "end": v(-42.34, -167.1) * mm});
            skLineSegment(sketch, "E900.490", {"start": v(-42.34, -167.1) * mm, "end": v(-41.22, -167.22) * mm});
            skLineSegment(sketch, "E900.491", {"start": v(-41.22, -167.22) * mm, "end": v(-40.1, -167.34) * mm});
            skLineSegment(sketch, "E900.492", {"start": v(-40.1, -167.34) * mm, "end": v(-39, -167.46) * mm});
            skLineSegment(sketch, "E900.493", {"start": v(-39, -167.46) * mm, "end": v(-37.88, -167.57) * mm});
            skLineSegment(sketch, "E900.494", {"start": v(-37.88, -167.57) * mm, "end": v(-36.76, -167.68) * mm});
            skLineSegment(sketch, "E900.495", {"start": v(-36.76, -167.68) * mm, "end": v(-35.65, -167.8) * mm});
            skLineSegment(sketch, "E900.496", {"start": v(-35.65, -167.8) * mm, "end": v(-34.54, -167.9) * mm});
            skLineSegment(sketch, "E900.497", {"start": v(-34.54, -167.9) * mm, "end": v(-33.42, -168) * mm});
            skLineSegment(sketch, "E900.498", {"start": v(-33.42, -168) * mm, "end": v(-32.3, -168.1) * mm});
            skLineSegment(sketch, "E900.499", {"start": v(-32.3, -168.1) * mm, "end": v(-31.2, -168.2) * mm});
            skLineSegment(sketch, "E900.500", {"start": v(-31.2, -168.2) * mm, "end": v(-30.08, -168.28) * mm});
            skLineSegment(sketch, "E900.501", {"start": v(-30.08, -168.28) * mm, "end": v(-28.97, -168.37) * mm});
            skLineSegment(sketch, "E900.502", {"start": v(-28.97, -168.37) * mm, "end": v(-27.85, -168.46) * mm});
            skLineSegment(sketch, "E900.503", {"start": v(-27.85, -168.46) * mm, "end": v(-26.74, -168.54) * mm});
            skLineSegment(sketch, "E900.504", {"start": v(-26.74, -168.54) * mm, "end": v(-25.62, -168.62) * mm});
            skLineSegment(sketch, "E900.505", {"start": v(-25.62, -168.62) * mm, "end": v(-24.51, -168.7) * mm});
            skLineSegment(sketch, "E900.506", {"start": v(-24.51, -168.7) * mm, "end": v(-23.4, -168.77) * mm});
            skLineSegment(sketch, "E900.507", {"start": v(-23.4, -168.77) * mm, "end": v(-22.28, -168.83) * mm});
            skLineSegment(sketch, "E900.508", {"start": v(-22.28, -168.83) * mm, "end": v(-21.17, -168.9) * mm});
            skLineSegment(sketch, "E900.509", {"start": v(-21.17, -168.9) * mm, "end": v(-20.05, -168.96) * mm});
            skLineSegment(sketch, "E900.510", {"start": v(-20.05, -168.96) * mm, "end": v(-18.94, -169.02) * mm});
            skLineSegment(sketch, "E900.511", {"start": v(-18.94, -169.02) * mm, "end": v(-17.83, -169.07) * mm});
            skLineSegment(sketch, "E900.512", {"start": v(-17.83, -169.07) * mm, "end": v(-16.71, -169.13) * mm});
            skLineSegment(sketch, "E900.513", {"start": v(-16.71, -169.13) * mm, "end": v(-15.6, -169.17) * mm});
            skLineSegment(sketch, "E900.514", {"start": v(-15.6, -169.17) * mm, "end": v(-14.48, -169.22) * mm});
            skLineSegment(sketch, "E900.515", {"start": v(-14.48, -169.22) * mm, "end": v(-13.37, -169.26) * mm});
            skLineSegment(sketch, "E900.516", {"start": v(-13.37, -169.26) * mm, "end": v(-12.26, -169.3) * mm});
            skLineSegment(sketch, "E900.517", {"start": v(-12.26, -169.3) * mm, "end": v(-11.14, -169.33) * mm});
            skLineSegment(sketch, "E900.518", {"start": v(-11.14, -169.33) * mm, "end": v(-10.03, -169.37) * mm});
            skLineSegment(sketch, "E900.519", {"start": v(-10.03, -169.37) * mm, "end": v(-8.91, -169.4) * mm});
            skLineSegment(sketch, "E900.520", {"start": v(-8.91, -169.4) * mm, "end": v(-7.8, -169.42) * mm});
            skLineSegment(sketch, "E900.521", {"start": v(-7.8, -169.42) * mm, "end": v(-6.68, -169.44) * mm});
            skLineSegment(sketch, "E900.522", {"start": v(-6.68, -169.44) * mm, "end": v(-5.57, -169.46) * mm});
            skLineSegment(sketch, "E900.523", {"start": v(-5.57, -169.46) * mm, "end": v(-4.46, -169.47) * mm});
            skLineSegment(sketch, "E900.524", {"start": v(-4.46, -169.47) * mm, "end": v(-3.34, -169.49) * mm});
            skLineSegment(sketch, "E900.525", {"start": v(-3.34, -169.49) * mm, "end": v(-2.23, -169.5) * mm});
            skLineSegment(sketch, "E900.526", {"start": v(-2.23, -169.5) * mm, "end": v(-1.11, -169.5) * mm});
            skLineSegment(sketch, "E900.527", {"start": v(-1.11, -169.5) * mm, "end": v(0, -169.5) * mm});
            skLineSegment(sketch, "E900.528", {"start": v(0, -169.5) * mm, "end": v(1.11, -169.5) * mm});
            skLineSegment(sketch, "E900.529", {"start": v(1.11, -169.5) * mm, "end": v(2.23, -169.5) * mm});
            skLineSegment(sketch, "E900.530", {"start": v(2.23, -169.5) * mm, "end": v(3.34, -169.49) * mm});
            skLineSegment(sketch, "E900.531", {"start": v(3.34, -169.49) * mm, "end": v(4.46, -169.47) * mm});
            skLineSegment(sketch, "E900.532", {"start": v(4.46, -169.47) * mm, "end": v(5.57, -169.46) * mm});
            skLineSegment(sketch, "E900.533", {"start": v(5.57, -169.46) * mm, "end": v(6.68, -169.44) * mm});
            skLineSegment(sketch, "E900.534", {"start": v(6.68, -169.44) * mm, "end": v(7.8, -169.42) * mm});
            skLineSegment(sketch, "E900.535", {"start": v(7.8, -169.42) * mm, "end": v(8.91, -169.4) * mm});
            skLineSegment(sketch, "E900.536", {"start": v(8.91, -169.4) * mm, "end": v(10.03, -169.37) * mm});
            skLineSegment(sketch, "E900.537", {"start": v(10.03, -169.37) * mm, "end": v(11.14, -169.33) * mm});
            skLineSegment(sketch, "E900.538", {"start": v(11.14, -169.33) * mm, "end": v(12.26, -169.3) * mm});
            skLineSegment(sketch, "E900.539", {"start": v(12.26, -169.3) * mm, "end": v(13.37, -169.26) * mm});
            skLineSegment(sketch, "E900.540", {"start": v(13.37, -169.26) * mm, "end": v(14.48, -169.22) * mm});
            skLineSegment(sketch, "E900.541", {"start": v(14.48, -169.22) * mm, "end": v(15.6, -169.17) * mm});
            skLineSegment(sketch, "E900.542", {"start": v(15.6, -169.17) * mm, "end": v(16.71, -169.13) * mm});
            skLineSegment(sketch, "E900.543", {"start": v(16.71, -169.13) * mm, "end": v(17.83, -169.07) * mm});
            skLineSegment(sketch, "E900.544", {"start": v(17.83, -169.07) * mm, "end": v(18.94, -169.02) * mm});
            skLineSegment(sketch, "E900.545", {"start": v(18.94, -169.02) * mm, "end": v(20.05, -168.96) * mm});
            skLineSegment(sketch, "E900.546", {"start": v(20.05, -168.96) * mm, "end": v(21.17, -168.9) * mm});
            skLineSegment(sketch, "E900.547", {"start": v(21.17, -168.9) * mm, "end": v(22.28, -168.83) * mm});
            skLineSegment(sketch, "E900.548", {"start": v(22.28, -168.83) * mm, "end": v(23.4, -168.77) * mm});
            skLineSegment(sketch, "E900.549", {"start": v(23.4, -168.77) * mm, "end": v(24.51, -168.7) * mm});
            skLineSegment(sketch, "E900.550", {"start": v(24.51, -168.7) * mm, "end": v(25.62, -168.62) * mm});
            skLineSegment(sketch, "E900.551", {"start": v(25.62, -168.62) * mm, "end": v(26.74, -168.54) * mm});
            skLineSegment(sketch, "E900.552", {"start": v(26.74, -168.54) * mm, "end": v(27.85, -168.46) * mm});
            skLineSegment(sketch, "E900.553", {"start": v(27.85, -168.46) * mm, "end": v(28.97, -168.37) * mm});
            skLineSegment(sketch, "E900.554", {"start": v(28.97, -168.37) * mm, "end": v(30.08, -168.28) * mm});
            skLineSegment(sketch, "E900.555", {"start": v(30.08, -168.28) * mm, "end": v(31.2, -168.2) * mm});
            skLineSegment(sketch, "E900.556", {"start": v(31.2, -168.2) * mm, "end": v(32.3, -168.1) * mm});
            skLineSegment(sketch, "E900.557", {"start": v(32.3, -168.1) * mm, "end": v(33.42, -168) * mm});
            skLineSegment(sketch, "E900.558", {"start": v(33.42, -168) * mm, "end": v(34.54, -167.9) * mm});
            skLineSegment(sketch, "E900.559", {"start": v(34.54, -167.9) * mm, "end": v(35.65, -167.8) * mm});
            skLineSegment(sketch, "E900.560", {"start": v(35.65, -167.8) * mm, "end": v(36.76, -167.68) * mm});
            skLineSegment(sketch, "E900.561", {"start": v(36.76, -167.68) * mm, "end": v(37.88, -167.57) * mm});
            skLineSegment(sketch, "E900.562", {"start": v(37.88, -167.57) * mm, "end": v(39, -167.46) * mm});
            skLineSegment(sketch, "E900.563", {"start": v(39, -167.46) * mm, "end": v(40.1, -167.34) * mm});
            skLineSegment(sketch, "E900.564", {"start": v(40.1, -167.34) * mm, "end": v(41.22, -167.22) * mm});
            skLineSegment(sketch, "E900.565", {"start": v(41.22, -167.22) * mm, "end": v(42.34, -167.1) * mm});
            skLineSegment(sketch, "E900.566", {"start": v(42.34, -167.1) * mm, "end": v(43.45, -166.96) * mm});
            skLineSegment(sketch, "E900.567", {"start": v(43.45, -166.96) * mm, "end": v(44.56, -166.83) * mm});
            skLineSegment(sketch, "E900.568", {"start": v(44.56, -166.83) * mm, "end": v(45.68, -166.7) * mm});
            skLineSegment(sketch, "E900.569", {"start": v(45.68, -166.7) * mm, "end": v(46.8, -166.56) * mm});
            skLineSegment(sketch, "E900.570", {"start": v(46.8, -166.56) * mm, "end": v(47.9, -166.42) * mm});
            skLineSegment(sketch, "E900.571", {"start": v(47.9, -166.42) * mm, "end": v(49.02, -166.27) * mm});
            skLineSegment(sketch, "E900.572", {"start": v(49.02, -166.27) * mm, "end": v(50.13, -166.12) * mm});
            skLineSegment(sketch, "E900.573", {"start": v(50.13, -166.12) * mm, "end": v(51.25, -165.97) * mm});
            skLineSegment(sketch, "E900.574", {"start": v(51.25, -165.97) * mm, "end": v(52.36, -165.82) * mm});
            skLineSegment(sketch, "E900.575", {"start": v(52.36, -165.82) * mm, "end": v(53.48, -165.66) * mm});
            skLineSegment(sketch, "E900.576", {"start": v(53.48, -165.66) * mm, "end": v(54.59, -165.5) * mm});
            skLineSegment(sketch, "E900.577", {"start": v(54.59, -165.5) * mm, "end": v(55.7, -165.33) * mm});
            skLineSegment(sketch, "E900.578", {"start": v(55.7, -165.33) * mm, "end": v(56.82, -165.16) * mm});
            skLineSegment(sketch, "E900.579", {"start": v(56.82, -165.16) * mm, "end": v(57.93, -164.99) * mm});
            skLineSegment(sketch, "E900.580", {"start": v(57.93, -164.99) * mm, "end": v(59.05, -164.81) * mm});
            skLineSegment(sketch, "E900.581", {"start": v(59.05, -164.81) * mm, "end": v(60.16, -164.64) * mm});
            skLineSegment(sketch, "E900.582", {"start": v(60.16, -164.64) * mm, "end": v(61.27, -164.45) * mm});
            skLineSegment(sketch, "E900.583", {"start": v(61.27, -164.45) * mm, "end": v(62.39, -164.27) * mm});
            skLineSegment(sketch, "E900.584", {"start": v(62.39, -164.27) * mm, "end": v(63.5, -164.08) * mm});
            skLineSegment(sketch, "E900.585", {"start": v(63.5, -164.08) * mm, "end": v(64.62, -163.89) * mm});
            skLineSegment(sketch, "E900.586", {"start": v(64.62, -163.89) * mm, "end": v(65.73, -163.7) * mm});
            skLineSegment(sketch, "E900.587", {"start": v(65.73, -163.7) * mm, "end": v(66.84, -163.5) * mm});
            skLineSegment(sketch, "E900.588", {"start": v(66.84, -163.5) * mm, "end": v(67.96, -163.3) * mm});
            skLineSegment(sketch, "E900.589", {"start": v(67.96, -163.3) * mm, "end": v(69.07, -163.09) * mm});
            skLineSegment(sketch, "E900.590", {"start": v(69.07, -163.09) * mm, "end": v(70.19, -162.88) * mm});
            skLineSegment(sketch, "E900.591", {"start": v(70.19, -162.88) * mm, "end": v(71.3, -162.67) * mm});
            skLineSegment(sketch, "E900.592", {"start": v(71.3, -162.67) * mm, "end": v(72.41, -162.45) * mm});
            skLineSegment(sketch, "E900.593", {"start": v(72.41, -162.45) * mm, "end": v(73.53, -162.23) * mm});
            skLineSegment(sketch, "E900.594", {"start": v(73.53, -162.23) * mm, "end": v(74.64, -162.01) * mm});
            skLineSegment(sketch, "E900.595", {"start": v(74.64, -162.01) * mm, "end": v(75.75, -161.79) * mm});
            skLineSegment(sketch, "E900.596", {"start": v(75.75, -161.79) * mm, "end": v(76.87, -161.56) * mm});
            skLineSegment(sketch, "E900.597", {"start": v(76.87, -161.56) * mm, "end": v(77.98, -161.33) * mm});
            skLineSegment(sketch, "E900.598", {"start": v(77.98, -161.33) * mm, "end": v(79.1, -161.09) * mm});
            skLineSegment(sketch, "E900.599", {"start": v(79.1, -161.09) * mm, "end": v(80.21, -160.85) * mm});
            skLineSegment(sketch, "E900.600", {"start": v(80.21, -160.85) * mm, "end": v(81.32, -160.6) * mm});
            skLineSegment(sketch, "E900.601", {"start": v(81.32, -160.6) * mm, "end": v(82.44, -160.36) * mm});
            skLineSegment(sketch, "E900.602", {"start": v(82.44, -160.36) * mm, "end": v(83.55, -160.12) * mm});
            skLineSegment(sketch, "E900.603", {"start": v(83.55, -160.12) * mm, "end": v(84.67, -159.86) * mm});
            skLineSegment(sketch, "E900.604", {"start": v(84.67, -159.86) * mm, "end": v(85.78, -159.6) * mm});
            skLineSegment(sketch, "E900.605", {"start": v(85.78, -159.6) * mm, "end": v(86.9, -159.35) * mm});
            skLineSegment(sketch, "E900.606", {"start": v(86.9, -159.35) * mm, "end": v(88, -159.09) * mm});
            skLineSegment(sketch, "E900.607", {"start": v(88, -159.09) * mm, "end": v(89.12, -158.82) * mm});
            skLineSegment(sketch, "E900.608", {"start": v(89.12, -158.82) * mm, "end": v(90.24, -158.55) * mm});
            skLineSegment(sketch, "E900.609", {"start": v(90.24, -158.55) * mm, "end": v(91.35, -158.28) * mm});
            skLineSegment(sketch, "E900.610", {"start": v(91.35, -158.28) * mm, "end": v(92.46, -158) * mm});
            skLineSegment(sketch, "E900.611", {"start": v(92.46, -158) * mm, "end": v(93.58, -157.73) * mm});
            skLineSegment(sketch, "E900.612", {"start": v(93.58, -157.73) * mm, "end": v(94.7, -157.45) * mm});
            skLineSegment(sketch, "E900.613", {"start": v(94.7, -157.45) * mm, "end": v(95.8, -157.16) * mm});
            skLineSegment(sketch, "E900.614", {"start": v(95.8, -157.16) * mm, "end": v(96.92, -156.87) * mm});
            skLineSegment(sketch, "E900.615", {"start": v(96.92, -156.87) * mm, "end": v(98.03, -156.58) * mm});
            skLineSegment(sketch, "E900.616", {"start": v(98.03, -156.58) * mm, "end": v(99.15, -156.29) * mm});
            skLineSegment(sketch, "E900.617", {"start": v(99.15, -156.29) * mm, "end": v(100.26, -155.99) * mm});
            skLineSegment(sketch, "E900.618", {"start": v(100.26, -155.99) * mm, "end": v(101.37, -155.68) * mm});
            skLineSegment(sketch, "E900.619", {"start": v(101.37, -155.68) * mm, "end": v(102.49, -155.38) * mm});
            skLineSegment(sketch, "E900.620", {"start": v(102.49, -155.38) * mm, "end": v(103.6, -155.07) * mm});
            skLineSegment(sketch, "E900.621", {"start": v(103.6, -155.07) * mm, "end": v(104.72, -154.76) * mm});
            skLineSegment(sketch, "E900.622", {"start": v(104.72, -154.76) * mm, "end": v(105.83, -154.44) * mm});
            skLineSegment(sketch, "E900.623", {"start": v(105.83, -154.44) * mm, "end": v(106.94, -154.12) * mm});
            skLineSegment(sketch, "E900.624", {"start": v(106.94, -154.12) * mm, "end": v(108.06, -153.8) * mm});
            skLineSegment(sketch, "E900.625", {"start": v(108.06, -153.8) * mm, "end": v(109.17, -153.48) * mm});
            skLineSegment(sketch, "E900.626", {"start": v(109.17, -153.48) * mm, "end": v(110.28, -153.15) * mm});
            skLineSegment(sketch, "E900.627", {"start": v(110.28, -153.15) * mm, "end": v(111.4, -152.82) * mm});
            skLineSegment(sketch, "E900.628", {"start": v(111.4, -152.82) * mm, "end": v(112.51, -152.48) * mm});
            skLineSegment(sketch, "E900.629", {"start": v(112.51, -152.48) * mm, "end": v(113.63, -152.14) * mm});
            skLineSegment(sketch, "E900.630", {"start": v(113.63, -152.14) * mm, "end": v(114.74, -151.8) * mm});
            skLineSegment(sketch, "E900.631", {"start": v(114.74, -151.8) * mm, "end": v(115.85, -151.46) * mm});
            skLineSegment(sketch, "E900.632", {"start": v(115.85, -151.46) * mm, "end": v(116.97, -151.1) * mm});
            skLineSegment(sketch, "E900.633", {"start": v(116.97, -151.1) * mm, "end": v(118.08, -150.76) * mm});
            skLineSegment(sketch, "E900.634", {"start": v(118.08, -150.76) * mm, "end": v(119.2, -150.4) * mm});
            skLineSegment(sketch, "E900.635", {"start": v(119.2, -150.4) * mm, "end": v(120.3, -150.04) * mm});
            skLineSegment(sketch, "E900.636", {"start": v(120.3, -150.04) * mm, "end": v(121.42, -149.68) * mm});
            skLineSegment(sketch, "E900.637", {"start": v(121.42, -149.68) * mm, "end": v(122.54, -149.31) * mm});
            skLineSegment(sketch, "E900.638", {"start": v(122.54, -149.31) * mm, "end": v(123.65, -148.95) * mm});
            skLineSegment(sketch, "E900.639", {"start": v(123.65, -148.95) * mm, "end": v(124.76, -148.57) * mm});
            skLineSegment(sketch, "E900.640", {"start": v(124.76, -148.57) * mm, "end": v(125.88, -148.2) * mm});
            skLineSegment(sketch, "E900.641", {"start": v(125.88, -148.2) * mm, "end": v(126.99, -147.82) * mm});
            skLineSegment(sketch, "E900.642", {"start": v(126.99, -147.82) * mm, "end": v(128.1, -147.44) * mm});
            skLineSegment(sketch, "E900.643", {"start": v(128.1, -147.44) * mm, "end": v(129.22, -147.05) * mm});
            skLineSegment(sketch, "E900.644", {"start": v(129.22, -147.05) * mm, "end": v(130.33, -146.66) * mm});
            skLineSegment(sketch, "E900.645", {"start": v(130.33, -146.66) * mm, "end": v(131.44, -146.27) * mm});
            skLineSegment(sketch, "E900.646", {"start": v(131.44, -146.27) * mm, "end": v(132.56, -145.88) * mm});
            skLineSegment(sketch, "E900.647", {"start": v(132.56, -145.88) * mm, "end": v(133.67, -145.48) * mm});
            skLineSegment(sketch, "E900.648", {"start": v(133.67, -145.48) * mm, "end": v(134.79, -145.08) * mm});
            skLineSegment(sketch, "E900.649", {"start": v(134.79, -145.08) * mm, "end": v(135.9, -144.67) * mm});
            skLineSegment(sketch, "E900.650", {"start": v(135.9, -144.67) * mm, "end": v(137.01, -144.26) * mm});
            skLineSegment(sketch, "E900.651", {"start": v(137.01, -144.26) * mm, "end": v(138.13, -143.85) * mm});
            skLineSegment(sketch, "E900.652", {"start": v(138.13, -143.85) * mm, "end": v(139.24, -143.43) * mm});
            skLineSegment(sketch, "E900.653", {"start": v(139.24, -143.43) * mm, "end": v(140.35, -143.02) * mm});
            skLineSegment(sketch, "E900.654", {"start": v(140.35, -143.02) * mm, "end": v(141.47, -142.6) * mm});
            skLineSegment(sketch, "E900.655", {"start": v(141.47, -142.6) * mm, "end": v(142.58, -142.17) * mm});
            skLineSegment(sketch, "E900.656", {"start": v(142.58, -142.17) * mm, "end": v(143.7, -141.74) * mm});
            skLineSegment(sketch, "E900.657", {"start": v(143.7, -141.74) * mm, "end": v(144.8, -141.3) * mm});
            skLineSegment(sketch, "E900.658", {"start": v(144.8, -141.3) * mm, "end": v(145.92, -140.87) * mm});
            skLineSegment(sketch, "E900.659", {"start": v(145.92, -140.87) * mm, "end": v(147.03, -140.43) * mm});
            skLineSegment(sketch, "E900.660", {"start": v(147.03, -140.43) * mm, "end": v(148.15, -140) * mm});
            skLineSegment(sketch, "E900.661", {"start": v(148.15, -140) * mm, "end": v(149.26, -139.55) * mm});
            skLineSegment(sketch, "E900.662", {"start": v(149.26, -139.55) * mm, "end": v(150.37, -139.1) * mm});
            skLineSegment(sketch, "E900.663", {"start": v(150.37, -139.1) * mm, "end": v(151.49, -138.65) * mm});
            skLineSegment(sketch, "E900.664", {"start": v(151.49, -138.65) * mm, "end": v(152.6, -138.2) * mm});
            skLineSegment(sketch, "E900.665", {"start": v(152.6, -138.2) * mm, "end": v(153.72, -137.73) * mm});
            skLineSegment(sketch, "E900.666", {"start": v(153.72, -137.73) * mm, "end": v(154.83, -137.27) * mm});
            skLineSegment(sketch, "E900.667", {"start": v(154.83, -137.27) * mm, "end": v(155.94, -136.8) * mm});
            skLineSegment(sketch, "E900.668", {"start": v(155.94, -136.8) * mm, "end": v(157.06, -136.34) * mm});
            skLineSegment(sketch, "E900.669", {"start": v(157.06, -136.34) * mm, "end": v(158.17, -135.86) * mm});
            skLineSegment(sketch, "E900.670", {"start": v(158.17, -135.86) * mm, "end": v(159.28, -135.39) * mm});
            skLineSegment(sketch, "E900.671", {"start": v(159.28, -135.39) * mm, "end": v(160.4, -134.91) * mm});
            skLineSegment(sketch, "E900.672", {"start": v(160.4, -134.91) * mm, "end": v(161.5, -134.43) * mm});
            skLineSegment(sketch, "E900.673", {"start": v(161.5, -134.43) * mm, "end": v(162.62, -133.94) * mm});
            skLineSegment(sketch, "E900.674", {"start": v(162.62, -133.94) * mm, "end": v(163.74, -133.45) * mm});
            skLineSegment(sketch, "E900.675", {"start": v(163.74, -133.45) * mm, "end": v(164.85, -132.96) * mm});
            skLineSegment(sketch, "E900.676", {"start": v(164.85, -132.96) * mm, "end": v(165.96, -132.47) * mm});
            skLineSegment(sketch, "E900.677", {"start": v(165.96, -132.47) * mm, "end": v(167.08, -131.97) * mm});
            skLineSegment(sketch, "E900.678", {"start": v(167.08, -131.97) * mm, "end": v(168.19, -131.47) * mm});
            skLineSegment(sketch, "E900.679", {"start": v(168.19, -131.47) * mm, "end": v(169.3, -130.96) * mm});
            skLineSegment(sketch, "E900.680", {"start": v(169.3, -130.96) * mm, "end": v(170.42, -130.45) * mm});
            skLineSegment(sketch, "E900.681", {"start": v(170.42, -130.45) * mm, "end": v(171.53, -129.94) * mm});
            skLineSegment(sketch, "E900.682", {"start": v(171.53, -129.94) * mm, "end": v(172.64, -129.43) * mm});
            skLineSegment(sketch, "E900.683", {"start": v(172.64, -129.43) * mm, "end": v(173.76, -128.9) * mm});
            skLineSegment(sketch, "E900.684", {"start": v(173.76, -128.9) * mm, "end": v(174.87, -128.38) * mm});
            skLineSegment(sketch, "E900.685", {"start": v(174.87, -128.38) * mm, "end": v(175.98, -127.86) * mm});
            skLineSegment(sketch, "E900.686", {"start": v(175.98, -127.86) * mm, "end": v(177.1, -127.33) * mm});
            skLineSegment(sketch, "E900.687", {"start": v(177.1, -127.33) * mm, "end": v(178.2, -126.8) * mm});
            skLineSegment(sketch, "E900.688", {"start": v(178.2, -126.8) * mm, "end": v(179.32, -126.26) * mm});
            skLineSegment(sketch, "E900.689", {"start": v(179.32, -126.26) * mm, "end": v(180.44, -125.73) * mm});
            skLineSegment(sketch, "E900.690", {"start": v(180.44, -125.73) * mm, "end": v(181.55, -125.18) * mm});
            skLineSegment(sketch, "E900.691", {"start": v(181.55, -125.18) * mm, "end": v(182.66, -124.64) * mm});
            skLineSegment(sketch, "E900.692", {"start": v(182.66, -124.64) * mm, "end": v(183.78, -124.09) * mm});
            skLineSegment(sketch, "E900.693", {"start": v(183.78, -124.09) * mm, "end": v(184.89, -123.54) * mm});
            skLineSegment(sketch, "E900.694", {"start": v(184.89, -123.54) * mm, "end": v(186, -122.98) * mm});
            skLineSegment(sketch, "E900.695", {"start": v(186, -122.98) * mm, "end": v(187.12, -122.42) * mm});
            skLineSegment(sketch, "E900.696", {"start": v(187.12, -122.42) * mm, "end": v(188.23, -121.86) * mm});
            skLineSegment(sketch, "E900.697", {"start": v(188.23, -121.86) * mm, "end": v(189.34, -121.3) * mm});
            skLineSegment(sketch, "E900.698", {"start": v(189.34, -121.3) * mm, "end": v(190.46, -120.73) * mm});
            skLineSegment(sketch, "E900.699", {"start": v(190.46, -120.73) * mm, "end": v(191.57, -120.16) * mm});
            skLineSegment(sketch, "E900.700", {"start": v(191.57, -120.16) * mm, "end": v(192.68, -119.58) * mm});
            skLineSegment(sketch, "E900.701", {"start": v(192.68, -119.58) * mm, "end": v(193.8, -119) * mm});
            skLineSegment(sketch, "E900.702", {"start": v(193.8, -119) * mm, "end": v(194.9, -118.42) * mm});
            skLineSegment(sketch, "E900.703", {"start": v(194.9, -118.42) * mm, "end": v(196.02, -117.83) * mm});
            skLineSegment(sketch, "E900.704", {"start": v(196.02, -117.83) * mm, "end": v(197.13, -117.25) * mm});
            skLineSegment(sketch, "E900.705", {"start": v(197.13, -117.25) * mm, "end": v(198.25, -116.65) * mm});
            skLineSegment(sketch, "E900.706", {"start": v(198.25, -116.65) * mm, "end": v(199.36, -116.06) * mm});
            skLineSegment(sketch, "E900.707", {"start": v(199.36, -116.06) * mm, "end": v(200.47, -115.46) * mm});
            skLineSegment(sketch, "E900.708", {"start": v(200.47, -115.46) * mm, "end": v(201.59, -114.86) * mm});
            skLineSegment(sketch, "E900.709", {"start": v(201.59, -114.86) * mm, "end": v(202.7, -114.25) * mm});
            skLineSegment(sketch, "E900.710", {"start": v(202.7, -114.25) * mm, "end": v(203.81, -113.65) * mm});
            skLineSegment(sketch, "E900.711", {"start": v(203.81, -113.65) * mm, "end": v(204.93, -113.03) * mm});
            skLineSegment(sketch, "E900.712", {"start": v(204.93, -113.03) * mm, "end": v(206.04, -112.42) * mm});
            skLineSegment(sketch, "E900.713", {"start": v(206.04, -112.42) * mm, "end": v(207.15, -111.8) * mm});
            skLineSegment(sketch, "E900.714", {"start": v(207.15, -111.8) * mm, "end": v(208.27, -111.18) * mm});
            skLineSegment(sketch, "E900.715", {"start": v(208.27, -111.18) * mm, "end": v(209.38, -110.55) * mm});
            skLineSegment(sketch, "E900.716", {"start": v(209.38, -110.55) * mm, "end": v(210.5, -109.92) * mm});
            skLineSegment(sketch, "E900.717", {"start": v(210.5, -109.92) * mm, "end": v(211.6, -109.3) * mm});
            skLineSegment(sketch, "E900.718", {"start": v(211.6, -109.3) * mm, "end": v(212.72, -108.66) * mm});
            skLineSegment(sketch, "E900.719", {"start": v(212.72, -108.66) * mm, "end": v(213.83, -108.02) * mm});
            skLineSegment(sketch, "E900.720", {"start": v(213.83, -108.02) * mm, "end": v(214.94, -107.38) * mm});
            skLineSegment(sketch, "E900.721", {"start": v(214.94, -107.38) * mm, "end": v(216.06, -106.73) * mm});
            skLineSegment(sketch, "E900.722", {"start": v(216.06, -106.73) * mm, "end": v(217.17, -106.08) * mm});
            skLineSegment(sketch, "E900.723", {"start": v(217.17, -106.08) * mm, "end": v(218.28, -105.43) * mm});
            skLineSegment(sketch, "E900.724", {"start": v(218.28, -105.43) * mm, "end": v(219.4, -104.78) * mm});
            skLineSegment(sketch, "E900.725", {"start": v(219.4, -104.78) * mm, "end": v(220.51, -104.12) * mm});
            skLineSegment(sketch, "E900.726", {"start": v(220.51, -104.12) * mm, "end": v(221.62, -103.46) * mm});
            skLineSegment(sketch, "E900.727", {"start": v(221.62, -103.46) * mm, "end": v(222.74, -102.8) * mm});
            skLineSegment(sketch, "E900.728", {"start": v(222.74, -102.8) * mm, "end": v(223.85, -102.12) * mm});
            skLineSegment(sketch, "E900.729", {"start": v(223.85, -102.12) * mm, "end": v(224.96, -101.45) * mm});
            skLineSegment(sketch, "E900.730", {"start": v(224.96, -101.45) * mm, "end": v(226.08, -100.77) * mm});
            skLineSegment(sketch, "E900.731", {"start": v(226.08, -100.77) * mm, "end": v(227.19, -100.1) * mm});
            skLineSegment(sketch, "E900.732", {"start": v(227.19, -100.1) * mm, "end": v(228.3, -99.41) * mm});
            skLineSegment(sketch, "E900.733", {"start": v(228.3, -99.41) * mm, "end": v(229.41, -98.73) * mm});
            skLineSegment(sketch, "E900.734", {"start": v(229.41, -98.73) * mm, "end": v(230.53, -98.04) * mm});
            skLineSegment(sketch, "E900.735", {"start": v(230.53, -98.04) * mm, "end": v(231.64, -97.35) * mm});
            skLineSegment(sketch, "E900.736", {"start": v(231.64, -97.35) * mm, "end": v(232.75, -96.65) * mm});
            skLineSegment(sketch, "E900.737", {"start": v(232.75, -96.65) * mm, "end": v(233.87, -95.96) * mm});
            skLineSegment(sketch, "E900.738", {"start": v(233.87, -95.96) * mm, "end": v(234.98, -95.25) * mm});
            skLineSegment(sketch, "E900.739", {"start": v(234.98, -95.25) * mm, "end": v(236.1, -94.55) * mm});
            skLineSegment(sketch, "E900.740", {"start": v(236.1, -94.55) * mm, "end": v(237.2, -93.84) * mm});
            skLineSegment(sketch, "E900.741", {"start": v(237.2, -93.84) * mm, "end": v(238.32, -93.13) * mm});
            skLineSegment(sketch, "E900.742", {"start": v(238.32, -93.13) * mm, "end": v(239.43, -92.41) * mm});
            skLineSegment(sketch, "E900.743", {"start": v(239.43, -92.41) * mm, "end": v(240.54, -91.7) * mm});
            skLineSegment(sketch, "E900.744", {"start": v(240.54, -91.7) * mm, "end": v(241.66, -90.97) * mm});
            skLineSegment(sketch, "E900.745", {"start": v(241.66, -90.97) * mm, "end": v(242.77, -90.25) * mm});
            skLineSegment(sketch, "E900.746", {"start": v(242.77, -90.25) * mm, "end": v(243.88, -89.52) * mm});
            skLineSegment(sketch, "E900.747", {"start": v(243.88, -89.52) * mm, "end": v(245, -88.79) * mm});
            skLineSegment(sketch, "E900.748", {"start": v(245, -88.79) * mm, "end": v(246.1, -88.05) * mm});
            skLineSegment(sketch, "E900.749", {"start": v(246.1, -88.05) * mm, "end": v(247.22, -87.31) * mm});
            skLineSegment(sketch, "E900.750", {"start": v(247.22, -87.31) * mm, "end": v(248.33, -86.57) * mm});
            skLineSegment(sketch, "E900.751", {"start": v(248.33, -86.57) * mm, "end": v(249.45, -85.83) * mm});
            skLineSegment(sketch, "E900.752", {"start": v(249.45, -85.83) * mm, "end": v(250.56, -85.08) * mm});
            skLineSegment(sketch, "E900.753", {"start": v(250.56, -85.08) * mm, "end": v(251.67, -84.33) * mm});
            skLineSegment(sketch, "E900.754", {"start": v(251.67, -84.33) * mm, "end": v(252.78, -83.57) * mm});
            skLineSegment(sketch, "E900.755", {"start": v(252.78, -83.57) * mm, "end": v(253.9, -82.81) * mm});
            skLineSegment(sketch, "E900.756", {"start": v(253.9, -82.81) * mm, "end": v(255.01, -82.05) * mm});
            skLineSegment(sketch, "E900.757", {"start": v(255.01, -82.05) * mm, "end": v(256.12, -81.29) * mm});
            skLineSegment(sketch, "E900.758", {"start": v(256.12, -81.29) * mm, "end": v(257.24, -80.52) * mm});
            skLineSegment(sketch, "E900.759", {"start": v(257.24, -80.52) * mm, "end": v(258.35, -79.75) * mm});
            skLineSegment(sketch, "E900.760", {"start": v(258.35, -79.75) * mm, "end": v(259.46, -78.97) * mm});
            skLineSegment(sketch, "E900.761", {"start": v(259.46, -78.97) * mm, "end": v(260.57, -78.2) * mm});
            skLineSegment(sketch, "E900.762", {"start": v(260.57, -78.2) * mm, "end": v(261.69, -77.41) * mm});
            skLineSegment(sketch, "E900.763", {"start": v(261.69, -77.41) * mm, "end": v(262.8, -76.63) * mm});
            skLineSegment(sketch, "E900.764", {"start": v(262.8, -76.63) * mm, "end": v(263.91, -75.84) * mm});
            skLineSegment(sketch, "E900.765", {"start": v(263.91, -75.84) * mm, "end": v(265.02, -75.05) * mm});
            skLineSegment(sketch, "E900.766", {"start": v(265.02, -75.05) * mm, "end": v(266.14, -74.25) * mm});
            skLineSegment(sketch, "E900.767", {"start": v(266.14, -74.25) * mm, "end": v(267.25, -73.45) * mm});
            skLineSegment(sketch, "E900.768", {"start": v(267.25, -73.45) * mm, "end": v(268.36, -72.65) * mm});
            skLineSegment(sketch, "E900.769", {"start": v(268.36, -72.65) * mm, "end": v(269.48, -71.85) * mm});
            skLineSegment(sketch, "E900.770", {"start": v(269.48, -71.85) * mm, "end": v(270.59, -71.04) * mm});
            skLineSegment(sketch, "E900.771", {"start": v(270.59, -71.04) * mm, "end": v(271.7, -70.23) * mm});
            skLineSegment(sketch, "E900.772", {"start": v(271.7, -70.23) * mm, "end": v(272.81, -69.41) * mm});
            skLineSegment(sketch, "E900.773", {"start": v(272.81, -69.41) * mm, "end": v(273.93, -68.6) * mm});
            skLineSegment(sketch, "E900.774", {"start": v(273.93, -68.6) * mm, "end": v(275.04, -67.77) * mm});
            skLineSegment(sketch, "E900.775", {"start": v(275.04, -67.77) * mm, "end": v(276.15, -66.95) * mm});
            skLineSegment(sketch, "E900.776", {"start": v(276.15, -66.95) * mm, "end": v(277.26, -66.12) * mm});
            skLineSegment(sketch, "E900.777", {"start": v(277.26, -66.12) * mm, "end": v(278.38, -65.29) * mm});
            skLineSegment(sketch, "E900.778", {"start": v(278.38, -65.29) * mm, "end": v(279.49, -64.45) * mm});
            skLineSegment(sketch, "E900.779", {"start": v(279.49, -64.45) * mm, "end": v(280.6, -63.62) * mm});
            skLineSegment(sketch, "E900.780", {"start": v(280.6, -63.62) * mm, "end": v(281.72, -62.77) * mm});
            skLineSegment(sketch, "E900.781", {"start": v(281.72, -62.77) * mm, "end": v(282.83, -61.93) * mm});
            skLineSegment(sketch, "E900.782", {"start": v(282.83, -61.93) * mm, "end": v(283.94, -61.08) * mm});
            skLineSegment(sketch, "E900.783", {"start": v(283.94, -61.08) * mm, "end": v(285.05, -60.23) * mm});
            skLineSegment(sketch, "E900.784", {"start": v(285.05, -60.23) * mm, "end": v(286.17, -59.37) * mm});
            skLineSegment(sketch, "E900.785", {"start": v(286.17, -59.37) * mm, "end": v(287.28, -58.52) * mm});
            skLineSegment(sketch, "E900.786", {"start": v(287.28, -58.52) * mm, "end": v(288.4, -57.65) * mm});
            skLineSegment(sketch, "E900.787", {"start": v(288.4, -57.65) * mm, "end": v(289.5, -56.79) * mm});
            skLineSegment(sketch, "E900.788", {"start": v(289.5, -56.79) * mm, "end": v(290.62, -55.92) * mm});
            skLineSegment(sketch, "E900.789", {"start": v(290.62, -55.92) * mm, "end": v(291.73, -55.05) * mm});
            skLineSegment(sketch, "E900.790", {"start": v(291.73, -55.05) * mm, "end": v(292.84, -54.17) * mm});
            skLineSegment(sketch, "E900.791", {"start": v(292.84, -54.17) * mm, "end": v(293.95, -53.3) * mm});
            skLineSegment(sketch, "E900.792", {"start": v(293.95, -53.3) * mm, "end": v(295.07, -52.41) * mm});
            skLineSegment(sketch, "E900.793", {"start": v(295.07, -52.41) * mm, "end": v(296.18, -51.53) * mm});
            skLineSegment(sketch, "E900.794", {"start": v(296.18, -51.53) * mm, "end": v(297.3, -50.64) * mm});
            skLineSegment(sketch, "E900.795", {"start": v(297.3, -50.64) * mm, "end": v(298.4, -49.75) * mm});
            skLineSegment(sketch, "E900.796", {"start": v(298.4, -49.75) * mm, "end": v(299.52, -48.86) * mm});
            skLineSegment(sketch, "E900.797", {"start": v(299.52, -48.86) * mm, "end": v(300.63, -47.96) * mm});
            skLineSegment(sketch, "E900.798", {"start": v(300.63, -47.96) * mm, "end": v(301.74, -47.06) * mm});
            skLineSegment(sketch, "E900.799", {"start": v(301.74, -47.06) * mm, "end": v(302.85, -46.15) * mm});
            skLineSegment(sketch, "E900.800", {"start": v(302.85, -46.15) * mm, "end": v(303.97, -45.24) * mm});
            skLineSegment(sketch, "E900.801", {"start": v(303.97, -45.24) * mm, "end": v(305.08, -44.33) * mm});
            skLineSegment(sketch, "E900.802", {"start": v(305.08, -44.33) * mm, "end": v(306.2, -43.42) * mm});
            skLineSegment(sketch, "E900.803", {"start": v(306.2, -43.42) * mm, "end": v(307.3, -42.5) * mm});
            skLineSegment(sketch, "E900.804", {"start": v(307.3, -42.5) * mm, "end": v(308.42, -41.58) * mm});
            skLineSegment(sketch, "E900.805", {"start": v(308.42, -41.58) * mm, "end": v(309.53, -40.65) * mm});
            skLineSegment(sketch, "E900.806", {"start": v(309.53, -40.65) * mm, "end": v(310.64, -39.72) * mm});
            skLineSegment(sketch, "E900.807", {"start": v(310.64, -39.72) * mm, "end": v(311.75, -38.8) * mm});
            skLineSegment(sketch, "E900.808", {"start": v(311.75, -38.8) * mm, "end": v(312.87, -37.86) * mm});
            skLineSegment(sketch, "E900.809", {"start": v(312.87, -37.86) * mm, "end": v(313.98, -36.92) * mm});
            skLineSegment(sketch, "E900.810", {"start": v(313.98, -36.92) * mm, "end": v(315.1, -35.98) * mm});
            skLineSegment(sketch, "E900.811", {"start": v(315.1, -35.98) * mm, "end": v(316.2, -35.03) * mm});
            skLineSegment(sketch, "E900.812", {"start": v(316.2, -35.03) * mm, "end": v(317.32, -34.09) * mm});
            skLineSegment(sketch, "E900.813", {"start": v(317.32, -34.09) * mm, "end": v(318.43, -33.13) * mm});
            skLineSegment(sketch, "E900.814", {"start": v(318.43, -33.13) * mm, "end": v(319.54, -32.18) * mm});
            skLineSegment(sketch, "E900.815", {"start": v(319.54, -32.18) * mm, "end": v(320.65, -31.22) * mm});
            skLineSegment(sketch, "E900.816", {"start": v(320.65, -31.22) * mm, "end": v(321.77, -30.26) * mm});
            skLineSegment(sketch, "E900.817", {"start": v(321.77, -30.26) * mm, "end": v(322.88, -29.3) * mm});
            skLineSegment(sketch, "E900.818", {"start": v(322.88, -29.3) * mm, "end": v(324, -28.33) * mm});
            skLineSegment(sketch, "E900.819", {"start": v(324, -28.33) * mm, "end": v(325.1, -27.36) * mm});
            skLineSegment(sketch, "E900.820", {"start": v(325.1, -27.36) * mm, "end": v(326.22, -26.38) * mm});
            skLineSegment(sketch, "E900.821", {"start": v(326.22, -26.38) * mm, "end": v(327.33, -25.4) * mm});
            skLineSegment(sketch, "E900.822", {"start": v(327.33, -25.4) * mm, "end": v(328.44, -24.42) * mm});
            skLineSegment(sketch, "E900.823", {"start": v(328.44, -24.42) * mm, "end": v(329.55, -23.44) * mm});
            skLineSegment(sketch, "E900.824", {"start": v(329.55, -23.44) * mm, "end": v(330.66, -22.45) * mm});
            skLineSegment(sketch, "E900.825", {"start": v(330.66, -22.45) * mm, "end": v(331.78, -21.46) * mm});
            skLineSegment(sketch, "E900.826", {"start": v(331.78, -21.46) * mm, "end": v(332.89, -20.46) * mm});
            skLineSegment(sketch, "E900.827", {"start": v(332.89, -20.46) * mm, "end": v(334, -19.47) * mm});
            skLineSegment(sketch, "E900.828", {"start": v(334, -19.47) * mm, "end": v(335.11, -18.46) * mm});
            skLineSegment(sketch, "E900.829", {"start": v(335.11, -18.46) * mm, "end": v(336.23, -17.46) * mm});
            skLineSegment(sketch, "E900.830", {"start": v(336.23, -17.46) * mm, "end": v(337.34, -16.45) * mm});
            skLineSegment(sketch, "E900.831", {"start": v(337.34, -16.45) * mm, "end": v(338.45, -15.44) * mm});
            skLineSegment(sketch, "E900.832", {"start": v(338.45, -15.44) * mm, "end": v(339.56, -14.43) * mm});
            skLineSegment(sketch, "E900.833", {"start": v(339.56, -14.43) * mm, "end": v(340.68, -13.4) * mm});
            skLineSegment(sketch, "E900.834", {"start": v(340.68, -13.4) * mm, "end": v(341.79, -12.39) * mm});
            skLineSegment(sketch, "E900.835", {"start": v(341.79, -12.39) * mm, "end": v(342.9, -11.36) * mm});
            skLineSegment(sketch, "E900.836", {"start": v(342.9, -11.36) * mm, "end": v(344.01, -10.33) * mm});
            skLineSegment(sketch, "E900.837", {"start": v(344.01, -10.33) * mm, "end": v(345.12, -9.3) * mm});
            skLineSegment(sketch, "E900.838", {"start": v(345.12, -9.3) * mm, "end": v(346.24, -8.27) * mm});
            skLineSegment(sketch, "E900.839", {"start": v(346.24, -8.27) * mm, "end": v(347.35, -7.23) * mm});
            skLineSegment(sketch, "E900.840", {"start": v(347.35, -7.23) * mm, "end": v(348.46, -6.19) * mm});
            skLineSegment(sketch, "E900.841", {"start": v(348.46, -6.19) * mm, "end": v(349.57, -5.14) * mm});
            skLineSegment(sketch, "E900.842", {"start": v(349.57, -5.14) * mm, "end": v(350.69, -4.1) * mm});
            skLineSegment(sketch, "E900.843", {"start": v(350.69, -4.1) * mm, "end": v(351.8, -3.05) * mm});
            skLineSegment(sketch, "E900.844", {"start": v(351.8, -3.05) * mm, "end": v(352.91, -2) * mm});
            skLineSegment(sketch, "E900.845", {"start": v(352.91, -2) * mm, "end": v(354.02, -0.93) * mm});
            skLineSegment(sketch, "E900.846", {"start": v(354.02, -0.93) * mm, "end": v(355.14, 0.13) * mm});
            skLineSegment(sketch, "E900.847", {"start": v(355.14, 0.13) * mm, "end": v(356.25, 1.2) * mm});
            skLineSegment(sketch, "E900.848", {"start": v(356.25, 1.2) * mm, "end": v(357.36, 2.26) * mm});
            skLineSegment(sketch, "E900.849", {"start": v(357.36, 2.26) * mm, "end": v(358.47, 3.33) * mm});
            skLineSegment(sketch, "E900.850", {"start": v(358.47, 3.33) * mm, "end": v(359.58, 4.4) * mm});
            skLineSegment(sketch, "E900.851", {"start": v(359.58, 4.4) * mm, "end": v(360.7, 5.48) * mm});
            skLineSegment(sketch, "E900.852", {"start": v(360.7, 5.48) * mm, "end": v(361.8, 6.56) * mm});
            skLineSegment(sketch, "E900.853", {"start": v(361.8, 6.56) * mm, "end": v(362.92, 7.65) * mm});
            skLineSegment(sketch, "E900.854", {"start": v(362.92, 7.65) * mm, "end": v(364.03, 8.74) * mm});
            skLineSegment(sketch, "E900.855", {"start": v(364.03, 8.74) * mm, "end": v(365.15, 9.83) * mm});
            skLineSegment(sketch, "E900.856", {"start": v(365.15, 9.83) * mm, "end": v(366.26, 10.92) * mm});
            skLineSegment(sketch, "E900.857", {"start": v(366.26, 10.92) * mm, "end": v(367.37, 12.02) * mm});
            skLineSegment(sketch, "E900.858", {"start": v(367.37, 12.02) * mm, "end": v(368.48, 13.12) * mm});
            skLineSegment(sketch, "E900.859", {"start": v(368.48, 13.12) * mm, "end": v(369.6, 14.23) * mm});
            skLineSegment(sketch, "E900.860", {"start": v(369.6, 14.23) * mm, "end": v(370.7, 15.33) * mm});
            skLineSegment(sketch, "E900.861", {"start": v(370.7, 15.33) * mm, "end": v(371.82, 16.44) * mm});
            skLineSegment(sketch, "E900.862", {"start": v(371.82, 16.44) * mm, "end": v(372.93, 17.56) * mm});
            skLineSegment(sketch, "E900.863", {"start": v(372.93, 17.56) * mm, "end": v(374.04, 18.68) * mm});
            skLineSegment(sketch, "E900.864", {"start": v(374.04, 18.68) * mm, "end": v(375.15, 19.8) * mm});
            skLineSegment(sketch, "E900.865", {"start": v(375.15, 19.8) * mm, "end": v(376.27, 20.92) * mm});
            skLineSegment(sketch, "E900.866", {"start": v(376.27, 20.92) * mm, "end": v(377.38, 22.05) * mm});
            skLineSegment(sketch, "E900.867", {"start": v(377.38, 22.05) * mm, "end": v(378.5, 23.18) * mm});
            skLineSegment(sketch, "E900.868", {"start": v(378.5, 23.18) * mm, "end": v(379.6, 24.32) * mm});
            skLineSegment(sketch, "E900.869", {"start": v(379.6, 24.32) * mm, "end": v(380.72, 25.45) * mm});
            skLineSegment(sketch, "E900.870", {"start": v(380.72, 25.45) * mm, "end": v(381.83, 26.6) * mm});
            skLineSegment(sketch, "E900.871", {"start": v(381.83, 26.6) * mm, "end": v(382.94, 27.74) * mm});
            skLineSegment(sketch, "E900.872", {"start": v(382.94, 27.74) * mm, "end": v(384.05, 28.89) * mm});
            skLineSegment(sketch, "E900.873", {"start": v(384.05, 28.89) * mm, "end": v(385.16, 30.04) * mm});
            skLineSegment(sketch, "E900.874", {"start": v(385.16, 30.04) * mm, "end": v(386.28, 31.2) * mm});
            skLineSegment(sketch, "E900.875", {"start": v(386.28, 31.2) * mm, "end": v(387.39, 32.35) * mm});
            skLineSegment(sketch, "E900.876", {"start": v(387.39, 32.35) * mm, "end": v(388.5, 33.51) * mm});
            skLineSegment(sketch, "E900.877", {"start": v(388.5, 33.51) * mm, "end": v(389.61, 34.67) * mm});
            skLineSegment(sketch, "E900.878", {"start": v(389.61, 34.67) * mm, "end": v(390.72, 35.84) * mm});
            skLineSegment(sketch, "E900.879", {"start": v(390.72, 35.84) * mm, "end": v(391.84, 37.01) * mm});
            skLineSegment(sketch, "E900.880", {"start": v(391.84, 37.01) * mm, "end": v(392.95, 38.19) * mm});
            skLineSegment(sketch, "E900.881", {"start": v(392.95, 38.19) * mm, "end": v(394.06, 39.37) * mm});
            skLineSegment(sketch, "E900.882", {"start": v(394.06, 39.37) * mm, "end": v(395.17, 40.55) * mm});
            skLineSegment(sketch, "E900.883", {"start": v(395.17, 40.55) * mm, "end": v(396.28, 41.73) * mm});
            skLineSegment(sketch, "E900.884", {"start": v(396.28, 41.73) * mm, "end": v(397.4, 42.92) * mm});
            skLineSegment(sketch, "E900.885", {"start": v(397.4, 42.92) * mm, "end": v(398.5, 44.1) * mm});
            skLineSegment(sketch, "E900.886", {"start": v(398.5, 44.1) * mm, "end": v(399.62, 45.3) * mm});
            skLineSegment(sketch, "E900.887", {"start": v(399.62, 45.3) * mm, "end": v(400.73, 46.5) * mm});
            skLineSegment(sketch, "E900.888", {"start": v(400.73, 46.5) * mm, "end": v(401.85, 47.7) * mm});
            skLineSegment(sketch, "E900.889", {"start": v(401.85, 47.7) * mm, "end": v(402.96, 48.9) * mm});
            skLineSegment(sketch, "E900.890", {"start": v(402.96, 48.9) * mm, "end": v(404.07, 50.11) * mm});
            skLineSegment(sketch, "E900.891", {"start": v(404.07, 50.11) * mm, "end": v(405.18, 51.32) * mm});
            skLineSegment(sketch, "E900.892", {"start": v(405.18, 51.32) * mm, "end": v(406.3, 52.54) * mm});
            skLineSegment(sketch, "E900.893", {"start": v(406.3, 52.54) * mm, "end": v(407.4, 53.76) * mm});
            skLineSegment(sketch, "E900.894", {"start": v(407.4, 53.76) * mm, "end": v(408.52, 54.98) * mm});
            skLineSegment(sketch, "E900.895", {"start": v(408.52, 54.98) * mm, "end": v(409.63, 56.2) * mm});
            skLineSegment(sketch, "E900.896", {"start": v(409.63, 56.2) * mm, "end": v(410.74, 57.43) * mm});
            skLineSegment(sketch, "E900.897", {"start": v(410.74, 57.43) * mm, "end": v(411.85, 58.66) * mm});
            skLineSegment(sketch, "E900.898", {"start": v(411.85, 58.66) * mm, "end": v(412.97, 59.9) * mm});
            skLineSegment(sketch, "E900.899", {"start": v(412.97, 59.9) * mm, "end": v(414.08, 61.13) * mm});
            skLineSegment(sketch, "E901", {"start": v(-500, 168.5) * mm, "end": v(-500.8, 167.9) * mm});
            skLineSegment(sketch, "E902", {"start": v(500, 168.5) * mm, "end": v(500.8, 167.9) * mm});
            skSolve(sketch);
        }
        {
            var Q0;
            Q0=makeQuery(id+"F0.imprint","IMPRINT",FACE,{"disambiguationData":[TD([[makeQuery(id+"F0.imprint","IMPRINT",EDGE,{"derivedFrom":sQuery(id+"F0.wireOp",EDGE,"E0")}),-1.0]])]});
            extrude(context, id + "F1", {"entities" : qUnion([Q0]), "depth" : 1000 * mm});
        }
    });
